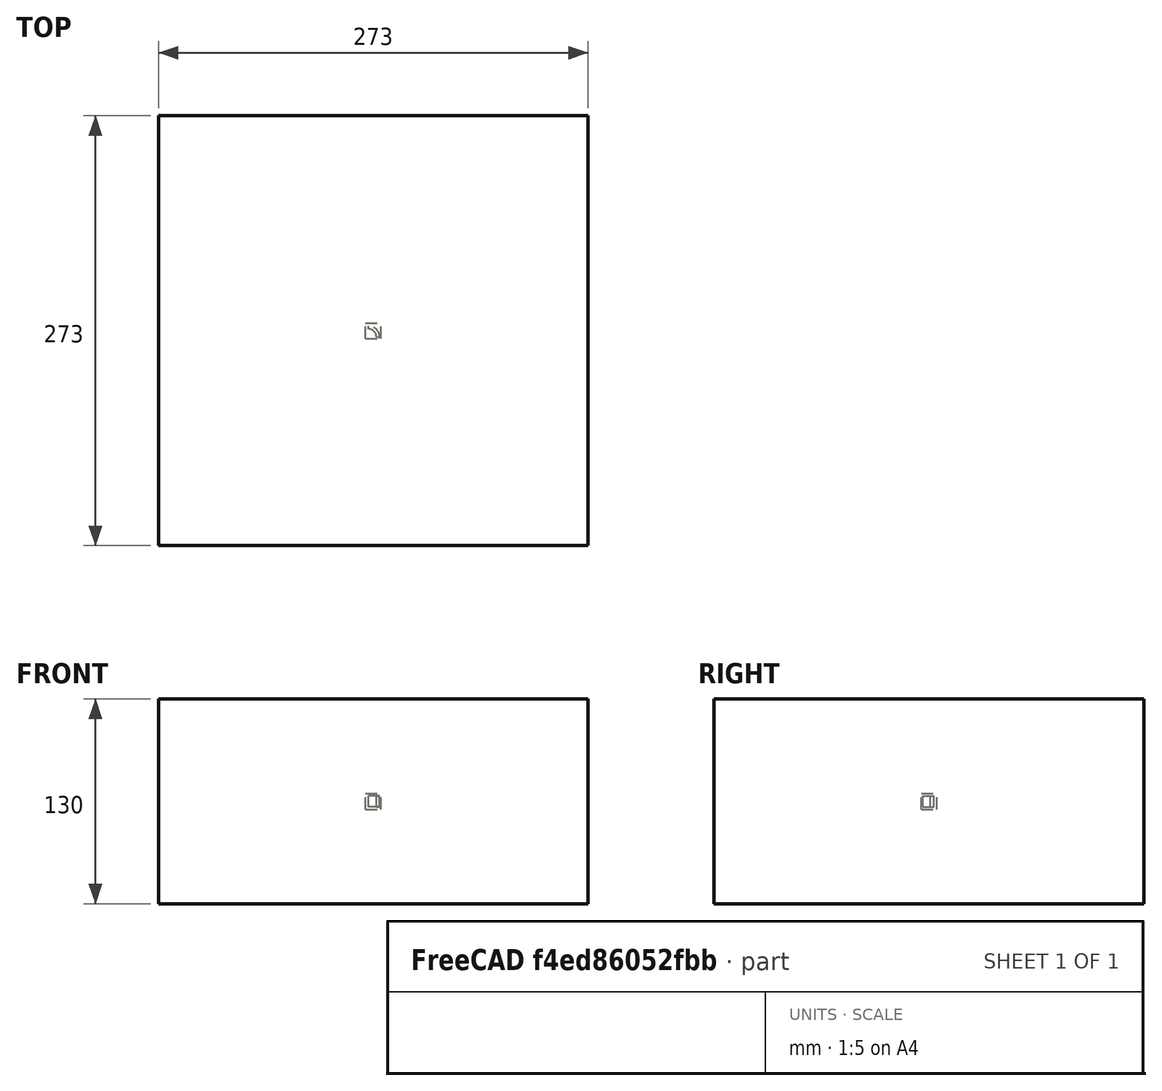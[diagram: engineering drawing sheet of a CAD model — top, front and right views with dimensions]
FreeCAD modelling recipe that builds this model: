
FCSTD DOCUMENT  (FreeCAD 0.20RUnknown)
Label: polarArray-container-c
License: All rights reserved
LicenseURL: http://en.wikipedia.org/wiki/All_rights_reserved
objects: App::DocumentObjectGroupPython×1251, Part::FeaturePython×4, App::Part×4
note: 3 computed .brp shape members not serialized (recipe doc carries the construction recipe); baked Part::Feature solids carry a one-line shape summary decoded from their .brp

FEATURE [App::DocumentObjectGroupPython] HALFPI  # scripted group (container) (typed FeaturePython)
  name = HALFPI
  value = pi/2.
FEATURE [App::DocumentObjectGroupPython] PI  # scripted group (container) (typed FeaturePython)
  name = PI
  value = 1.*pi
FEATURE [App::DocumentObjectGroupPython] TWOPI  # scripted group (container) (typed FeaturePython)
  name = TWOPI
  value = 2.*pi
FEATURE [App::DocumentObjectGroupPython] Constants  # scripted group (container) (typed FeaturePython)
  Group = -> [HALFPI,PI,TWOPI]
FEATURE [App::DocumentObjectGroupPython] Variables  # scripted group (container) (typed FeaturePython)
FEATURE [App::DocumentObjectGroupPython] Quantities  # scripted group (container) (typed FeaturePython)
FEATURE [App::DocumentObjectGroupPython] Isotopes  # scripted group (container) (typed FeaturePython)
FEATURE [App::DocumentObjectGroupPython] Elements  # scripted group (container) (typed FeaturePython)
FEATURE [App::DocumentObjectGroupPython] Matrix  # scripted group (container) (typed FeaturePython)
FEATURE [App::DocumentObjectGroupPython] Surfaces  # scripted group (container) (typed FeaturePython)
FEATURE [App::DocumentObjectGroupPython] Opticals  # scripted group (container) (typed FeaturePython)
  Group = -> [Matrix,Surfaces]
FEATURE [App::DocumentObjectGroupPython] G4Isotopes  # scripted group (container) (typed FeaturePython)
FEATURE [App::DocumentObjectGroupPython] H_element  # scripted group (container) (typed FeaturePython)
  Z = 1
  atom_value = 1.008
  formula = H
  name = H_element
FEATURE [App::DocumentObjectGroupPython] He_element  # scripted group (container) (typed FeaturePython)
  Z = 2
  atom_value = 4.0026
  formula = He
  name = He_element
FEATURE [App::DocumentObjectGroupPython] Li_element  # scripted group (container) (typed FeaturePython)
  Z = 3
  atom_value = 6.94
  formula = Li
  name = Li_element
FEATURE [App::DocumentObjectGroupPython] Be_element  # scripted group (container) (typed FeaturePython)
  Z = 4
  atom_value = 9.01218
  formula = Be
  name = Be_element
FEATURE [App::DocumentObjectGroupPython] B_element  # scripted group (container) (typed FeaturePython)
  Z = 5
  atom_value = 10.81
  formula = B
  name = B_element
FEATURE [App::DocumentObjectGroupPython] C_element  # scripted group (container) (typed FeaturePython)
  Z = 6
  atom_value = 12.011
  formula = C
  name = C_element
FEATURE [App::DocumentObjectGroupPython] N_element  # scripted group (container) (typed FeaturePython)
  Z = 7
  atom_value = 14.007
  formula = N
  name = N_element
FEATURE [App::DocumentObjectGroupPython] O_element  # scripted group (container) (typed FeaturePython)
  Z = 8
  atom_value = 15.999
  formula = O
  name = O_element
FEATURE [App::DocumentObjectGroupPython] F_element  # scripted group (container) (typed FeaturePython)
  Z = 9
  atom_value = 18.9984
  formula = F
  name = F_element
FEATURE [App::DocumentObjectGroupPython] Ne_element  # scripted group (container) (typed FeaturePython)
  Z = 10
  atom_value = 20.1797
  formula = Ne
  name = Ne_element
FEATURE [App::DocumentObjectGroupPython] Na_element  # scripted group (container) (typed FeaturePython)
  Z = 11
  atom_value = 22.9898
  formula = Na
  name = Na_element
FEATURE [App::DocumentObjectGroupPython] Mg_element  # scripted group (container) (typed FeaturePython)
  Z = 12
  atom_value = 24.305
  formula = Mg
  name = Mg_element
FEATURE [App::DocumentObjectGroupPython] Al_element  # scripted group (container) (typed FeaturePython)
  Z = 13
  atom_value = 26.9815
  formula = Al
  name = Al_element
FEATURE [App::DocumentObjectGroupPython] Si_element  # scripted group (container) (typed FeaturePython)
  Z = 14
  atom_value = 28.085
  formula = Si
  name = Si_element
FEATURE [App::DocumentObjectGroupPython] P_element  # scripted group (container) (typed FeaturePython)
  Z = 15
  atom_value = 30.9738
  formula = P
  name = P_element
FEATURE [App::DocumentObjectGroupPython] S_element  # scripted group (container) (typed FeaturePython)
  Z = 16
  atom_value = 32.06
  formula = S
  name = S_element
FEATURE [App::DocumentObjectGroupPython] Cl_element  # scripted group (container) (typed FeaturePython)
  Z = 17
  atom_value = 35.45
  formula = Cl
  name = Cl_element
FEATURE [App::DocumentObjectGroupPython] Ar_element  # scripted group (container) (typed FeaturePython)
  Z = 18
  atom_value = 39.95
  formula = Ar
  name = Ar_element
FEATURE [App::DocumentObjectGroupPython] K_element  # scripted group (container) (typed FeaturePython)
  Z = 19
  atom_value = 39.0983
  formula = K
  name = K_element
FEATURE [App::DocumentObjectGroupPython] Ca_element  # scripted group (container) (typed FeaturePython)
  Z = 20
  atom_value = 40.078
  formula = Ca
  name = Ca_element
FEATURE [App::DocumentObjectGroupPython] Sc_element  # scripted group (container) (typed FeaturePython)
  Z = 21
  atom_value = 44.9559
  formula = Sc
  name = Sc_element
FEATURE [App::DocumentObjectGroupPython] Ti_element  # scripted group (container) (typed FeaturePython)
  Z = 22
  atom_value = 47.867
  formula = Ti
  name = Ti_element
FEATURE [App::DocumentObjectGroupPython] V_element  # scripted group (container) (typed FeaturePython)
  Z = 23
  atom_value = 50.9415
  formula = V
  name = V_element
FEATURE [App::DocumentObjectGroupPython] Cr_element  # scripted group (container) (typed FeaturePython)
  Z = 24
  atom_value = 51.9961
  formula = Cr
  name = Cr_element
FEATURE [App::DocumentObjectGroupPython] Mn_element  # scripted group (container) (typed FeaturePython)
  Z = 25
  atom_value = 54.938
  formula = Mn
  name = Mn_element
FEATURE [App::DocumentObjectGroupPython] Fe_element  # scripted group (container) (typed FeaturePython)
  Z = 26
  atom_value = 55.845
  formula = Fe
  name = Fe_element
FEATURE [App::DocumentObjectGroupPython] Co_element  # scripted group (container) (typed FeaturePython)
  Z = 27
  atom_value = 58.9332
  formula = Co
  name = Co_element
FEATURE [App::DocumentObjectGroupPython] Ni_element  # scripted group (container) (typed FeaturePython)
  Z = 28
  atom_value = 58.6934
  formula = Ni
  name = Ni_element
FEATURE [App::DocumentObjectGroupPython] Cu_element  # scripted group (container) (typed FeaturePython)
  Z = 29
  atom_value = 63.546
  formula = Cu
  name = Cu_element
FEATURE [App::DocumentObjectGroupPython] Zn_element  # scripted group (container) (typed FeaturePython)
  Z = 30
  atom_value = 65.38
  formula = Zn
  name = Zn_element
FEATURE [App::DocumentObjectGroupPython] Ga_element  # scripted group (container) (typed FeaturePython)
  Z = 31
  atom_value = 69.723
  formula = Ga
  name = Ga_element
FEATURE [App::DocumentObjectGroupPython] Ge_element  # scripted group (container) (typed FeaturePython)
  Z = 32
  atom_value = 72.63
  formula = Ge
  name = Ge_element
FEATURE [App::DocumentObjectGroupPython] As_element  # scripted group (container) (typed FeaturePython)
  Z = 33
  atom_value = 74.9216
  formula = As
  name = As_element
FEATURE [App::DocumentObjectGroupPython] Se_element  # scripted group (container) (typed FeaturePython)
  Z = 34
  atom_value = 78.971
  formula = Se
  name = Se_element
FEATURE [App::DocumentObjectGroupPython] Br_element  # scripted group (container) (typed FeaturePython)
  Z = 35
  atom_value = 79.904
  formula = Br
  name = Br_element
FEATURE [App::DocumentObjectGroupPython] Kr_element  # scripted group (container) (typed FeaturePython)
  Z = 36
  atom_value = 83.798
  formula = Kr
  name = Kr_element
FEATURE [App::DocumentObjectGroupPython] Rb_element  # scripted group (container) (typed FeaturePython)
  Z = 37
  atom_value = 85.4678
  formula = Rb
  name = Rb_element
FEATURE [App::DocumentObjectGroupPython] Sr_element  # scripted group (container) (typed FeaturePython)
  Z = 38
  atom_value = 87.62
  formula = Sr
  name = Sr_element
FEATURE [App::DocumentObjectGroupPython] Y_element  # scripted group (container) (typed FeaturePython)
  Z = 39
  atom_value = 88.9058
  formula = Y
  name = Y_element
FEATURE [App::DocumentObjectGroupPython] Zr_element  # scripted group (container) (typed FeaturePython)
  Z = 40
  atom_value = 91.224
  formula = Zr
  name = Zr_element
FEATURE [App::DocumentObjectGroupPython] Nb_element  # scripted group (container) (typed FeaturePython)
  Z = 41
  atom_value = 92.9064
  formula = Nb
  name = Nb_element
FEATURE [App::DocumentObjectGroupPython] Mo_element  # scripted group (container) (typed FeaturePython)
  Z = 42
  atom_value = 95.95
  formula = Mo
  name = Mo_element
FEATURE [App::DocumentObjectGroupPython] Tc_element  # scripted group (container) (typed FeaturePython)
  Z = 43
  atom_value = 97
  formula = Tc
  name = Tc_element
FEATURE [App::DocumentObjectGroupPython] Ru_element  # scripted group (container) (typed FeaturePython)
  Z = 44
  atom_value = 101.07
  formula = Ru
  name = Ru_element
FEATURE [App::DocumentObjectGroupPython] Rh_element  # scripted group (container) (typed FeaturePython)
  Z = 45
  atom_value = 102.905
  formula = Rh
  name = Rh_element
FEATURE [App::DocumentObjectGroupPython] Pd_element  # scripted group (container) (typed FeaturePython)
  Z = 46
  atom_value = 106.42
  formula = Pd
  name = Pd_element
FEATURE [App::DocumentObjectGroupPython] Ag_element  # scripted group (container) (typed FeaturePython)
  Z = 47
  atom_value = 107.868
  formula = Ag
  name = Ag_element
FEATURE [App::DocumentObjectGroupPython] Cd_element  # scripted group (container) (typed FeaturePython)
  Z = 48
  atom_value = 112.414
  formula = Cd
  name = Cd_element
FEATURE [App::DocumentObjectGroupPython] In_element  # scripted group (container) (typed FeaturePython)
  Z = 49
  atom_value = 114.818
  formula = In
  name = In_element
FEATURE [App::DocumentObjectGroupPython] Sn_element  # scripted group (container) (typed FeaturePython)
  Z = 50
  atom_value = 118.71
  formula = Sn
  name = Sn_element
FEATURE [App::DocumentObjectGroupPython] Sb_element  # scripted group (container) (typed FeaturePython)
  Z = 51
  atom_value = 121.76
  formula = Sb
  name = Sb_element
FEATURE [App::DocumentObjectGroupPython] Te_element  # scripted group (container) (typed FeaturePython)
  Z = 52
  atom_value = 127.6
  formula = Te
  name = Te_element
FEATURE [App::DocumentObjectGroupPython] I_element  # scripted group (container) (typed FeaturePython)
  Z = 53
  atom_value = 126.904
  formula = I
  name = I_element
FEATURE [App::DocumentObjectGroupPython] Xe_element  # scripted group (container) (typed FeaturePython)
  Z = 54
  atom_value = 131.293
  formula = Xe
  name = Xe_element
FEATURE [App::DocumentObjectGroupPython] Cs_element  # scripted group (container) (typed FeaturePython)
  Z = 55
  atom_value = 132.905
  formula = Cs
  name = Cs_element
FEATURE [App::DocumentObjectGroupPython] Ba_element  # scripted group (container) (typed FeaturePython)
  Z = 56
  atom_value = 137.327
  formula = Ba
  name = Ba_element
FEATURE [App::DocumentObjectGroupPython] La_element  # scripted group (container) (typed FeaturePython)
  Z = 57
  atom_value = 138.905
  formula = La
  name = La_element
FEATURE [App::DocumentObjectGroupPython] Ce_element  # scripted group (container) (typed FeaturePython)
  Z = 58
  atom_value = 140.116
  formula = Ce
  name = Ce_element
FEATURE [App::DocumentObjectGroupPython] Pr_element  # scripted group (container) (typed FeaturePython)
  Z = 59
  atom_value = 140.908
  formula = Pr
  name = Pr_element
FEATURE [App::DocumentObjectGroupPython] Nd_element  # scripted group (container) (typed FeaturePython)
  Z = 60
  atom_value = 144.242
  formula = Nd
  name = Nd_element
FEATURE [App::DocumentObjectGroupPython] Pm_element  # scripted group (container) (typed FeaturePython)
  Z = 61
  atom_value = 145
  formula = Pm
  name = Pm_element
FEATURE [App::DocumentObjectGroupPython] Sm_element  # scripted group (container) (typed FeaturePython)
  Z = 62
  atom_value = 150.36
  formula = Sm
  name = Sm_element
FEATURE [App::DocumentObjectGroupPython] Eu_element  # scripted group (container) (typed FeaturePython)
  Z = 63
  atom_value = 151.964
  formula = Eu
  name = Eu_element
FEATURE [App::DocumentObjectGroupPython] Gd_element  # scripted group (container) (typed FeaturePython)
  Z = 64
  atom_value = 157.25
  formula = Gd
  name = Gd_element
FEATURE [App::DocumentObjectGroupPython] Tb_element  # scripted group (container) (typed FeaturePython)
  Z = 65
  atom_value = 158.925
  formula = Tb
  name = Tb_element
FEATURE [App::DocumentObjectGroupPython] Dy_element  # scripted group (container) (typed FeaturePython)
  Z = 66
  atom_value = 162.5
  formula = Dy
  name = Dy_element
FEATURE [App::DocumentObjectGroupPython] Ho_element  # scripted group (container) (typed FeaturePython)
  Z = 67
  atom_value = 164.93
  formula = Ho
  name = Ho_element
FEATURE [App::DocumentObjectGroupPython] Er_element  # scripted group (container) (typed FeaturePython)
  Z = 68
  atom_value = 167.259
  formula = Er
  name = Er_element
FEATURE [App::DocumentObjectGroupPython] Tm_element  # scripted group (container) (typed FeaturePython)
  Z = 69
  atom_value = 168.934
  formula = Tm
  name = Tm_element
FEATURE [App::DocumentObjectGroupPython] Yb_element  # scripted group (container) (typed FeaturePython)
  Z = 70
  atom_value = 173.045
  formula = Yb
  name = Yb_element
FEATURE [App::DocumentObjectGroupPython] Lu_element  # scripted group (container) (typed FeaturePython)
  Z = 71
  atom_value = 174.967
  formula = Lu
  name = Lu_element
FEATURE [App::DocumentObjectGroupPython] Hf_element  # scripted group (container) (typed FeaturePython)
  Z = 72
  atom_value = 178.49
  formula = Hf
  name = Hf_element
FEATURE [App::DocumentObjectGroupPython] Ta_element  # scripted group (container) (typed FeaturePython)
  Z = 73
  atom_value = 180.948
  formula = Ta
  name = Ta_element
FEATURE [App::DocumentObjectGroupPython] W_element  # scripted group (container) (typed FeaturePython)
  Z = 74
  atom_value = 183.84
  formula = W
  name = W_element
FEATURE [App::DocumentObjectGroupPython] Re_element  # scripted group (container) (typed FeaturePython)
  Z = 75
  atom_value = 186.207
  formula = Re
  name = Re_element
FEATURE [App::DocumentObjectGroupPython] Os_element  # scripted group (container) (typed FeaturePython)
  Z = 76
  atom_value = 190.23
  formula = Os
  name = Os_element
FEATURE [App::DocumentObjectGroupPython] Ir_element  # scripted group (container) (typed FeaturePython)
  Z = 77
  atom_value = 192.217
  formula = Ir
  name = Ir_element
FEATURE [App::DocumentObjectGroupPython] Pt_element  # scripted group (container) (typed FeaturePython)
  Z = 78
  atom_value = 195.084
  formula = Pt
  name = Pt_element
FEATURE [App::DocumentObjectGroupPython] Au_element  # scripted group (container) (typed FeaturePython)
  Z = 79
  atom_value = 196.967
  formula = Au
  name = Au_element
FEATURE [App::DocumentObjectGroupPython] Hg_element  # scripted group (container) (typed FeaturePython)
  Z = 80
  atom_value = 200.592
  formula = Hg
  name = Hg_element
FEATURE [App::DocumentObjectGroupPython] Tl_element  # scripted group (container) (typed FeaturePython)
  Z = 81
  atom_value = 204.38
  formula = Tl
  name = Tl_element
FEATURE [App::DocumentObjectGroupPython] Pb_element  # scripted group (container) (typed FeaturePython)
  Z = 82
  atom_value = 207.2
  formula = Pb
  name = Pb_element
FEATURE [App::DocumentObjectGroupPython] Bi_element  # scripted group (container) (typed FeaturePython)
  Z = 83
  atom_value = 208.98
  formula = Bi
  name = Bi_element
FEATURE [App::DocumentObjectGroupPython] Po_element  # scripted group (container) (typed FeaturePython)
  Z = 84
  atom_value = 209
  formula = Po
  name = Po_element
FEATURE [App::DocumentObjectGroupPython] At_element  # scripted group (container) (typed FeaturePython)
  Z = 85
  atom_value = 210
  formula = At
  name = At_element
FEATURE [App::DocumentObjectGroupPython] Rn_element  # scripted group (container) (typed FeaturePython)
  Z = 86
  atom_value = 222
  formula = Rn
  name = Rn_element
FEATURE [App::DocumentObjectGroupPython] Fr_element  # scripted group (container) (typed FeaturePython)
  Z = 87
  atom_value = 223
  formula = Fr
  name = Fr_element
FEATURE [App::DocumentObjectGroupPython] Ra_element  # scripted group (container) (typed FeaturePython)
  Z = 88
  atom_value = 226
  formula = Ra
  name = Ra_element
FEATURE [App::DocumentObjectGroupPython] Ac_element  # scripted group (container) (typed FeaturePython)
  Z = 89
  atom_value = 227
  formula = Ac
  name = Ac_element
FEATURE [App::DocumentObjectGroupPython] Th_element  # scripted group (container) (typed FeaturePython)
  Z = 90
  atom_value = 232.038
  formula = Th
  name = Th_element
FEATURE [App::DocumentObjectGroupPython] Pa_element  # scripted group (container) (typed FeaturePython)
  Z = 91
  atom_value = 231.036
  formula = Pa
  name = Pa_element
FEATURE [App::DocumentObjectGroupPython] U_element  # scripted group (container) (typed FeaturePython)
  Z = 92
  atom_value = 238.029
  formula = U
  name = U_element
FEATURE [App::DocumentObjectGroupPython] Np_element  # scripted group (container) (typed FeaturePython)
  Z = 93
  atom_value = 237
  formula = Np
  name = Np_element
FEATURE [App::DocumentObjectGroupPython] Pu_element  # scripted group (container) (typed FeaturePython)
  Z = 94
  atom_value = 244
  formula = Pu
  name = Pu_element
FEATURE [App::DocumentObjectGroupPython] Am_element  # scripted group (container) (typed FeaturePython)
  Z = 95
  atom_value = 243
  formula = Am
  name = Am_element
FEATURE [App::DocumentObjectGroupPython] Cm_element  # scripted group (container) (typed FeaturePython)
  Z = 96
  atom_value = 247
  formula = Cm
  name = Cm_element
FEATURE [App::DocumentObjectGroupPython] Bk_element  # scripted group (container) (typed FeaturePython)
  Z = 97
  atom_value = 247
  formula = Bk
  name = Bk_element
FEATURE [App::DocumentObjectGroupPython] Cf_element  # scripted group (container) (typed FeaturePython)
  Z = 98
  atom_value = 251
  formula = Cf
  name = Cf_element
FEATURE [App::DocumentObjectGroupPython] G4Elements  # scripted group (container) (typed FeaturePython)
  Group = -> [H_element,He_element,Li_element,Be_element,B_element,C_element,N_element,O_element,F_element,Ne_element,Na_element,Mg_element,Al_element,Si_element,P_element,S_element,Cl_element,Ar_element,K_element,Ca_element,Sc_element,Ti_element,V_element,Cr_element,Mn_element,Fe_element,Co_element,Ni_element,Cu_element,Zn_element,Ga_element,Ge_element,As_element,Se_element,Br_element,Kr_element,Rb_element,+61 more]
FEATURE [App::DocumentObjectGroupPython] H_element001  label="H_element : 0.101"  # scripted group (container) (typed FeaturePython)
  n = 0.101327
FEATURE [App::DocumentObjectGroupPython] C_element001  label="C_element : 0.775"  # scripted group (container) (typed FeaturePython)
  n = 0.7755
FEATURE [App::DocumentObjectGroupPython] N_element001  label="N_element : 0.035"  # scripted group (container) (typed FeaturePython)
  n = 0.035057
FEATURE [App::DocumentObjectGroupPython] O_element001  label="O_element : 0.052"  # scripted group (container) (typed FeaturePython)
  n = 0.0523159
FEATURE [App::DocumentObjectGroupPython] F_element001  label="F_element : 0.017"  # scripted group (container) (typed FeaturePython)
  n = 0.017422
FEATURE [App::DocumentObjectGroupPython] Ca_element001  label="Ca_element : 0.018"  # scripted group (container) (typed FeaturePython)
  n = 0.018378
FEATURE [App::DocumentObjectGroupPython] G4_A_150_TISSUE  label="G4_A-150_TISSUE"  # scripted group (container) (typed FeaturePython)
  Dunit = g/cm3
  Dvalue = 1.127
  Group = -> [H_element001,C_element001,N_element001,O_element001,F_element001,Ca_element001]
  conduct = 2
  density = 1
  expand = 3
  formula = G4_A-150_TISSUE
  name = G4_A-150_TISSUE
  specific = 4
FEATURE [App::DocumentObjectGroupPython] C_element002  label="C_element : 3"  # scripted group (container) (typed FeaturePython)
  n = 3
  ref = C_element
FEATURE [App::DocumentObjectGroupPython] H_element002  label="H_element : 6"  # scripted group (container) (typed FeaturePython)
  n = 6
  ref = H_element
FEATURE [App::DocumentObjectGroupPython] O_element002  label="O_element : 1"  # scripted group (container) (typed FeaturePython)
  n = 1
  ref = O_element
FEATURE [App::DocumentObjectGroupPython] G4_ACETONE  # scripted group (container) (typed FeaturePython)
  Dunit = g/cm3
  Dvalue = 0.7899
  Group = -> [C_element002,H_element002,O_element002]
  conduct = 2
  density = 1
  expand = 3
  formula = G4_ACETONE
  name = G4_ACETONE
  specific = 4
FEATURE [App::DocumentObjectGroupPython] C_element003  label="C_element : 2"  # scripted group (container) (typed FeaturePython)
  n = 2
  ref = C_element
FEATURE [App::DocumentObjectGroupPython] H_element003  label="H_element : 2"  # scripted group (container) (typed FeaturePython)
  n = 2
  ref = H_element
FEATURE [App::DocumentObjectGroupPython] G4_ACETYLENE  # scripted group (container) (typed FeaturePython)
  Dunit = g/cm3
  Dvalue = 0.0010967
  Group = -> [C_element003,H_element003]
  conduct = 2
  density = 1
  expand = 3
  formula = G4_ACETYLENE
  name = G4_ACETYLENE
  specific = 4
FEATURE [App::DocumentObjectGroupPython] C_element004  label="C_element : 5"  # scripted group (container) (typed FeaturePython)
  n = 5
  ref = C_element
FEATURE [App::DocumentObjectGroupPython] H_element004  label="H_element : 5"  # scripted group (container) (typed FeaturePython)
  n = 5
  ref = H_element
FEATURE [App::DocumentObjectGroupPython] N_element002  label="N_element : 5"  # scripted group (container) (typed FeaturePython)
  n = 5
  ref = N_element
FEATURE [App::DocumentObjectGroupPython] G4_ADENINE  # scripted group (container) (typed FeaturePython)
  Dunit = g/cm3
  Dvalue = 1.6
  Group = -> [C_element004,H_element004,N_element002]
  conduct = 2
  density = 1
  expand = 3
  formula = G4_ADENINE
  name = G4_ADENINE
  specific = 4
FEATURE [App::DocumentObjectGroupPython] H_element005  label="H_element : 0.114"  # scripted group (container) (typed FeaturePython)
  n = 0.114
FEATURE [App::DocumentObjectGroupPython] C_element005  label="C_element : 0.598"  # scripted group (container) (typed FeaturePython)
  n = 0.598
FEATURE [App::DocumentObjectGroupPython] N_element003  label="N_element : 0.007"  # scripted group (container) (typed FeaturePython)
  n = 0.007
FEATURE [App::DocumentObjectGroupPython] O_element003  label="O_element : 0.278"  # scripted group (container) (typed FeaturePython)
  n = 0.278
FEATURE [App::DocumentObjectGroupPython] Na_element001  label="Na_element : 0.001"  # scripted group (container) (typed FeaturePython)
  n = 0.001
FEATURE [App::DocumentObjectGroupPython] S_element001  label="S_element : 0.001"  # scripted group (container) (typed FeaturePython)
  n = 0.001
FEATURE [App::DocumentObjectGroupPython] Cl_element001  label="Cl_element : 0.001"  # scripted group (container) (typed FeaturePython)
  n = 0.001
FEATURE [App::DocumentObjectGroupPython] G4_ADIPOSE_TISSUE_ICRP  # scripted group (container) (typed FeaturePython)
  Dunit = g/cm3
  Dvalue = 0.95
  Group = -> [H_element005,C_element005,N_element003,O_element003,Na_element001,S_element001,Cl_element001]
  conduct = 2
  density = 1
  expand = 3
  formula = G4_ADIPOSE_TISSUE_ICRP
  name = G4_ADIPOSE_TISSUE_ICRP
  specific = 4
FEATURE [App::DocumentObjectGroupPython] C_element006  label="C_element : 0.000"  # scripted group (container) (typed FeaturePython)
  n = 0.000124
FEATURE [App::DocumentObjectGroupPython] N_element004  label="N_element : 0.755"  # scripted group (container) (typed FeaturePython)
  n = 0.755268
FEATURE [App::DocumentObjectGroupPython] O_element004  label="O_element : 0.232"  # scripted group (container) (typed FeaturePython)
  n = 0.231781
FEATURE [App::DocumentObjectGroupPython] Ar_element001  label="Ar_element : 0.013"  # scripted group (container) (typed FeaturePython)
  n = 0.012827
FEATURE [App::DocumentObjectGroupPython] G4_AIR  # scripted group (container) (typed FeaturePython)
  Dunit = g/cm3
  Dvalue = 0.00120479
  Group = -> [C_element006,N_element004,O_element004,Ar_element001]
  conduct = 2
  density = 1
  expand = 3
  formula = G4_AIR
  name = G4_AIR
  specific = 4
FEATURE [App::DocumentObjectGroupPython] C_element007  label="C_element : 006"  # scripted group (container) (typed FeaturePython)
  n = 3
  ref = C_element
FEATURE [App::DocumentObjectGroupPython] H_element006  label="H_element : 7"  # scripted group (container) (typed FeaturePython)
  n = 7
  ref = H_element
FEATURE [App::DocumentObjectGroupPython] N_element005  label="N_element : 1"  # scripted group (container) (typed FeaturePython)
  n = 1
  ref = N_element
FEATURE [App::DocumentObjectGroupPython] O_element005  label="O_element : 2"  # scripted group (container) (typed FeaturePython)
  n = 2
  ref = O_element
FEATURE [App::DocumentObjectGroupPython] G4_ALANINE  # scripted group (container) (typed FeaturePython)
  Dunit = g/cm3
  Dvalue = 1.42
  Group = -> [C_element007,H_element006,N_element005,O_element005]
  conduct = 2
  density = 1
  expand = 3
  formula = G4_ALANINE
  name = G4_ALANINE
  specific = 4
FEATURE [App::DocumentObjectGroupPython] Al_element001  label="Al_element : 2"  # scripted group (container) (typed FeaturePython)
  n = 2
  ref = Al_element
FEATURE [App::DocumentObjectGroupPython] O_element006  label="O_element : 3"  # scripted group (container) (typed FeaturePython)
  n = 3
  ref = O_element
FEATURE [App::DocumentObjectGroupPython] G4_ALUMINUM_OXIDE  # scripted group (container) (typed FeaturePython)
  Dunit = g/cm3
  Dvalue = 3.97
  Group = -> [Al_element001,O_element006]
  conduct = 2
  density = 1
  expand = 3
  formula = G4_ALUMINUM_OXIDE
  name = G4_ALUMINUM_OXIDE
  specific = 4
FEATURE [App::DocumentObjectGroupPython] H_element007  label="H_element : 0.106"  # scripted group (container) (typed FeaturePython)
  n = 0.10593
FEATURE [App::DocumentObjectGroupPython] C_element008  label="C_element : 0.789"  # scripted group (container) (typed FeaturePython)
  n = 0.788974
FEATURE [App::DocumentObjectGroupPython] O_element007  label="O_element : 0.105"  # scripted group (container) (typed FeaturePython)
  n = 0.105096
FEATURE [App::DocumentObjectGroupPython] G4_AMBER  # scripted group (container) (typed FeaturePython)
  Dunit = g/cm3
  Dvalue = 1.1
  Group = -> [H_element007,C_element008,O_element007]
  conduct = 2
  density = 1
  expand = 3
  formula = G4_AMBER
  name = G4_AMBER
  specific = 4
FEATURE [App::DocumentObjectGroupPython] N_element006  label="N_element : 006"  # scripted group (container) (typed FeaturePython)
  n = 1
  ref = N_element
FEATURE [App::DocumentObjectGroupPython] H_element008  label="H_element : 3"  # scripted group (container) (typed FeaturePython)
  n = 3
  ref = H_element
FEATURE [App::DocumentObjectGroupPython] G4_AMMONIA  # scripted group (container) (typed FeaturePython)
  Dunit = g/cm3
  Dvalue = 0.000826019
  Group = -> [N_element006,H_element008]
  conduct = 2
  density = 1
  expand = 3
  formula = G4_AMMONIA
  name = G4_AMMONIA
  specific = 4
FEATURE [App::DocumentObjectGroupPython] C_element009  label="C_element : 6"  # scripted group (container) (typed FeaturePython)
  n = 6
  ref = C_element
FEATURE [App::DocumentObjectGroupPython] H_element009  label="H_element : 008"  # scripted group (container) (typed FeaturePython)
  n = 7
  ref = H_element
FEATURE [App::DocumentObjectGroupPython] N_element007  label="N_element : 007"  # scripted group (container) (typed FeaturePython)
  n = 1
  ref = N_element
FEATURE [App::DocumentObjectGroupPython] G4_ANILINE  # scripted group (container) (typed FeaturePython)
  Dunit = g/cm3
  Dvalue = 1.0235
  Group = -> [C_element009,H_element009,N_element007]
  conduct = 2
  density = 1
  expand = 3
  formula = G4_ANILINE
  name = G4_ANILINE
  specific = 4
FEATURE [App::DocumentObjectGroupPython] C_element010  label="C_element : 14"  # scripted group (container) (typed FeaturePython)
  n = 14
  ref = C_element
FEATURE [App::DocumentObjectGroupPython] H_element010  label="H_element : 10"  # scripted group (container) (typed FeaturePython)
  n = 10
  ref = H_element
FEATURE [App::DocumentObjectGroupPython] G4_ANTHRACENE  # scripted group (container) (typed FeaturePython)
  Dunit = g/cm3
  Dvalue = 1.283
  Group = -> [C_element010,H_element010]
  conduct = 2
  density = 1
  expand = 3
  formula = G4_ANTHRACENE
  name = G4_ANTHRACENE
  specific = 4
FEATURE [App::DocumentObjectGroupPython] H_element011  label="H_element : 0.065"  # scripted group (container) (typed FeaturePython)
  n = 0.0654709
FEATURE [App::DocumentObjectGroupPython] C_element011  label="C_element : 0.537"  # scripted group (container) (typed FeaturePython)
  n = 0.536944
FEATURE [App::DocumentObjectGroupPython] N_element008  label="N_element : 0.021"  # scripted group (container) (typed FeaturePython)
  n = 0.0215
FEATURE [App::DocumentObjectGroupPython] O_element008  label="O_element : 0.032"  # scripted group (container) (typed FeaturePython)
  n = 0.032085
FEATURE [App::DocumentObjectGroupPython] F_element002  label="F_element : 0.167"  # scripted group (container) (typed FeaturePython)
  n = 0.167411
FEATURE [App::DocumentObjectGroupPython] Ca_element002  label="Ca_element : 0.177"  # scripted group (container) (typed FeaturePython)
  n = 0.176589
FEATURE [App::DocumentObjectGroupPython] G4_B_100_BONE  label="G4_B-100_BONE"  # scripted group (container) (typed FeaturePython)
  Dunit = g/cm3
  Dvalue = 1.45
  Group = -> [H_element011,C_element011,N_element008,O_element008,F_element002,Ca_element002]
  conduct = 2
  density = 1
  expand = 3
  formula = G4_B-100_BONE
  name = G4_B-100_BONE
  specific = 4
FEATURE [App::DocumentObjectGroupPython] H_element012  label="H_element : 0.057"  # scripted group (container) (typed FeaturePython)
  n = 0.057441
FEATURE [App::DocumentObjectGroupPython] C_element012  label="C_element : 0.790"  # scripted group (container) (typed FeaturePython)
  n = 0.774591
FEATURE [App::DocumentObjectGroupPython] O_element009  label="O_element : 0.168"  # scripted group (container) (typed FeaturePython)
  n = 0.167968
FEATURE [App::DocumentObjectGroupPython] G4_BAKELITE  # scripted group (container) (typed FeaturePython)
  Dunit = g/cm3
  Dvalue = 1.25
  Group = -> [H_element012,C_element012,O_element009]
  conduct = 2
  density = 1
  expand = 3
  formula = G4_BAKELITE
  name = G4_BAKELITE
  specific = 4
FEATURE [App::DocumentObjectGroupPython] Ba_element001  label="Ba_element : 1"  # scripted group (container) (typed FeaturePython)
  n = 1
  ref = Ba_element
FEATURE [App::DocumentObjectGroupPython] F_element003  label="F_element : 2"  # scripted group (container) (typed FeaturePython)
  n = 2
  ref = F_element
FEATURE [App::DocumentObjectGroupPython] G4_BARIUM_FLUORIDE  # scripted group (container) (typed FeaturePython)
  Dunit = g/cm3
  Dvalue = 4.89
  Group = -> [Ba_element001,F_element003]
  conduct = 2
  density = 1
  expand = 3
  formula = G4_BARIUM_FLUORIDE
  name = G4_BARIUM_FLUORIDE
  specific = 4
FEATURE [App::DocumentObjectGroupPython] Ba_element002  label="Ba_element : 002"  # scripted group (container) (typed FeaturePython)
  n = 1
  ref = Ba_element
FEATURE [App::DocumentObjectGroupPython] S_element002  label="S_element : 1"  # scripted group (container) (typed FeaturePython)
  n = 1
  ref = S_element
FEATURE [App::DocumentObjectGroupPython] O_element010  label="O_element : 4"  # scripted group (container) (typed FeaturePython)
  n = 4
  ref = O_element
FEATURE [App::DocumentObjectGroupPython] G4_BARIUM_SULFATE  # scripted group (container) (typed FeaturePython)
  Dunit = g/cm3
  Dvalue = 4.5
  Group = -> [Ba_element002,S_element002,O_element010]
  conduct = 2
  density = 1
  expand = 3
  formula = G4_BARIUM_SULFATE
  name = G4_BARIUM_SULFATE
  specific = 4
FEATURE [App::DocumentObjectGroupPython] C_element013  label="C_element : 007"  # scripted group (container) (typed FeaturePython)
  n = 6
  ref = C_element
FEATURE [App::DocumentObjectGroupPython] H_element013  label="H_element : 009"  # scripted group (container) (typed FeaturePython)
  n = 6
  ref = H_element
FEATURE [App::DocumentObjectGroupPython] G4_BENZENE  # scripted group (container) (typed FeaturePython)
  Dunit = g/cm3
  Dvalue = 0.87865
  Group = -> [C_element013,H_element013]
  conduct = 2
  density = 1
  expand = 3
  formula = G4_BENZENE
  name = G4_BENZENE
  specific = 4
FEATURE [App::DocumentObjectGroupPython] Be_element001  label="Be_element : 1"  # scripted group (container) (typed FeaturePython)
  n = 1
  ref = Be_element
FEATURE [App::DocumentObjectGroupPython] O_element011  label="O_element : 005"  # scripted group (container) (typed FeaturePython)
  n = 1
  ref = O_element
FEATURE [App::DocumentObjectGroupPython] G4_BERYLLIUM_OXIDE  # scripted group (container) (typed FeaturePython)
  Dunit = g/cm3
  Dvalue = 3.01
  Group = -> [Be_element001,O_element011]
  conduct = 2
  density = 1
  expand = 3
  formula = G4_BERYLLIUM_OXIDE
  name = G4_BERYLLIUM_OXIDE
  specific = 4
FEATURE [App::DocumentObjectGroupPython] Bi_element001  label="Bi_element : 4"  # scripted group (container) (typed FeaturePython)
  n = 4
  ref = Bi_element
FEATURE [App::DocumentObjectGroupPython] Ge_element001  label="Ge_element : 3"  # scripted group (container) (typed FeaturePython)
  n = 3
  ref = Ge_element
FEATURE [App::DocumentObjectGroupPython] O_element012  label="O_element : 12"  # scripted group (container) (typed FeaturePython)
  n = 12
  ref = O_element
FEATURE [App::DocumentObjectGroupPython] G4_BGO  # scripted group (container) (typed FeaturePython)
  Dunit = g/cm3
  Dvalue = 7.13
  Group = -> [Bi_element001,Ge_element001,O_element012]
  conduct = 2
  density = 1
  expand = 3
  formula = G4_BGO
  name = G4_BGO
  specific = 4
FEATURE [App::DocumentObjectGroupPython] H_element014  label="H_element : 0.102"  # scripted group (container) (typed FeaturePython)
  n = 0.102
FEATURE [App::DocumentObjectGroupPython] C_element014  label="C_element : 0.110"  # scripted group (container) (typed FeaturePython)
  n = 0.11
FEATURE [App::DocumentObjectGroupPython] N_element009  label="N_element : 0.033"  # scripted group (container) (typed FeaturePython)
  n = 0.033
FEATURE [App::DocumentObjectGroupPython] O_element013  label="O_element : 0.745"  # scripted group (container) (typed FeaturePython)
  n = 0.745
FEATURE [App::DocumentObjectGroupPython] Na_element002  label="Na_element : 0.002"  # scripted group (container) (typed FeaturePython)
  n = 0.001
FEATURE [App::DocumentObjectGroupPython] P_element001  label="P_element : 0.001"  # scripted group (container) (typed FeaturePython)
  n = 0.001
FEATURE [App::DocumentObjectGroupPython] S_element003  label="S_element : 0.002"  # scripted group (container) (typed FeaturePython)
  n = 0.002
FEATURE [App::DocumentObjectGroupPython] Cl_element002  label="Cl_element : 0.003"  # scripted group (container) (typed FeaturePython)
  n = 0.003
FEATURE [App::DocumentObjectGroupPython] K_element001  label="K_element : 0.002"  # scripted group (container) (typed FeaturePython)
  n = 0.002
FEATURE [App::DocumentObjectGroupPython] Fe_element001  label="Fe_element : 0.001"  # scripted group (container) (typed FeaturePython)
  n = 0.001
FEATURE [App::DocumentObjectGroupPython] G4_BLOOD_ICRP  # scripted group (container) (typed FeaturePython)
  Dunit = g/cm3
  Dvalue = 1.06
  Group = -> [H_element014,C_element014,N_element009,O_element013,Na_element002,P_element001,S_element003,Cl_element002,K_element001,Fe_element001]
  conduct = 2
  density = 1
  expand = 3
  formula = G4_BLOOD_ICRP
  name = G4_BLOOD_ICRP
  specific = 4
FEATURE [App::DocumentObjectGroupPython] H_element015  label="H_element : 0.064"  # scripted group (container) (typed FeaturePython)
  n = 0.064
FEATURE [App::DocumentObjectGroupPython] C_element015  label="C_element : 0.278"  # scripted group (container) (typed FeaturePython)
  n = 0.278
FEATURE [App::DocumentObjectGroupPython] N_element010  label="N_element : 0.027"  # scripted group (container) (typed FeaturePython)
  n = 0.027
FEATURE [App::DocumentObjectGroupPython] O_element014  label="O_element : 0.410"  # scripted group (container) (typed FeaturePython)
  n = 0.41
FEATURE [App::DocumentObjectGroupPython] Mg_element001  label="Mg_element : 0.002"  # scripted group (container) (typed FeaturePython)
  n = 0.002
FEATURE [App::DocumentObjectGroupPython] P_element002  label="P_element : 0.070"  # scripted group (container) (typed FeaturePython)
  n = 0.07
FEATURE [App::DocumentObjectGroupPython] S_element004  label="S_element : 0.003"  # scripted group (container) (typed FeaturePython)
  n = 0.002
FEATURE [App::DocumentObjectGroupPython] Ca_element003  label="Ca_element : 0.147"  # scripted group (container) (typed FeaturePython)
  n = 0.147
FEATURE [App::DocumentObjectGroupPython] G4_BONE_COMPACT_ICRU  # scripted group (container) (typed FeaturePython)
  Dunit = g/cm3
  Dvalue = 1.85
  Group = -> [H_element015,C_element015,N_element010,O_element014,Mg_element001,P_element002,S_element004,Ca_element003]
  conduct = 2
  density = 1
  expand = 3
  formula = G4_BONE_COMPACT_ICRU
  name = G4_BONE_COMPACT_ICRU
  specific = 4
FEATURE [App::DocumentObjectGroupPython] H_element016  label="H_element : 0.034"  # scripted group (container) (typed FeaturePython)
  n = 0.034
FEATURE [App::DocumentObjectGroupPython] C_element016  label="C_element : 0.155"  # scripted group (container) (typed FeaturePython)
  n = 0.155
FEATURE [App::DocumentObjectGroupPython] N_element011  label="N_element : 0.042"  # scripted group (container) (typed FeaturePython)
  n = 0.042
FEATURE [App::DocumentObjectGroupPython] O_element015  label="O_element : 0.435"  # scripted group (container) (typed FeaturePython)
  n = 0.435
FEATURE [App::DocumentObjectGroupPython] Na_element003  label="Na_element : 0.003"  # scripted group (container) (typed FeaturePython)
  n = 0.001
FEATURE [App::DocumentObjectGroupPython] Mg_element002  label="Mg_element : 0.003"  # scripted group (container) (typed FeaturePython)
  n = 0.002
FEATURE [App::DocumentObjectGroupPython] P_element003  label="P_element : 0.103"  # scripted group (container) (typed FeaturePython)
  n = 0.103
FEATURE [App::DocumentObjectGroupPython] S_element005  label="S_element : 0.004"  # scripted group (container) (typed FeaturePython)
  n = 0.003
FEATURE [App::DocumentObjectGroupPython] Ca_element004  label="Ca_element : 0.225"  # scripted group (container) (typed FeaturePython)
  n = 0.225
FEATURE [App::DocumentObjectGroupPython] G4_BONE_CORTICAL_ICRP  # scripted group (container) (typed FeaturePython)
  Dunit = g/cm3
  Dvalue = 1.92
  Group = -> [H_element016,C_element016,N_element011,O_element015,Na_element003,Mg_element002,P_element003,S_element005,Ca_element004]
  conduct = 2
  density = 1
  expand = 3
  formula = G4_BONE_CORTICAL_ICRP
  name = G4_BONE_CORTICAL_ICRP
  specific = 4
FEATURE [App::DocumentObjectGroupPython] B_element001  label="B_element : 4"  # scripted group (container) (typed FeaturePython)
  n = 4
  ref = B_element
FEATURE [App::DocumentObjectGroupPython] C_element017  label="C_element : 1"  # scripted group (container) (typed FeaturePython)
  n = 1
  ref = C_element
FEATURE [App::DocumentObjectGroupPython] G4_BORON_CARBIDE  # scripted group (container) (typed FeaturePython)
  Dunit = g/cm3
  Dvalue = 2.52
  Group = -> [B_element001,C_element017]
  conduct = 2
  density = 1
  expand = 3
  formula = G4_BORON_CARBIDE
  name = G4_BORON_CARBIDE
  specific = 4
FEATURE [App::DocumentObjectGroupPython] B_element002  label="B_element : 2"  # scripted group (container) (typed FeaturePython)
  n = 2
  ref = B_element
FEATURE [App::DocumentObjectGroupPython] O_element016  label="O_element : 006"  # scripted group (container) (typed FeaturePython)
  n = 3
  ref = O_element
FEATURE [App::DocumentObjectGroupPython] G4_BORON_OXIDE  # scripted group (container) (typed FeaturePython)
  Dunit = g/cm3
  Dvalue = 1.812
  Group = -> [B_element002,O_element016]
  conduct = 2
  density = 1
  expand = 3
  formula = G4_BORON_OXIDE
  name = G4_BORON_OXIDE
  specific = 4
FEATURE [App::DocumentObjectGroupPython] H_element017  label="H_element : 0.107"  # scripted group (container) (typed FeaturePython)
  n = 0.107
FEATURE [App::DocumentObjectGroupPython] C_element018  label="C_element : 0.145"  # scripted group (container) (typed FeaturePython)
  n = 0.145
FEATURE [App::DocumentObjectGroupPython] N_element012  label="N_element : 0.022"  # scripted group (container) (typed FeaturePython)
  n = 0.022
FEATURE [App::DocumentObjectGroupPython] O_element017  label="O_element : 0.712"  # scripted group (container) (typed FeaturePython)
  n = 0.712
FEATURE [App::DocumentObjectGroupPython] Na_element004  label="Na_element : 0.004"  # scripted group (container) (typed FeaturePython)
  n = 0.002
FEATURE [App::DocumentObjectGroupPython] P_element004  label="P_element : 0.004"  # scripted group (container) (typed FeaturePython)
  n = 0.004
FEATURE [App::DocumentObjectGroupPython] S_element006  label="S_element : 0.005"  # scripted group (container) (typed FeaturePython)
  n = 0.002
FEATURE [App::DocumentObjectGroupPython] Cl_element003  label="Cl_element : 0.004"  # scripted group (container) (typed FeaturePython)
  n = 0.003
FEATURE [App::DocumentObjectGroupPython] K_element002  label="K_element : 0.003"  # scripted group (container) (typed FeaturePython)
  n = 0.003
FEATURE [App::DocumentObjectGroupPython] G4_BRAIN_ICRP  # scripted group (container) (typed FeaturePython)
  Dunit = g/cm3
  Dvalue = 1.04
  Group = -> [H_element017,C_element018,N_element012,O_element017,Na_element004,P_element004,S_element006,Cl_element003,K_element002]
  conduct = 2
  density = 1
  expand = 3
  formula = G4_BRAIN_ICRP
  name = G4_BRAIN_ICRP
  specific = 4
FEATURE [App::DocumentObjectGroupPython] C_element019  label="C_element : 4"  # scripted group (container) (typed FeaturePython)
  n = 4
  ref = C_element
FEATURE [App::DocumentObjectGroupPython] H_element018  label="H_element : 010"  # scripted group (container) (typed FeaturePython)
  n = 10
  ref = H_element
FEATURE [App::DocumentObjectGroupPython] G4_BUTANE  # scripted group (container) (typed FeaturePython)
  Dunit = g/cm3
  Dvalue = 0.00249343
  Group = -> [C_element019,H_element018]
  conduct = 2
  density = 1
  expand = 3
  formula = G4_BUTANE
  name = G4_BUTANE
  specific = 4
FEATURE [App::DocumentObjectGroupPython] C_element020  label="C_element : 008"  # scripted group (container) (typed FeaturePython)
  n = 4
  ref = C_element
FEATURE [App::DocumentObjectGroupPython] H_element019  label="H_element : 011"  # scripted group (container) (typed FeaturePython)
  n = 10
  ref = H_element
FEATURE [App::DocumentObjectGroupPython] O_element018  label="O_element : 007"  # scripted group (container) (typed FeaturePython)
  n = 1
  ref = O_element
FEATURE [App::DocumentObjectGroupPython] G4_N_BUTYL_ALCOHOL  label="G4_N-BUTYL_ALCOHOL"  # scripted group (container) (typed FeaturePython)
  Dunit = g/cm3
  Dvalue = 0.8098
  Group = -> [C_element020,H_element019,O_element018]
  conduct = 2
  density = 1
  expand = 3
  formula = G4_N-BUTYL_ALCOHOL
  name = G4_N-BUTYL_ALCOHOL
  specific = 4
FEATURE [App::DocumentObjectGroupPython] H_element020  label="H_element : 0.025"  # scripted group (container) (typed FeaturePython)
  n = 0.02468
FEATURE [App::DocumentObjectGroupPython] C_element021  label="C_element : 0.502"  # scripted group (container) (typed FeaturePython)
  n = 0.501611
FEATURE [App::DocumentObjectGroupPython] O_element019  label="O_element : 0.005"  # scripted group (container) (typed FeaturePython)
  n = 0.004527
FEATURE [App::DocumentObjectGroupPython] F_element004  label="F_element : 0.465"  # scripted group (container) (typed FeaturePython)
  n = 0.465209
FEATURE [App::DocumentObjectGroupPython] Si_element001  label="Si_element : 0.004"  # scripted group (container) (typed FeaturePython)
  n = 0.003973
FEATURE [App::DocumentObjectGroupPython] G4_C_552  label="G4_C-552"  # scripted group (container) (typed FeaturePython)
  Dunit = g/cm3
  Dvalue = 1.76
  Group = -> [H_element020,C_element021,O_element019,F_element004,Si_element001]
  conduct = 2
  density = 1
  expand = 3
  formula = G4_C-552
  name = G4_C-552
  specific = 4
FEATURE [App::DocumentObjectGroupPython] Cd_element001  label="Cd_element : 1"  # scripted group (container) (typed FeaturePython)
  n = 1
  ref = Cd_element
FEATURE [App::DocumentObjectGroupPython] Te_element001  label="Te_element : 1"  # scripted group (container) (typed FeaturePython)
  n = 1
  ref = Te_element
FEATURE [App::DocumentObjectGroupPython] G4_CADMIUM_TELLURIDE  # scripted group (container) (typed FeaturePython)
  Dunit = g/cm3
  Dvalue = 6.2
  Group = -> [Cd_element001,Te_element001]
  conduct = 2
  density = 1
  expand = 3
  formula = G4_CADMIUM_TELLURIDE
  name = G4_CADMIUM_TELLURIDE
  specific = 4
FEATURE [App::DocumentObjectGroupPython] Cd_element002  label="Cd_element : 002"  # scripted group (container) (typed FeaturePython)
  n = 1
  ref = Cd_element
FEATURE [App::DocumentObjectGroupPython] W_element001  label="W_element : 1"  # scripted group (container) (typed FeaturePython)
  n = 1
  ref = W_element
FEATURE [App::DocumentObjectGroupPython] O_element020  label="O_element : 008"  # scripted group (container) (typed FeaturePython)
  n = 4
  ref = O_element
FEATURE [App::DocumentObjectGroupPython] G4_CADMIUM_TUNGSTATE  # scripted group (container) (typed FeaturePython)
  Dunit = g/cm3
  Dvalue = 7.9
  Group = -> [Cd_element002,W_element001,O_element020]
  conduct = 2
  density = 1
  expand = 3
  formula = G4_CADMIUM_TUNGSTATE
  name = G4_CADMIUM_TUNGSTATE
  specific = 4
FEATURE [App::DocumentObjectGroupPython] Ca_element005  label="Ca_element : 1"  # scripted group (container) (typed FeaturePython)
  n = 1
  ref = Ca_element
FEATURE [App::DocumentObjectGroupPython] C_element022  label="C_element : 009"  # scripted group (container) (typed FeaturePython)
  n = 1
  ref = C_element
FEATURE [App::DocumentObjectGroupPython] O_element021  label="O_element : 009"  # scripted group (container) (typed FeaturePython)
  n = 3
  ref = O_element
FEATURE [App::DocumentObjectGroupPython] G4_CALCIUM_CARBONATE  # scripted group (container) (typed FeaturePython)
  Dunit = g/cm3
  Dvalue = 2.8
  Group = -> [Ca_element005,C_element022,O_element021]
  conduct = 2
  density = 1
  expand = 3
  formula = G4_CALCIUM_CARBONATE
  name = G4_CALCIUM_CARBONATE
  specific = 4
FEATURE [App::DocumentObjectGroupPython] Ca_element006  label="Ca_element : 002"  # scripted group (container) (typed FeaturePython)
  n = 1
  ref = Ca_element
FEATURE [App::DocumentObjectGroupPython] F_element005  label="F_element : 003"  # scripted group (container) (typed FeaturePython)
  n = 2
  ref = F_element
FEATURE [App::DocumentObjectGroupPython] G4_CALCIUM_FLUORIDE  # scripted group (container) (typed FeaturePython)
  Dunit = g/cm3
  Dvalue = 3.18
  Group = -> [Ca_element006,F_element005]
  conduct = 2
  density = 1
  expand = 3
  formula = G4_CALCIUM_FLUORIDE
  name = G4_CALCIUM_FLUORIDE
  specific = 4
FEATURE [App::DocumentObjectGroupPython] Ca_element007  label="Ca_element : 003"  # scripted group (container) (typed FeaturePython)
  n = 1
  ref = Ca_element
FEATURE [App::DocumentObjectGroupPython] O_element022  label="O_element : 010"  # scripted group (container) (typed FeaturePython)
  n = 1
  ref = O_element
FEATURE [App::DocumentObjectGroupPython] G4_CALCIUM_OXIDE  # scripted group (container) (typed FeaturePython)
  Dunit = g/cm3
  Dvalue = 3.3
  Group = -> [Ca_element007,O_element022]
  conduct = 2
  density = 1
  expand = 3
  formula = G4_CALCIUM_OXIDE
  name = G4_CALCIUM_OXIDE
  specific = 4
FEATURE [App::DocumentObjectGroupPython] Ca_element008  label="Ca_element : 004"  # scripted group (container) (typed FeaturePython)
  n = 1
  ref = Ca_element
FEATURE [App::DocumentObjectGroupPython] S_element007  label="S_element : 002"  # scripted group (container) (typed FeaturePython)
  n = 1
  ref = S_element
FEATURE [App::DocumentObjectGroupPython] O_element023  label="O_element : 011"  # scripted group (container) (typed FeaturePython)
  n = 4
  ref = O_element
FEATURE [App::DocumentObjectGroupPython] G4_CALCIUM_SULFATE  # scripted group (container) (typed FeaturePython)
  Dunit = g/cm3
  Dvalue = 2.96
  Group = -> [Ca_element008,S_element007,O_element023]
  conduct = 2
  density = 1
  expand = 3
  formula = G4_CALCIUM_SULFATE
  name = G4_CALCIUM_SULFATE
  specific = 4
FEATURE [App::DocumentObjectGroupPython] Ca_element009  label="Ca_element : 005"  # scripted group (container) (typed FeaturePython)
  n = 1
  ref = Ca_element
FEATURE [App::DocumentObjectGroupPython] W_element002  label="W_element : 002"  # scripted group (container) (typed FeaturePython)
  n = 1
  ref = W_element
FEATURE [App::DocumentObjectGroupPython] O_element024  label="O_element : 012"  # scripted group (container) (typed FeaturePython)
  n = 4
  ref = O_element
FEATURE [App::DocumentObjectGroupPython] G4_CALCIUM_TUNGSTATE  # scripted group (container) (typed FeaturePython)
  Dunit = g/cm3
  Dvalue = 6.062
  Group = -> [Ca_element009,W_element002,O_element024]
  conduct = 2
  density = 1
  expand = 3
  formula = G4_CALCIUM_TUNGSTATE
  name = G4_CALCIUM_TUNGSTATE
  specific = 4
FEATURE [App::DocumentObjectGroupPython] C_element023  label="C_element : 010"  # scripted group (container) (typed FeaturePython)
  n = 1
  ref = C_element
FEATURE [App::DocumentObjectGroupPython] O_element025  label="O_element : 013"  # scripted group (container) (typed FeaturePython)
  n = 2
  ref = O_element
FEATURE [App::DocumentObjectGroupPython] G4_CARBON_DIOXIDE  # scripted group (container) (typed FeaturePython)
  Dunit = g/cm3
  Dvalue = 0.00184212
  Group = -> [C_element023,O_element025]
  conduct = 2
  density = 1
  expand = 3
  formula = G4_CARBON_DIOXIDE
  name = G4_CARBON_DIOXIDE
  specific = 4
FEATURE [App::DocumentObjectGroupPython] C_element024  label="C_element : 011"  # scripted group (container) (typed FeaturePython)
  n = 1
  ref = C_element
FEATURE [App::DocumentObjectGroupPython] Cl_element004  label="Cl_element : 4"  # scripted group (container) (typed FeaturePython)
  n = 4
  ref = Cl_element
FEATURE [App::DocumentObjectGroupPython] G4_CARBON_TETRACHLORIDE  # scripted group (container) (typed FeaturePython)
  Dunit = g/cm3
  Dvalue = 1.594
  Group = -> [C_element024,Cl_element004]
  conduct = 2
  density = 1
  expand = 3
  formula = G4_CARBON_TETRACHLORIDE
  name = G4_CARBON_TETRACHLORIDE
  specific = 4
FEATURE [App::DocumentObjectGroupPython] C_element025  label="C_element : 012"  # scripted group (container) (typed FeaturePython)
  n = 6
  ref = C_element
FEATURE [App::DocumentObjectGroupPython] H_element021  label="H_element : 012"  # scripted group (container) (typed FeaturePython)
  n = 10
  ref = H_element
FEATURE [App::DocumentObjectGroupPython] O_element026  label="O_element : 5"  # scripted group (container) (typed FeaturePython)
  n = 5
  ref = O_element
FEATURE [App::DocumentObjectGroupPython] G4_CELLULOSE_CELLOPHANE  # scripted group (container) (typed FeaturePython)
  Dunit = g/cm3
  Dvalue = 1.42
  Group = -> [C_element025,H_element021,O_element026]
  conduct = 2
  density = 1
  expand = 3
  formula = G4_CELLULOSE_CELLOPHANE
  name = G4_CELLULOSE_CELLOPHANE
  specific = 4
FEATURE [App::DocumentObjectGroupPython] H_element022  label="H_element : 0.067"  # scripted group (container) (typed FeaturePython)
  n = 0.067125
FEATURE [App::DocumentObjectGroupPython] C_element026  label="C_element : 0.545"  # scripted group (container) (typed FeaturePython)
  n = 0.545403
FEATURE [App::DocumentObjectGroupPython] O_element027  label="O_element : 0.387"  # scripted group (container) (typed FeaturePython)
  n = 0.387472
FEATURE [App::DocumentObjectGroupPython] G4_CELLULOSE_BUTYRATE  # scripted group (container) (typed FeaturePython)
  Dunit = g/cm3
  Dvalue = 1.2
  Group = -> [H_element022,C_element026,O_element027]
  conduct = 2
  density = 1
  expand = 3
  formula = G4_CELLULOSE_BUTYRATE
  name = G4_CELLULOSE_BUTYRATE
  specific = 4
FEATURE [App::DocumentObjectGroupPython] H_element023  label="H_element : 0.029"  # scripted group (container) (typed FeaturePython)
  n = 0.029216
FEATURE [App::DocumentObjectGroupPython] C_element027  label="C_element : 0.271"  # scripted group (container) (typed FeaturePython)
  n = 0.271296
FEATURE [App::DocumentObjectGroupPython] N_element013  label="N_element : 0.121"  # scripted group (container) (typed FeaturePython)
  n = 0.121276
FEATURE [App::DocumentObjectGroupPython] O_element028  label="O_element : 0.578"  # scripted group (container) (typed FeaturePython)
  n = 0.578212
FEATURE [App::DocumentObjectGroupPython] G4_CELLULOSE_NITRATE  # scripted group (container) (typed FeaturePython)
  Dunit = g/cm3
  Dvalue = 1.49
  Group = -> [H_element023,C_element027,N_element013,O_element028]
  conduct = 2
  density = 1
  expand = 3
  formula = G4_CELLULOSE_NITRATE
  name = G4_CELLULOSE_NITRATE
  specific = 4
FEATURE [App::DocumentObjectGroupPython] H_element024  label="H_element : 0.108"  # scripted group (container) (typed FeaturePython)
  n = 0.107596
FEATURE [App::DocumentObjectGroupPython] N_element014  label="N_element : 0.001"  # scripted group (container) (typed FeaturePython)
  n = 0.0008
FEATURE [App::DocumentObjectGroupPython] O_element029  label="O_element : 0.875"  # scripted group (container) (typed FeaturePython)
  n = 0.874976
FEATURE [App::DocumentObjectGroupPython] S_element008  label="S_element : 0.015"  # scripted group (container) (typed FeaturePython)
  n = 0.014627
FEATURE [App::DocumentObjectGroupPython] Ce_element001  label="Ce_element : 0.002"  # scripted group (container) (typed FeaturePython)
  n = 0.002001
FEATURE [App::DocumentObjectGroupPython] G4_CERIC_SULFATE  # scripted group (container) (typed FeaturePython)
  Dunit = g/cm3
  Dvalue = 1.03
  Group = -> [H_element024,N_element014,O_element029,S_element008,Ce_element001]
  conduct = 2
  density = 1
  expand = 3
  formula = G4_CERIC_SULFATE
  name = G4_CERIC_SULFATE
  specific = 4
FEATURE [App::DocumentObjectGroupPython] Cs_element001  label="Cs_element : 1"  # scripted group (container) (typed FeaturePython)
  n = 1
  ref = Cs_element
FEATURE [App::DocumentObjectGroupPython] F_element006  label="F_element : 1"  # scripted group (container) (typed FeaturePython)
  n = 1
  ref = F_element
FEATURE [App::DocumentObjectGroupPython] G4_CESIUM_FLUORIDE  # scripted group (container) (typed FeaturePython)
  Dunit = g/cm3
  Dvalue = 4.115
  Group = -> [Cs_element001,F_element006]
  conduct = 2
  density = 1
  expand = 3
  formula = G4_CESIUM_FLUORIDE
  name = G4_CESIUM_FLUORIDE
  specific = 4
FEATURE [App::DocumentObjectGroupPython] Cs_element002  label="Cs_element : 002"  # scripted group (container) (typed FeaturePython)
  n = 1
  ref = Cs_element
FEATURE [App::DocumentObjectGroupPython] I_element001  label="I_element : 1"  # scripted group (container) (typed FeaturePython)
  n = 1
  ref = I_element
FEATURE [App::DocumentObjectGroupPython] G4_CESIUM_IODIDE  # scripted group (container) (typed FeaturePython)
  Dunit = g/cm3
  Dvalue = 4.51
  Group = -> [Cs_element002,I_element001]
  conduct = 2
  density = 1
  expand = 3
  formula = G4_CESIUM_IODIDE
  name = G4_CESIUM_IODIDE
  specific = 4
FEATURE [App::DocumentObjectGroupPython] C_element028  label="C_element : 013"  # scripted group (container) (typed FeaturePython)
  n = 6
  ref = C_element
FEATURE [App::DocumentObjectGroupPython] H_element025  label="H_element : 013"  # scripted group (container) (typed FeaturePython)
  n = 5
  ref = H_element
FEATURE [App::DocumentObjectGroupPython] Cl_element005  label="Cl_element : 1"  # scripted group (container) (typed FeaturePython)
  n = 1
  ref = Cl_element
FEATURE [App::DocumentObjectGroupPython] G4_CHLOROBENZENE  # scripted group (container) (typed FeaturePython)
  Dunit = g/cm3
  Dvalue = 1.1058
  Group = -> [C_element028,H_element025,Cl_element005]
  conduct = 2
  density = 1
  expand = 3
  formula = G4_CHLOROBENZENE
  name = G4_CHLOROBENZENE
  specific = 4
FEATURE [App::DocumentObjectGroupPython] C_element029  label="C_element : 014"  # scripted group (container) (typed FeaturePython)
  n = 1
  ref = C_element
FEATURE [App::DocumentObjectGroupPython] H_element026  label="H_element : 1"  # scripted group (container) (typed FeaturePython)
  n = 1
  ref = H_element
FEATURE [App::DocumentObjectGroupPython] Cl_element006  label="Cl_element : 3"  # scripted group (container) (typed FeaturePython)
  n = 3
  ref = Cl_element
FEATURE [App::DocumentObjectGroupPython] G4_CHLOROFORM  # scripted group (container) (typed FeaturePython)
  Dunit = g/cm3
  Dvalue = 1.4832
  Group = -> [C_element029,H_element026,Cl_element006]
  conduct = 2
  density = 1
  expand = 3
  formula = G4_CHLOROFORM
  name = G4_CHLOROFORM
  specific = 4
FEATURE [App::DocumentObjectGroupPython] H_element027  label="H_element : 0.010"  # scripted group (container) (typed FeaturePython)
  n = 0.01
FEATURE [App::DocumentObjectGroupPython] C_element030  label="C_element : 0.001"  # scripted group (container) (typed FeaturePython)
  n = 0.001
FEATURE [App::DocumentObjectGroupPython] O_element030  label="O_element : 0.529"  # scripted group (container) (typed FeaturePython)
  n = 0.529107
FEATURE [App::DocumentObjectGroupPython] Na_element005  label="Na_element : 0.016"  # scripted group (container) (typed FeaturePython)
  n = 0.016
FEATURE [App::DocumentObjectGroupPython] Mg_element003  label="Mg_element : 0.004"  # scripted group (container) (typed FeaturePython)
  n = 0.002
FEATURE [App::DocumentObjectGroupPython] Al_element002  label="Al_element : 0.034"  # scripted group (container) (typed FeaturePython)
  n = 0.033872
FEATURE [App::DocumentObjectGroupPython] Si_element002  label="Si_element : 0.337"  # scripted group (container) (typed FeaturePython)
  n = 0.337021
FEATURE [App::DocumentObjectGroupPython] K_element003  label="K_element : 0.013"  # scripted group (container) (typed FeaturePython)
  n = 0.013
FEATURE [App::DocumentObjectGroupPython] Ca_element010  label="Ca_element : 0.044"  # scripted group (container) (typed FeaturePython)
  n = 0.044
FEATURE [App::DocumentObjectGroupPython] Fe_element002  label="Fe_element : 0.014"  # scripted group (container) (typed FeaturePython)
  n = 0.014
FEATURE [App::DocumentObjectGroupPython] G4_CONCRETE  # scripted group (container) (typed FeaturePython)
  Dunit = g/cm3
  Dvalue = 2.3
  Group = -> [H_element027,C_element030,O_element030,Na_element005,Mg_element003,Al_element002,Si_element002,K_element003,Ca_element010,Fe_element002]
  conduct = 2
  density = 1
  expand = 3
  formula = G4_CONCRETE
  name = G4_CONCRETE
  specific = 4
FEATURE [App::DocumentObjectGroupPython] C_element031  label="C_element : 015"  # scripted group (container) (typed FeaturePython)
  n = 6
  ref = C_element
FEATURE [App::DocumentObjectGroupPython] H_element028  label="H_element : 12"  # scripted group (container) (typed FeaturePython)
  n = 12
  ref = H_element
FEATURE [App::DocumentObjectGroupPython] G4_CYCLOHEXANE  # scripted group (container) (typed FeaturePython)
  Dunit = g/cm3
  Dvalue = 0.779
  Group = -> [C_element031,H_element028]
  conduct = 2
  density = 1
  expand = 3
  formula = G4_CYCLOHEXANE
  name = G4_CYCLOHEXANE
  specific = 4
FEATURE [App::DocumentObjectGroupPython] C_element032  label="C_element : 016"  # scripted group (container) (typed FeaturePython)
  n = 6
  ref = C_element
FEATURE [App::DocumentObjectGroupPython] H_element029  label="H_element : 4"  # scripted group (container) (typed FeaturePython)
  n = 4
  ref = H_element
FEATURE [App::DocumentObjectGroupPython] Cl_element007  label="Cl_element : 2"  # scripted group (container) (typed FeaturePython)
  n = 2
  ref = Cl_element
FEATURE [App::DocumentObjectGroupPython] G4_1_2_DICHLOROBENZENE  label="G4_1.2-DICHLOROBENZENE"  # scripted group (container) (typed FeaturePython)
  Dunit = g/cm3
  Dvalue = 1.3048
  Group = -> [C_element032,H_element029,Cl_element007]
  conduct = 2
  density = 1
  expand = 3
  formula = G4_1.2-DICHLOROBENZENE
  name = G4_1.2-DICHLOROBENZENE
  specific = 4
FEATURE [App::DocumentObjectGroupPython] C_element033  label="C_element : 017"  # scripted group (container) (typed FeaturePython)
  n = 4
  ref = C_element
FEATURE [App::DocumentObjectGroupPython] H_element030  label="H_element : 8"  # scripted group (container) (typed FeaturePython)
  n = 8
  ref = H_element
FEATURE [App::DocumentObjectGroupPython] O_element031  label="O_element : 014"  # scripted group (container) (typed FeaturePython)
  n = 1
  ref = O_element
FEATURE [App::DocumentObjectGroupPython] Cl_element008  label="Cl_element : 005"  # scripted group (container) (typed FeaturePython)
  n = 2
  ref = Cl_element
FEATURE [App::DocumentObjectGroupPython] G4_DICHLORODIETHYL_ETHER  # scripted group (container) (typed FeaturePython)
  Dunit = g/cm3
  Dvalue = 1.2199
  Group = -> [C_element033,H_element030,O_element031,Cl_element008]
  conduct = 2
  density = 1
  expand = 3
  formula = G4_DICHLORODIETHYL_ETHER
  name = G4_DICHLORODIETHYL_ETHER
  specific = 4
FEATURE [App::DocumentObjectGroupPython] C_element034  label="C_element : 018"  # scripted group (container) (typed FeaturePython)
  n = 2
  ref = C_element
FEATURE [App::DocumentObjectGroupPython] H_element031  label="H_element : 014"  # scripted group (container) (typed FeaturePython)
  n = 4
  ref = H_element
FEATURE [App::DocumentObjectGroupPython] Cl_element009  label="Cl_element : 006"  # scripted group (container) (typed FeaturePython)
  n = 2
  ref = Cl_element
FEATURE [App::DocumentObjectGroupPython] G4_1_2_DICHLOROETHANE  label="G4_1.2-DICHLOROETHANE"  # scripted group (container) (typed FeaturePython)
  Dunit = g/cm3
  Dvalue = 1.2351
  Group = -> [C_element034,H_element031,Cl_element009]
  conduct = 2
  density = 1
  expand = 3
  formula = G4_1.2-DICHLOROETHANE
  name = G4_1.2-DICHLOROETHANE
  specific = 4
FEATURE [App::DocumentObjectGroupPython] C_element035  label="C_element : 019"  # scripted group (container) (typed FeaturePython)
  n = 4
  ref = C_element
FEATURE [App::DocumentObjectGroupPython] H_element032  label="H_element : 015"  # scripted group (container) (typed FeaturePython)
  n = 10
  ref = H_element
FEATURE [App::DocumentObjectGroupPython] O_element032  label="O_element : 015"  # scripted group (container) (typed FeaturePython)
  n = 1
  ref = O_element
FEATURE [App::DocumentObjectGroupPython] G4_DIETHYL_ETHER  # scripted group (container) (typed FeaturePython)
  Dunit = g/cm3
  Dvalue = 0.71378
  Group = -> [C_element035,H_element032,O_element032]
  conduct = 2
  density = 1
  expand = 3
  formula = G4_DIETHYL_ETHER
  name = G4_DIETHYL_ETHER
  specific = 4
FEATURE [App::DocumentObjectGroupPython] C_element036  label="C_element : 020"  # scripted group (container) (typed FeaturePython)
  n = 3
  ref = C_element
FEATURE [App::DocumentObjectGroupPython] H_element033  label="H_element : 016"  # scripted group (container) (typed FeaturePython)
  n = 7
  ref = H_element
FEATURE [App::DocumentObjectGroupPython] N_element015  label="N_element : 008"  # scripted group (container) (typed FeaturePython)
  n = 1
  ref = N_element
FEATURE [App::DocumentObjectGroupPython] O_element033  label="O_element : 016"  # scripted group (container) (typed FeaturePython)
  n = 1
  ref = O_element
FEATURE [App::DocumentObjectGroupPython] G4_N_N_DIMETHYL_FORMAMIDE  label="G4_N.N-DIMETHYL_FORMAMIDE"  # scripted group (container) (typed FeaturePython)
  Dunit = g/cm3
  Dvalue = 0.9487
  Group = -> [C_element036,H_element033,N_element015,O_element033]
  conduct = 2
  density = 1
  expand = 3
  formula = G4_N.N-DIMETHYL_FORMAMIDE
  name = G4_N.N-DIMETHYL_FORMAMIDE
  specific = 4
FEATURE [App::DocumentObjectGroupPython] C_element037  label="C_element : 021"  # scripted group (container) (typed FeaturePython)
  n = 2
  ref = C_element
FEATURE [App::DocumentObjectGroupPython] H_element034  label="H_element : 017"  # scripted group (container) (typed FeaturePython)
  n = 6
  ref = H_element
FEATURE [App::DocumentObjectGroupPython] O_element034  label="O_element : 017"  # scripted group (container) (typed FeaturePython)
  n = 1
  ref = O_element
FEATURE [App::DocumentObjectGroupPython] S_element009  label="S_element : 003"  # scripted group (container) (typed FeaturePython)
  n = 1
  ref = S_element
FEATURE [App::DocumentObjectGroupPython] G4_DIMETHYL_SULFOXIDE  # scripted group (container) (typed FeaturePython)
  Dunit = g/cm3
  Dvalue = 1.1014
  Group = -> [C_element037,H_element034,O_element034,S_element009]
  conduct = 2
  density = 1
  expand = 3
  formula = G4_DIMETHYL_SULFOXIDE
  name = G4_DIMETHYL_SULFOXIDE
  specific = 4
FEATURE [App::DocumentObjectGroupPython] C_element038  label="C_element : 022"  # scripted group (container) (typed FeaturePython)
  n = 2
  ref = C_element
FEATURE [App::DocumentObjectGroupPython] H_element035  label="H_element : 018"  # scripted group (container) (typed FeaturePython)
  n = 6
  ref = H_element
FEATURE [App::DocumentObjectGroupPython] G4_ETHANE  # scripted group (container) (typed FeaturePython)
  Dunit = g/cm3
  Dvalue = 0.00125324
  Group = -> [C_element038,H_element035]
  conduct = 2
  density = 1
  expand = 3
  formula = G4_ETHANE
  name = G4_ETHANE
  specific = 4
FEATURE [App::DocumentObjectGroupPython] C_element039  label="C_element : 023"  # scripted group (container) (typed FeaturePython)
  n = 2
  ref = C_element
FEATURE [App::DocumentObjectGroupPython] H_element036  label="H_element : 019"  # scripted group (container) (typed FeaturePython)
  n = 6
  ref = H_element
FEATURE [App::DocumentObjectGroupPython] O_element035  label="O_element : 018"  # scripted group (container) (typed FeaturePython)
  n = 1
  ref = O_element
FEATURE [App::DocumentObjectGroupPython] G4_ETHYL_ALCOHOL  # scripted group (container) (typed FeaturePython)
  Dunit = g/cm3
  Dvalue = 0.7893
  Group = -> [C_element039,H_element036,O_element035]
  conduct = 2
  density = 1
  expand = 3
  formula = G4_ETHYL_ALCOHOL
  name = G4_ETHYL_ALCOHOL
  specific = 4
FEATURE [App::DocumentObjectGroupPython] H_element037  label="H_element : 0.090"  # scripted group (container) (typed FeaturePython)
  n = 0.090027
FEATURE [App::DocumentObjectGroupPython] C_element040  label="C_element : 0.585"  # scripted group (container) (typed FeaturePython)
  n = 0.585182
FEATURE [App::DocumentObjectGroupPython] O_element036  label="O_element : 0.325"  # scripted group (container) (typed FeaturePython)
  n = 0.324791
FEATURE [App::DocumentObjectGroupPython] G4_ETHYL_CELLULOSE  # scripted group (container) (typed FeaturePython)
  Dunit = g/cm3
  Dvalue = 1.13
  Group = -> [H_element037,C_element040,O_element036]
  conduct = 2
  density = 1
  expand = 3
  formula = G4_ETHYL_CELLULOSE
  name = G4_ETHYL_CELLULOSE
  specific = 4
FEATURE [App::DocumentObjectGroupPython] C_element041  label="C_element : 024"  # scripted group (container) (typed FeaturePython)
  n = 2
  ref = C_element
FEATURE [App::DocumentObjectGroupPython] H_element038  label="H_element : 020"  # scripted group (container) (typed FeaturePython)
  n = 4
  ref = H_element
FEATURE [App::DocumentObjectGroupPython] G4_ETHYLENE  # scripted group (container) (typed FeaturePython)
  Dunit = g/cm3
  Dvalue = 0.00117497
  Group = -> [C_element041,H_element038]
  conduct = 2
  density = 1
  expand = 3
  formula = G4_ETHYLENE
  name = G4_ETHYLENE
  specific = 4
FEATURE [App::DocumentObjectGroupPython] H_element039  label="H_element : 0.096"  # scripted group (container) (typed FeaturePython)
  n = 0.096
FEATURE [App::DocumentObjectGroupPython] C_element042  label="C_element : 0.195"  # scripted group (container) (typed FeaturePython)
  n = 0.195
FEATURE [App::DocumentObjectGroupPython] N_element016  label="N_element : 0.057"  # scripted group (container) (typed FeaturePython)
  n = 0.057
FEATURE [App::DocumentObjectGroupPython] O_element037  label="O_element : 0.646"  # scripted group (container) (typed FeaturePython)
  n = 0.646
FEATURE [App::DocumentObjectGroupPython] Na_element006  label="Na_element : 0.017"  # scripted group (container) (typed FeaturePython)
  n = 0.001
FEATURE [App::DocumentObjectGroupPython] P_element005  label="P_element : 0.104"  # scripted group (container) (typed FeaturePython)
  n = 0.001
FEATURE [App::DocumentObjectGroupPython] S_element010  label="S_element : 0.016"  # scripted group (container) (typed FeaturePython)
  n = 0.003
FEATURE [App::DocumentObjectGroupPython] Cl_element010  label="Cl_element : 0.005"  # scripted group (container) (typed FeaturePython)
  n = 0.001
FEATURE [App::DocumentObjectGroupPython] G4_EYE_LENS_ICRP  # scripted group (container) (typed FeaturePython)
  Dunit = g/cm3
  Dvalue = 1.07
  Group = -> [H_element039,C_element042,N_element016,O_element037,Na_element006,P_element005,S_element010,Cl_element010]
  conduct = 2
  density = 1
  expand = 3
  formula = G4_EYE_LENS_ICRP
  name = G4_EYE_LENS_ICRP
  specific = 4
FEATURE [App::DocumentObjectGroupPython] Fe_element003  label="Fe_element : 2"  # scripted group (container) (typed FeaturePython)
  n = 2
  ref = Fe_element
FEATURE [App::DocumentObjectGroupPython] O_element038  label="O_element : 019"  # scripted group (container) (typed FeaturePython)
  n = 3
  ref = O_element
FEATURE [App::DocumentObjectGroupPython] G4_FERRIC_OXIDE  # scripted group (container) (typed FeaturePython)
  Dunit = g/cm3
  Dvalue = 5.2
  Group = -> [Fe_element003,O_element038]
  conduct = 2
  density = 1
  expand = 3
  formula = G4_FERRIC_OXIDE
  name = G4_FERRIC_OXIDE
  specific = 4
FEATURE [App::DocumentObjectGroupPython] Fe_element004  label="Fe_element : 1"  # scripted group (container) (typed FeaturePython)
  n = 1
  ref = Fe_element
FEATURE [App::DocumentObjectGroupPython] B_element003  label="B_element : 1"  # scripted group (container) (typed FeaturePython)
  n = 1
  ref = B_element
FEATURE [App::DocumentObjectGroupPython] G4_FERROBORIDE  # scripted group (container) (typed FeaturePython)
  Dunit = g/cm3
  Dvalue = 7.15
  Group = -> [Fe_element004,B_element003]
  conduct = 2
  density = 1
  expand = 3
  formula = G4_FERROBORIDE
  name = G4_FERROBORIDE
  specific = 4
FEATURE [App::DocumentObjectGroupPython] Fe_element005  label="Fe_element : 003"  # scripted group (container) (typed FeaturePython)
  n = 1
  ref = Fe_element
FEATURE [App::DocumentObjectGroupPython] O_element039  label="O_element : 020"  # scripted group (container) (typed FeaturePython)
  n = 1
  ref = O_element
FEATURE [App::DocumentObjectGroupPython] G4_FERROUS_OXIDE  # scripted group (container) (typed FeaturePython)
  Dunit = g/cm3
  Dvalue = 5.7
  Group = -> [Fe_element005,O_element039]
  conduct = 2
  density = 1
  expand = 3
  formula = G4_FERROUS_OXIDE
  name = G4_FERROUS_OXIDE
  specific = 4
FEATURE [App::DocumentObjectGroupPython] H_element040  label="H_element : 0.115"  # scripted group (container) (typed FeaturePython)
  n = 0.108259
FEATURE [App::DocumentObjectGroupPython] N_element017  label="N_element : 0.000"  # scripted group (container) (typed FeaturePython)
  n = 2.7e-05
FEATURE [App::DocumentObjectGroupPython] O_element040  label="O_element : 0.879"  # scripted group (container) (typed FeaturePython)
  n = 0.878636
FEATURE [App::DocumentObjectGroupPython] Na_element007  label="Na_element : 0.000"  # scripted group (container) (typed FeaturePython)
  n = 2.2e-05
FEATURE [App::DocumentObjectGroupPython] S_element011  label="S_element : 0.013"  # scripted group (container) (typed FeaturePython)
  n = 0.012968
FEATURE [App::DocumentObjectGroupPython] Cl_element011  label="Cl_element : 0.000"  # scripted group (container) (typed FeaturePython)
  n = 3.4e-05
FEATURE [App::DocumentObjectGroupPython] Fe_element006  label="Fe_element : 0.000"  # scripted group (container) (typed FeaturePython)
  n = 5.4e-05
FEATURE [App::DocumentObjectGroupPython] G4_FERROUS_SULFATE  # scripted group (container) (typed FeaturePython)
  Dunit = g/cm3
  Dvalue = 1.024
  Group = -> [H_element040,N_element017,O_element040,Na_element007,S_element011,Cl_element011,Fe_element006]
  conduct = 2
  density = 1
  expand = 3
  formula = G4_FERROUS_SULFATE
  name = G4_FERROUS_SULFATE
  specific = 4
FEATURE [App::DocumentObjectGroupPython] C_element043  label="C_element : 0.099"  # scripted group (container) (typed FeaturePython)
  n = 0.099335
FEATURE [App::DocumentObjectGroupPython] F_element007  label="F_element : 0.314"  # scripted group (container) (typed FeaturePython)
  n = 0.314247
FEATURE [App::DocumentObjectGroupPython] Cl_element012  label="Cl_element : 0.586"  # scripted group (container) (typed FeaturePython)
  n = 0.586418
FEATURE [App::DocumentObjectGroupPython] G4_FREON_12  label="G4_FREON-12"  # scripted group (container) (typed FeaturePython)
  Dunit = g/cm3
  Dvalue = 1.12
  Group = -> [C_element043,F_element007,Cl_element012]
  conduct = 2
  density = 1
  expand = 3
  formula = G4_FREON-12
  name = G4_FREON-12
  specific = 4
FEATURE [App::DocumentObjectGroupPython] C_element044  label="C_element : 0.057"  # scripted group (container) (typed FeaturePython)
  n = 0.057245
FEATURE [App::DocumentObjectGroupPython] F_element008  label="F_element : 0.181"  # scripted group (container) (typed FeaturePython)
  n = 0.181096
FEATURE [App::DocumentObjectGroupPython] Br_element001  label="Br_element : 0.762"  # scripted group (container) (typed FeaturePython)
  n = 0.761659
FEATURE [App::DocumentObjectGroupPython] G4_FREON_12B2  label="G4_FREON-12B2"  # scripted group (container) (typed FeaturePython)
  Dunit = g/cm3
  Dvalue = 1.8
  Group = -> [C_element044,F_element008,Br_element001]
  conduct = 2
  density = 1
  expand = 3
  formula = G4_FREON-12B2
  name = G4_FREON-12B2
  specific = 4
FEATURE [App::DocumentObjectGroupPython] C_element045  label="C_element : 0.115"  # scripted group (container) (typed FeaturePython)
  n = 0.114983
FEATURE [App::DocumentObjectGroupPython] F_element009  label="F_element : 0.546"  # scripted group (container) (typed FeaturePython)
  n = 0.545621
FEATURE [App::DocumentObjectGroupPython] Cl_element013  label="Cl_element : 0.339"  # scripted group (container) (typed FeaturePython)
  n = 0.339396
FEATURE [App::DocumentObjectGroupPython] G4_FREON_13  label="G4_FREON-13"  # scripted group (container) (typed FeaturePython)
  Dunit = g/cm3
  Dvalue = 0.95
  Group = -> [C_element045,F_element009,Cl_element013]
  conduct = 2
  density = 1
  expand = 3
  formula = G4_FREON-13
  name = G4_FREON-13
  specific = 4
FEATURE [App::DocumentObjectGroupPython] C_element046  label="C_element : 025"  # scripted group (container) (typed FeaturePython)
  n = 1
  ref = C_element
FEATURE [App::DocumentObjectGroupPython] F_element010  label="F_element : 3"  # scripted group (container) (typed FeaturePython)
  n = 3
  ref = F_element
FEATURE [App::DocumentObjectGroupPython] Br_element002  label="Br_element : 1"  # scripted group (container) (typed FeaturePython)
  n = 1
  ref = Br_element
FEATURE [App::DocumentObjectGroupPython] G4_FREON_13B1  label="G4_FREON-13B1"  # scripted group (container) (typed FeaturePython)
  Dunit = g/cm3
  Dvalue = 1.5
  Group = -> [C_element046,F_element010,Br_element002]
  conduct = 2
  density = 1
  expand = 3
  formula = G4_FREON-13B1
  name = G4_FREON-13B1
  specific = 4
FEATURE [App::DocumentObjectGroupPython] C_element047  label="C_element : 0.061"  # scripted group (container) (typed FeaturePython)
  n = 0.061309
FEATURE [App::DocumentObjectGroupPython] F_element011  label="F_element : 0.291"  # scripted group (container) (typed FeaturePython)
  n = 0.290924
FEATURE [App::DocumentObjectGroupPython] I_element002  label="I_element : 0.648"  # scripted group (container) (typed FeaturePython)
  n = 0.647767
FEATURE [App::DocumentObjectGroupPython] G4_FREON_13I1  label="G4_FREON-13I1"  # scripted group (container) (typed FeaturePython)
  Dunit = g/cm3
  Dvalue = 1.8
  Group = -> [C_element047,F_element011,I_element002]
  conduct = 2
  density = 1
  expand = 3
  formula = G4_FREON-13I1
  name = G4_FREON-13I1
  specific = 4
FEATURE [App::DocumentObjectGroupPython] Gd_element001  label="Gd_element : 2"  # scripted group (container) (typed FeaturePython)
  n = 2
  ref = Gd_element
FEATURE [App::DocumentObjectGroupPython] O_element041  label="O_element : 021"  # scripted group (container) (typed FeaturePython)
  n = 2
  ref = O_element
FEATURE [App::DocumentObjectGroupPython] S_element012  label="S_element : 004"  # scripted group (container) (typed FeaturePython)
  n = 1
  ref = S_element
FEATURE [App::DocumentObjectGroupPython] G4_GADOLINIUM_OXYSULFIDE  # scripted group (container) (typed FeaturePython)
  Dunit = g/cm3
  Dvalue = 7.44
  Group = -> [Gd_element001,O_element041,S_element012]
  conduct = 2
  density = 1
  expand = 3
  formula = G4_GADOLINIUM_OXYSULFIDE
  name = G4_GADOLINIUM_OXYSULFIDE
  specific = 4
FEATURE [App::DocumentObjectGroupPython] Ga_element001  label="Ga_element : 1"  # scripted group (container) (typed FeaturePython)
  n = 1
  ref = Ga_element
FEATURE [App::DocumentObjectGroupPython] As_element001  label="As_element : 1"  # scripted group (container) (typed FeaturePython)
  n = 1
  ref = As_element
FEATURE [App::DocumentObjectGroupPython] G4_GALLIUM_ARSENIDE  # scripted group (container) (typed FeaturePython)
  Dunit = g/cm3
  Dvalue = 5.31
  Group = -> [Ga_element001,As_element001]
  conduct = 2
  density = 1
  expand = 3
  formula = G4_GALLIUM_ARSENIDE
  name = G4_GALLIUM_ARSENIDE
  specific = 4
FEATURE [App::DocumentObjectGroupPython] H_element041  label="H_element : 0.081"  # scripted group (container) (typed FeaturePython)
  n = 0.08118
FEATURE [App::DocumentObjectGroupPython] C_element048  label="C_element : 0.416"  # scripted group (container) (typed FeaturePython)
  n = 0.41606
FEATURE [App::DocumentObjectGroupPython] N_element018  label="N_element : 0.111"  # scripted group (container) (typed FeaturePython)
  n = 0.11124
FEATURE [App::DocumentObjectGroupPython] O_element042  label="O_element : 0.381"  # scripted group (container) (typed FeaturePython)
  n = 0.38064
FEATURE [App::DocumentObjectGroupPython] S_element013  label="S_element : 0.011"  # scripted group (container) (typed FeaturePython)
  n = 0.01088
FEATURE [App::DocumentObjectGroupPython] G4_GEL_PHOTO_EMULSION  # scripted group (container) (typed FeaturePython)
  Dunit = g/cm3
  Dvalue = 1.2914
  Group = -> [H_element041,C_element048,N_element018,O_element042,S_element013]
  conduct = 2
  density = 1
  expand = 3
  formula = G4_GEL_PHOTO_EMULSION
  name = G4_GEL_PHOTO_EMULSION
  specific = 4
FEATURE [App::DocumentObjectGroupPython] B_element004  label="B_element : 0.040"  # scripted group (container) (typed FeaturePython)
  n = 0.0400639
FEATURE [App::DocumentObjectGroupPython] O_element043  label="O_element : 0.540"  # scripted group (container) (typed FeaturePython)
  n = 0.539561
FEATURE [App::DocumentObjectGroupPython] Na_element008  label="Na_element : 0.028"  # scripted group (container) (typed FeaturePython)
  n = 0.0281909
FEATURE [App::DocumentObjectGroupPython] Al_element003  label="Al_element : 0.012"  # scripted group (container) (typed FeaturePython)
  n = 0.011644
FEATURE [App::DocumentObjectGroupPython] Si_element003  label="Si_element : 0.377"  # scripted group (container) (typed FeaturePython)
  n = 0.377219
FEATURE [App::DocumentObjectGroupPython] K_element004  label="K_element : 0.014"  # scripted group (container) (typed FeaturePython)
  n = 0.00332099
FEATURE [App::DocumentObjectGroupPython] G4_Pyrex_Glass  # scripted group (container) (typed FeaturePython)
  Dunit = g/cm3
  Dvalue = 2.23
  Group = -> [B_element004,O_element043,Na_element008,Al_element003,Si_element003,K_element004]
  conduct = 2
  density = 1
  expand = 3
  formula = G4_Pyrex_Glass
  name = G4_Pyrex_Glass
  specific = 4
FEATURE [App::DocumentObjectGroupPython] O_element044  label="O_element : 0.156"  # scripted group (container) (typed FeaturePython)
  n = 0.156453
FEATURE [App::DocumentObjectGroupPython] Si_element004  label="Si_element : 0.081"  # scripted group (container) (typed FeaturePython)
  n = 0.080866
FEATURE [App::DocumentObjectGroupPython] Ti_element001  label="Ti_element : 0.008"  # scripted group (container) (typed FeaturePython)
  n = 0.008092
FEATURE [App::DocumentObjectGroupPython] As_element002  label="As_element : 0.003"  # scripted group (container) (typed FeaturePython)
  n = 0.002651
FEATURE [App::DocumentObjectGroupPython] Pb_element001  label="Pb_element : 0.752"  # scripted group (container) (typed FeaturePython)
  n = 0.751938
FEATURE [App::DocumentObjectGroupPython] G4_GLASS_LEAD  # scripted group (container) (typed FeaturePython)
  Dunit = g/cm3
  Dvalue = 6.22
  Group = -> [O_element044,Si_element004,Ti_element001,As_element002,Pb_element001]
  conduct = 2
  density = 1
  expand = 3
  formula = G4_GLASS_LEAD
  name = G4_GLASS_LEAD
  specific = 4
FEATURE [App::DocumentObjectGroupPython] O_element045  label="O_element : 0.460"  # scripted group (container) (typed FeaturePython)
  n = 0.4598
FEATURE [App::DocumentObjectGroupPython] Na_element009  label="Na_element : 0.096"  # scripted group (container) (typed FeaturePython)
  n = 0.0964411
FEATURE [App::DocumentObjectGroupPython] Si_element005  label="Si_element : 0.378"  # scripted group (container) (typed FeaturePython)
  n = 0.336553
FEATURE [App::DocumentObjectGroupPython] Ca_element011  label="Ca_element : 0.107"  # scripted group (container) (typed FeaturePython)
  n = 0.107205
FEATURE [App::DocumentObjectGroupPython] G4_GLASS_PLATE  # scripted group (container) (typed FeaturePython)
  Dunit = g/cm3
  Dvalue = 2.4
  Group = -> [O_element045,Na_element009,Si_element005,Ca_element011]
  conduct = 2
  density = 1
  expand = 3
  formula = G4_GLASS_PLATE
  name = G4_GLASS_PLATE
  specific = 4
FEATURE [App::DocumentObjectGroupPython] C_element049  label="C_element : 026"  # scripted group (container) (typed FeaturePython)
  n = 5
  ref = C_element
FEATURE [App::DocumentObjectGroupPython] H_element042  label="H_element : 021"  # scripted group (container) (typed FeaturePython)
  n = 10
  ref = H_element
FEATURE [App::DocumentObjectGroupPython] N_element019  label="N_element : 2"  # scripted group (container) (typed FeaturePython)
  n = 2
  ref = N_element
FEATURE [App::DocumentObjectGroupPython] O_element046  label="O_element : 022"  # scripted group (container) (typed FeaturePython)
  n = 3
  ref = O_element
FEATURE [App::DocumentObjectGroupPython] G4_GLUTAMINE  # scripted group (container) (typed FeaturePython)
  Dunit = g/cm3
  Dvalue = 1.46
  Group = -> [C_element049,H_element042,N_element019,O_element046]
  conduct = 2
  density = 1
  expand = 3
  formula = G4_GLUTAMINE
  name = G4_GLUTAMINE
  specific = 4
FEATURE [App::DocumentObjectGroupPython] C_element050  label="C_element : 027"  # scripted group (container) (typed FeaturePython)
  n = 3
  ref = C_element
FEATURE [App::DocumentObjectGroupPython] H_element043  label="H_element : 022"  # scripted group (container) (typed FeaturePython)
  n = 8
  ref = H_element
FEATURE [App::DocumentObjectGroupPython] O_element047  label="O_element : 023"  # scripted group (container) (typed FeaturePython)
  n = 3
  ref = O_element
FEATURE [App::DocumentObjectGroupPython] G4_GLYCEROL  # scripted group (container) (typed FeaturePython)
  Dunit = g/cm3
  Dvalue = 1.2613
  Group = -> [C_element050,H_element043,O_element047]
  conduct = 2
  density = 1
  expand = 3
  formula = G4_GLYCEROL
  name = G4_GLYCEROL
  specific = 4
FEATURE [App::DocumentObjectGroupPython] C_element051  label="C_element : 028"  # scripted group (container) (typed FeaturePython)
  n = 5
  ref = C_element
FEATURE [App::DocumentObjectGroupPython] H_element044  label="H_element : 023"  # scripted group (container) (typed FeaturePython)
  n = 5
  ref = H_element
FEATURE [App::DocumentObjectGroupPython] N_element020  label="N_element : 009"  # scripted group (container) (typed FeaturePython)
  n = 5
  ref = N_element
FEATURE [App::DocumentObjectGroupPython] O_element048  label="O_element : 024"  # scripted group (container) (typed FeaturePython)
  n = 1
  ref = O_element
FEATURE [App::DocumentObjectGroupPython] G4_GUANINE  # scripted group (container) (typed FeaturePython)
  Dunit = g/cm3
  Dvalue = 2.2
  Group = -> [C_element051,H_element044,N_element020,O_element048]
  conduct = 2
  density = 1
  expand = 3
  formula = G4_GUANINE
  name = G4_GUANINE
  specific = 4
FEATURE [App::DocumentObjectGroupPython] Ca_element012  label="Ca_element : 006"  # scripted group (container) (typed FeaturePython)
  n = 1
  ref = Ca_element
FEATURE [App::DocumentObjectGroupPython] S_element014  label="S_element : 005"  # scripted group (container) (typed FeaturePython)
  n = 1
  ref = S_element
FEATURE [App::DocumentObjectGroupPython] O_element049  label="O_element : 6"  # scripted group (container) (typed FeaturePython)
  n = 6
  ref = O_element
FEATURE [App::DocumentObjectGroupPython] H_element045  label="H_element : 024"  # scripted group (container) (typed FeaturePython)
  n = 4
  ref = H_element
FEATURE [App::DocumentObjectGroupPython] G4_GYPSUM  # scripted group (container) (typed FeaturePython)
  Dunit = g/cm3
  Dvalue = 2.32
  Group = -> [Ca_element012,S_element014,O_element049,H_element045]
  conduct = 2
  density = 1
  expand = 3
  formula = G4_GYPSUM
  name = G4_GYPSUM
  specific = 4
FEATURE [App::DocumentObjectGroupPython] C_element052  label="C_element : 7"  # scripted group (container) (typed FeaturePython)
  n = 7
  ref = C_element
FEATURE [App::DocumentObjectGroupPython] H_element046  label="H_element : 16"  # scripted group (container) (typed FeaturePython)
  n = 16
  ref = H_element
FEATURE [App::DocumentObjectGroupPython] G4_N_HEPTANE  label="G4_N-HEPTANE"  # scripted group (container) (typed FeaturePython)
  Dunit = g/cm3
  Dvalue = 0.68376
  Group = -> [C_element052,H_element046]
  conduct = 2
  density = 1
  expand = 3
  formula = G4_N-HEPTANE
  name = G4_N-HEPTANE
  specific = 4
FEATURE [App::DocumentObjectGroupPython] C_element053  label="C_element : 029"  # scripted group (container) (typed FeaturePython)
  n = 6
  ref = C_element
FEATURE [App::DocumentObjectGroupPython] H_element047  label="H_element : 14"  # scripted group (container) (typed FeaturePython)
  n = 14
  ref = H_element
FEATURE [App::DocumentObjectGroupPython] G4_N_HEXANE  label="G4_N-HEXANE"  # scripted group (container) (typed FeaturePython)
  Dunit = g/cm3
  Dvalue = 0.6603
  Group = -> [C_element053,H_element047]
  conduct = 2
  density = 1
  expand = 3
  formula = G4_N-HEXANE
  name = G4_N-HEXANE
  specific = 4
FEATURE [App::DocumentObjectGroupPython] C_element054  label="C_element : 22"  # scripted group (container) (typed FeaturePython)
  n = 22
  ref = C_element
FEATURE [App::DocumentObjectGroupPython] H_element048  label="H_element : 025"  # scripted group (container) (typed FeaturePython)
  n = 10
  ref = H_element
FEATURE [App::DocumentObjectGroupPython] N_element021  label="N_element : 010"  # scripted group (container) (typed FeaturePython)
  n = 2
  ref = N_element
FEATURE [App::DocumentObjectGroupPython] O_element050  label="O_element : 025"  # scripted group (container) (typed FeaturePython)
  n = 5
  ref = O_element
FEATURE [App::DocumentObjectGroupPython] G4_KAPTON  # scripted group (container) (typed FeaturePython)
  Dunit = g/cm3
  Dvalue = 1.42
  Group = -> [C_element054,H_element048,N_element021,O_element050]
  conduct = 2
  density = 1
  expand = 3
  formula = G4_KAPTON
  name = G4_KAPTON
  specific = 4
FEATURE [App::DocumentObjectGroupPython] La_element001  label="La_element : 1"  # scripted group (container) (typed FeaturePython)
  n = 1
  ref = La_element
FEATURE [App::DocumentObjectGroupPython] Br_element003  label="Br_element : 002"  # scripted group (container) (typed FeaturePython)
  n = 1
  ref = Br_element
FEATURE [App::DocumentObjectGroupPython] O_element051  label="O_element : 026"  # scripted group (container) (typed FeaturePython)
  n = 1
  ref = O_element
FEATURE [App::DocumentObjectGroupPython] G4_LANTHANUM_OXYBROMIDE  # scripted group (container) (typed FeaturePython)
  Dunit = g/cm3
  Dvalue = 6.28
  Group = -> [La_element001,Br_element003,O_element051]
  conduct = 2
  density = 1
  expand = 3
  formula = G4_LANTHANUM_OXYBROMIDE
  name = G4_LANTHANUM_OXYBROMIDE
  specific = 4
FEATURE [App::DocumentObjectGroupPython] La_element002  label="La_element : 2"  # scripted group (container) (typed FeaturePython)
  n = 2
  ref = La_element
FEATURE [App::DocumentObjectGroupPython] O_element052  label="O_element : 027"  # scripted group (container) (typed FeaturePython)
  n = 2
  ref = O_element
FEATURE [App::DocumentObjectGroupPython] S_element015  label="S_element : 006"  # scripted group (container) (typed FeaturePython)
  n = 1
  ref = S_element
FEATURE [App::DocumentObjectGroupPython] G4_LANTHANUM_OXYSULFIDE  # scripted group (container) (typed FeaturePython)
  Dunit = g/cm3
  Dvalue = 5.86
  Group = -> [La_element002,O_element052,S_element015]
  conduct = 2
  density = 1
  expand = 3
  formula = G4_LANTHANUM_OXYSULFIDE
  name = G4_LANTHANUM_OXYSULFIDE
  specific = 4
FEATURE [App::DocumentObjectGroupPython] O_element053  label="O_element : 0.072"  # scripted group (container) (typed FeaturePython)
  n = 0.071682
FEATURE [App::DocumentObjectGroupPython] Pb_element002  label="Pb_element : 0.928"  # scripted group (container) (typed FeaturePython)
  n = 0.928318
FEATURE [App::DocumentObjectGroupPython] G4_LEAD_OXIDE  # scripted group (container) (typed FeaturePython)
  Dunit = g/cm3
  Dvalue = 9.53
  Group = -> [O_element053,Pb_element002]
  conduct = 2
  density = 1
  expand = 3
  formula = G4_LEAD_OXIDE
  name = G4_LEAD_OXIDE
  specific = 4
FEATURE [App::DocumentObjectGroupPython] Li_element001  label="Li_element : 1"  # scripted group (container) (typed FeaturePython)
  n = 1
  ref = Li_element
FEATURE [App::DocumentObjectGroupPython] N_element022  label="N_element : 011"  # scripted group (container) (typed FeaturePython)
  n = 1
  ref = N_element
FEATURE [App::DocumentObjectGroupPython] H_element049  label="H_element : 026"  # scripted group (container) (typed FeaturePython)
  n = 2
  ref = H_element
FEATURE [App::DocumentObjectGroupPython] G4_LITHIUM_AMIDE  # scripted group (container) (typed FeaturePython)
  Dunit = g/cm3
  Dvalue = 1.178
  Group = -> [Li_element001,N_element022,H_element049]
  conduct = 2
  density = 1
  expand = 3
  formula = G4_LITHIUM_AMIDE
  name = G4_LITHIUM_AMIDE
  specific = 4
FEATURE [App::DocumentObjectGroupPython] Li_element002  label="Li_element : 2"  # scripted group (container) (typed FeaturePython)
  n = 2
  ref = Li_element
FEATURE [App::DocumentObjectGroupPython] C_element055  label="C_element : 030"  # scripted group (container) (typed FeaturePython)
  n = 1
  ref = C_element
FEATURE [App::DocumentObjectGroupPython] O_element054  label="O_element : 028"  # scripted group (container) (typed FeaturePython)
  n = 3
  ref = O_element
FEATURE [App::DocumentObjectGroupPython] G4_LITHIUM_CARBONATE  # scripted group (container) (typed FeaturePython)
  Dunit = g/cm3
  Dvalue = 2.11
  Group = -> [Li_element002,C_element055,O_element054]
  conduct = 2
  density = 1
  expand = 3
  formula = G4_LITHIUM_CARBONATE
  name = G4_LITHIUM_CARBONATE
  specific = 4
FEATURE [App::DocumentObjectGroupPython] Li_element003  label="Li_element : 003"  # scripted group (container) (typed FeaturePython)
  n = 1
  ref = Li_element
FEATURE [App::DocumentObjectGroupPython] F_element012  label="F_element : 004"  # scripted group (container) (typed FeaturePython)
  n = 1
  ref = F_element
FEATURE [App::DocumentObjectGroupPython] G4_LITHIUM_FLUORIDE  # scripted group (container) (typed FeaturePython)
  Dunit = g/cm3
  Dvalue = 2.635
  Group = -> [Li_element003,F_element012]
  conduct = 2
  density = 1
  expand = 3
  formula = G4_LITHIUM_FLUORIDE
  name = G4_LITHIUM_FLUORIDE
  specific = 4
FEATURE [App::DocumentObjectGroupPython] Li_element004  label="Li_element : 004"  # scripted group (container) (typed FeaturePython)
  n = 1
  ref = Li_element
FEATURE [App::DocumentObjectGroupPython] H_element050  label="H_element : 027"  # scripted group (container) (typed FeaturePython)
  n = 1
  ref = H_element
FEATURE [App::DocumentObjectGroupPython] G4_LITHIUM_HYDRIDE  # scripted group (container) (typed FeaturePython)
  Dunit = g/cm3
  Dvalue = 0.82
  Group = -> [Li_element004,H_element050]
  conduct = 2
  density = 1
  expand = 3
  formula = G4_LITHIUM_HYDRIDE
  name = G4_LITHIUM_HYDRIDE
  specific = 4
FEATURE [App::DocumentObjectGroupPython] Li_element005  label="Li_element : 005"  # scripted group (container) (typed FeaturePython)
  n = 1
  ref = Li_element
FEATURE [App::DocumentObjectGroupPython] I_element003  label="I_element : 002"  # scripted group (container) (typed FeaturePython)
  n = 1
  ref = I_element
FEATURE [App::DocumentObjectGroupPython] G4_LITHIUM_IODIDE  # scripted group (container) (typed FeaturePython)
  Dunit = g/cm3
  Dvalue = 3.494
  Group = -> [Li_element005,I_element003]
  conduct = 2
  density = 1
  expand = 3
  formula = G4_LITHIUM_IODIDE
  name = G4_LITHIUM_IODIDE
  specific = 4
FEATURE [App::DocumentObjectGroupPython] Li_element006  label="Li_element : 006"  # scripted group (container) (typed FeaturePython)
  n = 2
  ref = Li_element
FEATURE [App::DocumentObjectGroupPython] O_element055  label="O_element : 029"  # scripted group (container) (typed FeaturePython)
  n = 1
  ref = O_element
FEATURE [App::DocumentObjectGroupPython] G4_LITHIUM_OXIDE  # scripted group (container) (typed FeaturePython)
  Dunit = g/cm3
  Dvalue = 2.013
  Group = -> [Li_element006,O_element055]
  conduct = 2
  density = 1
  expand = 3
  formula = G4_LITHIUM_OXIDE
  name = G4_LITHIUM_OXIDE
  specific = 4
FEATURE [App::DocumentObjectGroupPython] Li_element007  label="Li_element : 007"  # scripted group (container) (typed FeaturePython)
  n = 2
  ref = Li_element
FEATURE [App::DocumentObjectGroupPython] B_element005  label="B_element : 005"  # scripted group (container) (typed FeaturePython)
  n = 4
  ref = B_element
FEATURE [App::DocumentObjectGroupPython] O_element056  label="O_element : 7"  # scripted group (container) (typed FeaturePython)
  n = 7
  ref = O_element
FEATURE [App::DocumentObjectGroupPython] G4_LITHIUM_TETRABORATE  # scripted group (container) (typed FeaturePython)
  Dunit = g/cm3
  Dvalue = 2.44
  Group = -> [Li_element007,B_element005,O_element056]
  conduct = 2
  density = 1
  expand = 3
  formula = G4_LITHIUM_TETRABORATE
  name = G4_LITHIUM_TETRABORATE
  specific = 4
FEATURE [App::DocumentObjectGroupPython] H_element051  label="H_element : 0.105"  # scripted group (container) (typed FeaturePython)
  n = 0.105
FEATURE [App::DocumentObjectGroupPython] C_element056  label="C_element : 0.083"  # scripted group (container) (typed FeaturePython)
  n = 0.083
FEATURE [App::DocumentObjectGroupPython] N_element023  label="N_element : 0.023"  # scripted group (container) (typed FeaturePython)
  n = 0.023
FEATURE [App::DocumentObjectGroupPython] O_element057  label="O_element : 0.779"  # scripted group (container) (typed FeaturePython)
  n = 0.779
FEATURE [App::DocumentObjectGroupPython] Na_element010  label="Na_element : 0.097"  # scripted group (container) (typed FeaturePython)
  n = 0.002
FEATURE [App::DocumentObjectGroupPython] P_element006  label="P_element : 0.105"  # scripted group (container) (typed FeaturePython)
  n = 0.001
FEATURE [App::DocumentObjectGroupPython] S_element016  label="S_element : 0.017"  # scripted group (container) (typed FeaturePython)
  n = 0.002
FEATURE [App::DocumentObjectGroupPython] Cl_element014  label="Cl_element : 0.587"  # scripted group (container) (typed FeaturePython)
  n = 0.003
FEATURE [App::DocumentObjectGroupPython] K_element005  label="K_element : 0.015"  # scripted group (container) (typed FeaturePython)
  n = 0.002
FEATURE [App::DocumentObjectGroupPython] G4_LUNG_ICRP  # scripted group (container) (typed FeaturePython)
  Dunit = g/cm3
  Dvalue = 1.04
  Group = -> [H_element051,C_element056,N_element023,O_element057,Na_element010,P_element006,S_element016,Cl_element014,K_element005]
  conduct = 2
  density = 1
  expand = 3
  formula = G4_LUNG_ICRP
  name = G4_LUNG_ICRP
  specific = 4
FEATURE [App::DocumentObjectGroupPython] H_element052  label="H_element : 0.116"  # scripted group (container) (typed FeaturePython)
  n = 0.114318
FEATURE [App::DocumentObjectGroupPython] C_element057  label="C_element : 0.656"  # scripted group (container) (typed FeaturePython)
  n = 0.655824
FEATURE [App::DocumentObjectGroupPython] O_element058  label="O_element : 0.092"  # scripted group (container) (typed FeaturePython)
  n = 0.0921831
FEATURE [App::DocumentObjectGroupPython] Mg_element004  label="Mg_element : 0.135"  # scripted group (container) (typed FeaturePython)
  n = 0.134792
FEATURE [App::DocumentObjectGroupPython] Ca_element013  label="Ca_element : 0.003"  # scripted group (container) (typed FeaturePython)
  n = 0.002883
FEATURE [App::DocumentObjectGroupPython] G4_M3_WAX  # scripted group (container) (typed FeaturePython)
  Dunit = g/cm3
  Dvalue = 1.05
  Group = -> [H_element052,C_element057,O_element058,Mg_element004,Ca_element013]
  conduct = 2
  density = 1
  expand = 3
  formula = G4_M3_WAX
  name = G4_M3_WAX
  specific = 4
FEATURE [App::DocumentObjectGroupPython] Mg_element005  label="Mg_element : 1"  # scripted group (container) (typed FeaturePython)
  n = 1
  ref = Mg_element
FEATURE [App::DocumentObjectGroupPython] C_element058  label="C_element : 031"  # scripted group (container) (typed FeaturePython)
  n = 1
  ref = C_element
FEATURE [App::DocumentObjectGroupPython] O_element059  label="O_element : 030"  # scripted group (container) (typed FeaturePython)
  n = 3
  ref = O_element
FEATURE [App::DocumentObjectGroupPython] G4_MAGNESIUM_CARBONATE  # scripted group (container) (typed FeaturePython)
  Dunit = g/cm3
  Dvalue = 2.958
  Group = -> [Mg_element005,C_element058,O_element059]
  conduct = 2
  density = 1
  expand = 3
  formula = G4_MAGNESIUM_CARBONATE
  name = G4_MAGNESIUM_CARBONATE
  specific = 4
FEATURE [App::DocumentObjectGroupPython] Mg_element006  label="Mg_element : 002"  # scripted group (container) (typed FeaturePython)
  n = 1
  ref = Mg_element
FEATURE [App::DocumentObjectGroupPython] F_element013  label="F_element : 005"  # scripted group (container) (typed FeaturePython)
  n = 2
  ref = F_element
FEATURE [App::DocumentObjectGroupPython] G4_MAGNESIUM_FLUORIDE  # scripted group (container) (typed FeaturePython)
  Dunit = g/cm3
  Dvalue = 3
  Group = -> [Mg_element006,F_element013]
  conduct = 2
  density = 1
  expand = 3
  formula = G4_MAGNESIUM_FLUORIDE
  name = G4_MAGNESIUM_FLUORIDE
  specific = 4
FEATURE [App::DocumentObjectGroupPython] Mg_element007  label="Mg_element : 003"  # scripted group (container) (typed FeaturePython)
  n = 1
  ref = Mg_element
FEATURE [App::DocumentObjectGroupPython] O_element060  label="O_element : 031"  # scripted group (container) (typed FeaturePython)
  n = 1
  ref = O_element
FEATURE [App::DocumentObjectGroupPython] G4_MAGNESIUM_OXIDE  # scripted group (container) (typed FeaturePython)
  Dunit = g/cm3
  Dvalue = 3.58
  Group = -> [Mg_element007,O_element060]
  conduct = 2
  density = 1
  expand = 3
  formula = G4_MAGNESIUM_OXIDE
  name = G4_MAGNESIUM_OXIDE
  specific = 4
FEATURE [App::DocumentObjectGroupPython] Mg_element008  label="Mg_element : 004"  # scripted group (container) (typed FeaturePython)
  n = 1
  ref = Mg_element
FEATURE [App::DocumentObjectGroupPython] B_element006  label="B_element : 006"  # scripted group (container) (typed FeaturePython)
  n = 4
  ref = B_element
FEATURE [App::DocumentObjectGroupPython] O_element061  label="O_element : 032"  # scripted group (container) (typed FeaturePython)
  n = 7
  ref = O_element
FEATURE [App::DocumentObjectGroupPython] G4_MAGNESIUM_TETRABORATE  # scripted group (container) (typed FeaturePython)
  Dunit = g/cm3
  Dvalue = 2.53
  Group = -> [Mg_element008,B_element006,O_element061]
  conduct = 2
  density = 1
  expand = 3
  formula = G4_MAGNESIUM_TETRABORATE
  name = G4_MAGNESIUM_TETRABORATE
  specific = 4
FEATURE [App::DocumentObjectGroupPython] Hg_element001  label="Hg_element : 1"  # scripted group (container) (typed FeaturePython)
  n = 1
  ref = Hg_element
FEATURE [App::DocumentObjectGroupPython] I_element004  label="I_element : 2"  # scripted group (container) (typed FeaturePython)
  n = 2
  ref = I_element
FEATURE [App::DocumentObjectGroupPython] G4_MERCURIC_IODIDE  # scripted group (container) (typed FeaturePython)
  Dunit = g/cm3
  Dvalue = 6.36
  Group = -> [Hg_element001,I_element004]
  conduct = 2
  density = 1
  expand = 3
  formula = G4_MERCURIC_IODIDE
  name = G4_MERCURIC_IODIDE
  specific = 4
FEATURE [App::DocumentObjectGroupPython] C_element059  label="C_element : 032"  # scripted group (container) (typed FeaturePython)
  n = 1
  ref = C_element
FEATURE [App::DocumentObjectGroupPython] H_element053  label="H_element : 028"  # scripted group (container) (typed FeaturePython)
  n = 4
  ref = H_element
FEATURE [App::DocumentObjectGroupPython] G4_METHANE  # scripted group (container) (typed FeaturePython)
  Dunit = g/cm3
  Dvalue = 0.000667151
  Group = -> [C_element059,H_element053]
  conduct = 2
  density = 1
  expand = 3
  formula = G4_METHANE
  name = G4_METHANE
  specific = 4
FEATURE [App::DocumentObjectGroupPython] C_element060  label="C_element : 033"  # scripted group (container) (typed FeaturePython)
  n = 1
  ref = C_element
FEATURE [App::DocumentObjectGroupPython] H_element054  label="H_element : 029"  # scripted group (container) (typed FeaturePython)
  n = 4
  ref = H_element
FEATURE [App::DocumentObjectGroupPython] O_element062  label="O_element : 033"  # scripted group (container) (typed FeaturePython)
  n = 1
  ref = O_element
FEATURE [App::DocumentObjectGroupPython] G4_METHANOL  # scripted group (container) (typed FeaturePython)
  Dunit = g/cm3
  Dvalue = 0.7914
  Group = -> [C_element060,H_element054,O_element062]
  conduct = 2
  density = 1
  expand = 3
  formula = G4_METHANOL
  name = G4_METHANOL
  specific = 4
FEATURE [App::DocumentObjectGroupPython] H_element055  label="H_element : 0.134"  # scripted group (container) (typed FeaturePython)
  n = 0.13404
FEATURE [App::DocumentObjectGroupPython] C_element061  label="C_element : 0.778"  # scripted group (container) (typed FeaturePython)
  n = 0.77796
FEATURE [App::DocumentObjectGroupPython] O_element063  label="O_element : 0.035"  # scripted group (container) (typed FeaturePython)
  n = 0.03502
FEATURE [App::DocumentObjectGroupPython] Mg_element009  label="Mg_element : 0.039"  # scripted group (container) (typed FeaturePython)
  n = 0.038594
FEATURE [App::DocumentObjectGroupPython] Ti_element002  label="Ti_element : 0.014"  # scripted group (container) (typed FeaturePython)
  n = 0.014386
FEATURE [App::DocumentObjectGroupPython] G4_MIX_D_WAX  # scripted group (container) (typed FeaturePython)
  Dunit = g/cm3
  Dvalue = 0.99
  Group = -> [H_element055,C_element061,O_element063,Mg_element009,Ti_element002]
  conduct = 2
  density = 1
  expand = 3
  formula = G4_MIX_D_WAX
  name = G4_MIX_D_WAX
  specific = 4
FEATURE [App::DocumentObjectGroupPython] H_element056  label="H_element : 0.135"  # scripted group (container) (typed FeaturePython)
  n = 0.081192
FEATURE [App::DocumentObjectGroupPython] C_element062  label="C_element : 0.583"  # scripted group (container) (typed FeaturePython)
  n = 0.583442
FEATURE [App::DocumentObjectGroupPython] N_element024  label="N_element : 0.018"  # scripted group (container) (typed FeaturePython)
  n = 0.017798
FEATURE [App::DocumentObjectGroupPython] O_element064  label="O_element : 0.186"  # scripted group (container) (typed FeaturePython)
  n = 0.186381
FEATURE [App::DocumentObjectGroupPython] Mg_element010  label="Mg_element : 0.130"  # scripted group (container) (typed FeaturePython)
  n = 0.130287
FEATURE [App::DocumentObjectGroupPython] Cl_element015  label="Cl_element : 0.588"  # scripted group (container) (typed FeaturePython)
  n = 0.0009
FEATURE [App::DocumentObjectGroupPython] G4_MS20_TISSUE  # scripted group (container) (typed FeaturePython)
  Dunit = g/cm3
  Dvalue = 1
  Group = -> [H_element056,C_element062,N_element024,O_element064,Mg_element010,Cl_element015]
  conduct = 2
  density = 1
  expand = 3
  formula = G4_MS20_TISSUE
  name = G4_MS20_TISSUE
  specific = 4
FEATURE [App::DocumentObjectGroupPython] H_element057  label="H_element : 0.136"  # scripted group (container) (typed FeaturePython)
  n = 0.102
FEATURE [App::DocumentObjectGroupPython] C_element063  label="C_element : 0.143"  # scripted group (container) (typed FeaturePython)
  n = 0.143
FEATURE [App::DocumentObjectGroupPython] N_element025  label="N_element : 0.034"  # scripted group (container) (typed FeaturePython)
  n = 0.034
FEATURE [App::DocumentObjectGroupPython] O_element065  label="O_element : 0.710"  # scripted group (container) (typed FeaturePython)
  n = 0.71
FEATURE [App::DocumentObjectGroupPython] Na_element011  label="Na_element : 0.098"  # scripted group (container) (typed FeaturePython)
  n = 0.001
FEATURE [App::DocumentObjectGroupPython] P_element007  label="P_element : 0.002"  # scripted group (container) (typed FeaturePython)
  n = 0.002
FEATURE [App::DocumentObjectGroupPython] S_element017  label="S_element : 0.018"  # scripted group (container) (typed FeaturePython)
  n = 0.003
FEATURE [App::DocumentObjectGroupPython] Cl_element016  label="Cl_element : 0.589"  # scripted group (container) (typed FeaturePython)
  n = 0.001
FEATURE [App::DocumentObjectGroupPython] K_element006  label="K_element : 0.004"  # scripted group (container) (typed FeaturePython)
  n = 0.004
FEATURE [App::DocumentObjectGroupPython] G4_MUSCLE_SKELETAL_ICRP  # scripted group (container) (typed FeaturePython)
  Dunit = g/cm3
  Dvalue = 1.05
  Group = -> [H_element057,C_element063,N_element025,O_element065,Na_element011,P_element007,S_element017,Cl_element016,K_element006]
  conduct = 2
  density = 1
  expand = 3
  formula = G4_MUSCLE_SKELETAL_ICRP
  name = G4_MUSCLE_SKELETAL_ICRP
  specific = 4
FEATURE [App::DocumentObjectGroupPython] H_element058  label="H_element : 0.137"  # scripted group (container) (typed FeaturePython)
  n = 0.102102
FEATURE [App::DocumentObjectGroupPython] C_element064  label="C_element : 0.123"  # scripted group (container) (typed FeaturePython)
  n = 0.123123
FEATURE [App::DocumentObjectGroupPython] N_element026  label="N_element : 0.756"  # scripted group (container) (typed FeaturePython)
  n = 0.035035
FEATURE [App::DocumentObjectGroupPython] O_element066  label="O_element : 0.730"  # scripted group (container) (typed FeaturePython)
  n = 0.72973
FEATURE [App::DocumentObjectGroupPython] Na_element012  label="Na_element : 0.099"  # scripted group (container) (typed FeaturePython)
  n = 0.001001
FEATURE [App::DocumentObjectGroupPython] P_element008  label="P_element : 0.106"  # scripted group (container) (typed FeaturePython)
  n = 0.002002
FEATURE [App::DocumentObjectGroupPython] S_element018  label="S_element : 0.019"  # scripted group (container) (typed FeaturePython)
  n = 0.004004
FEATURE [App::DocumentObjectGroupPython] K_element007  label="K_element : 0.016"  # scripted group (container) (typed FeaturePython)
  n = 0.003003
FEATURE [App::DocumentObjectGroupPython] G4_MUSCLE_STRIATED_ICRU  # scripted group (container) (typed FeaturePython)
  Dunit = g/cm3
  Dvalue = 1.04
  Group = -> [H_element058,C_element064,N_element026,O_element066,Na_element012,P_element008,S_element018,K_element007]
  conduct = 2
  density = 1
  expand = 3
  formula = G4_MUSCLE_STRIATED_ICRU
  name = G4_MUSCLE_STRIATED_ICRU
  specific = 4
FEATURE [App::DocumentObjectGroupPython] H_element059  label="H_element : 0.098"  # scripted group (container) (typed FeaturePython)
  n = 0.0982341
FEATURE [App::DocumentObjectGroupPython] C_element065  label="C_element : 0.156"  # scripted group (container) (typed FeaturePython)
  n = 0.156214
FEATURE [App::DocumentObjectGroupPython] N_element027  label="N_element : 0.757"  # scripted group (container) (typed FeaturePython)
  n = 0.035451
FEATURE [App::DocumentObjectGroupPython] O_element067  label="O_element : 0.880"  # scripted group (container) (typed FeaturePython)
  n = 0.710101
FEATURE [App::DocumentObjectGroupPython] G4_MUSCLE_WITH_SUCROSE  # scripted group (container) (typed FeaturePython)
  Dunit = g/cm3
  Dvalue = 1.11
  Group = -> [H_element059,C_element065,N_element027,O_element067]
  conduct = 2
  density = 1
  expand = 3
  formula = G4_MUSCLE_WITH_SUCROSE
  name = G4_MUSCLE_WITH_SUCROSE
  specific = 4
FEATURE [App::DocumentObjectGroupPython] H_element060  label="H_element : 0.138"  # scripted group (container) (typed FeaturePython)
  n = 0.101969
FEATURE [App::DocumentObjectGroupPython] C_element066  label="C_element : 0.120"  # scripted group (container) (typed FeaturePython)
  n = 0.120058
FEATURE [App::DocumentObjectGroupPython] N_element028  label="N_element : 0.758"  # scripted group (container) (typed FeaturePython)
  n = 0.035451
FEATURE [App::DocumentObjectGroupPython] O_element068  label="O_element : 0.743"  # scripted group (container) (typed FeaturePython)
  n = 0.742522
FEATURE [App::DocumentObjectGroupPython] G4_MUSCLE_WITHOUT_SUCROSE  # scripted group (container) (typed FeaturePython)
  Dunit = g/cm3
  Dvalue = 1.07
  Group = -> [H_element060,C_element066,N_element028,O_element068]
  conduct = 2
  density = 1
  expand = 3
  formula = G4_MUSCLE_WITHOUT_SUCROSE
  name = G4_MUSCLE_WITHOUT_SUCROSE
  specific = 4
FEATURE [App::DocumentObjectGroupPython] C_element067  label="C_element : 10"  # scripted group (container) (typed FeaturePython)
  n = 10
  ref = C_element
FEATURE [App::DocumentObjectGroupPython] H_element061  label="H_element : 030"  # scripted group (container) (typed FeaturePython)
  n = 8
  ref = H_element
FEATURE [App::DocumentObjectGroupPython] G4_NAPHTHALENE  # scripted group (container) (typed FeaturePython)
  Dunit = g/cm3
  Dvalue = 1.145
  Group = -> [C_element067,H_element061]
  conduct = 2
  density = 1
  expand = 3
  formula = G4_NAPHTHALENE
  name = G4_NAPHTHALENE
  specific = 4
FEATURE [App::DocumentObjectGroupPython] C_element068  label="C_element : 034"  # scripted group (container) (typed FeaturePython)
  n = 6
  ref = C_element
FEATURE [App::DocumentObjectGroupPython] H_element062  label="H_element : 031"  # scripted group (container) (typed FeaturePython)
  n = 5
  ref = H_element
FEATURE [App::DocumentObjectGroupPython] N_element029  label="N_element : 012"  # scripted group (container) (typed FeaturePython)
  n = 1
  ref = N_element
FEATURE [App::DocumentObjectGroupPython] O_element069  label="O_element : 034"  # scripted group (container) (typed FeaturePython)
  n = 2
  ref = O_element
FEATURE [App::DocumentObjectGroupPython] G4_NITROBENZENE  # scripted group (container) (typed FeaturePython)
  Dunit = g/cm3
  Dvalue = 1.19867
  Group = -> [C_element068,H_element062,N_element029,O_element069]
  conduct = 2
  density = 1
  expand = 3
  formula = G4_NITROBENZENE
  name = G4_NITROBENZENE
  specific = 4
FEATURE [App::DocumentObjectGroupPython] N_element030  label="N_element : 013"  # scripted group (container) (typed FeaturePython)
  n = 2
  ref = N_element
FEATURE [App::DocumentObjectGroupPython] O_element070  label="O_element : 035"  # scripted group (container) (typed FeaturePython)
  n = 1
  ref = O_element
FEATURE [App::DocumentObjectGroupPython] G4_NITROUS_OXIDE  # scripted group (container) (typed FeaturePython)
  Dunit = g/cm3
  Dvalue = 0.00183094
  Group = -> [N_element030,O_element070]
  conduct = 2
  density = 1
  expand = 3
  formula = G4_NITROUS_OXIDE
  name = G4_NITROUS_OXIDE
  specific = 4
FEATURE [App::DocumentObjectGroupPython] H_element063  label="H_element : 0.104"  # scripted group (container) (typed FeaturePython)
  n = 0.103509
FEATURE [App::DocumentObjectGroupPython] C_element069  label="C_element : 0.648"  # scripted group (container) (typed FeaturePython)
  n = 0.648416
FEATURE [App::DocumentObjectGroupPython] N_element031  label="N_element : 0.100"  # scripted group (container) (typed FeaturePython)
  n = 0.0995361
FEATURE [App::DocumentObjectGroupPython] O_element071  label="O_element : 0.149"  # scripted group (container) (typed FeaturePython)
  n = 0.148539
FEATURE [App::DocumentObjectGroupPython] G4_NYLON_8062  label="G4_NYLON-8062"  # scripted group (container) (typed FeaturePython)
  Dunit = g/cm3
  Dvalue = 1.08
  Group = -> [H_element063,C_element069,N_element031,O_element071]
  conduct = 2
  density = 1
  expand = 3
  formula = G4_NYLON-8062
  name = G4_NYLON-8062
  specific = 4
FEATURE [App::DocumentObjectGroupPython] C_element070  label="C_element : 035"  # scripted group (container) (typed FeaturePython)
  n = 6
  ref = C_element
FEATURE [App::DocumentObjectGroupPython] H_element064  label="H_element : 11"  # scripted group (container) (typed FeaturePython)
  n = 11
  ref = H_element
FEATURE [App::DocumentObjectGroupPython] N_element032  label="N_element : 014"  # scripted group (container) (typed FeaturePython)
  n = 1
  ref = N_element
FEATURE [App::DocumentObjectGroupPython] O_element072  label="O_element : 036"  # scripted group (container) (typed FeaturePython)
  n = 1
  ref = O_element
FEATURE [App::DocumentObjectGroupPython] G4_NYLON_6_6  label="G4_NYLON-6-6"  # scripted group (container) (typed FeaturePython)
  Dunit = g/cm3
  Dvalue = 1.14
  Group = -> [C_element070,H_element064,N_element032,O_element072]
  conduct = 2
  density = 1
  expand = 3
  formula = G4_NYLON-6-6
  name = G4_NYLON-6-6
  specific = 4
FEATURE [App::DocumentObjectGroupPython] H_element065  label="H_element : 0.139"  # scripted group (container) (typed FeaturePython)
  n = 0.107062
FEATURE [App::DocumentObjectGroupPython] C_element071  label="C_element : 0.680"  # scripted group (container) (typed FeaturePython)
  n = 0.680449
FEATURE [App::DocumentObjectGroupPython] N_element033  label="N_element : 0.099"  # scripted group (container) (typed FeaturePython)
  n = 0.099189
FEATURE [App::DocumentObjectGroupPython] O_element073  label="O_element : 0.113"  # scripted group (container) (typed FeaturePython)
  n = 0.1133
FEATURE [App::DocumentObjectGroupPython] G4_NYLON_6_10  label="G4_NYLON-6-10"  # scripted group (container) (typed FeaturePython)
  Dunit = g/cm3
  Dvalue = 1.14
  Group = -> [H_element065,C_element071,N_element033,O_element073]
  conduct = 2
  density = 1
  expand = 3
  formula = G4_NYLON-6-10
  name = G4_NYLON-6-10
  specific = 4
FEATURE [App::DocumentObjectGroupPython] H_element066  label="H_element : 0.140"  # scripted group (container) (typed FeaturePython)
  n = 0.115476
FEATURE [App::DocumentObjectGroupPython] C_element072  label="C_element : 0.721"  # scripted group (container) (typed FeaturePython)
  n = 0.720818
FEATURE [App::DocumentObjectGroupPython] N_element034  label="N_element : 0.076"  # scripted group (container) (typed FeaturePython)
  n = 0.0764169
FEATURE [App::DocumentObjectGroupPython] O_element074  label="O_element : 0.087"  # scripted group (container) (typed FeaturePython)
  n = 0.0872889
FEATURE [App::DocumentObjectGroupPython] G4_NYLON_11_RILSAN  label="G4_NYLON-11_RILSAN"  # scripted group (container) (typed FeaturePython)
  Dunit = g/cm3
  Dvalue = 1.425
  Group = -> [H_element066,C_element072,N_element034,O_element074]
  conduct = 2
  density = 1
  expand = 3
  formula = G4_NYLON-11_RILSAN
  name = G4_NYLON-11_RILSAN
  specific = 4
FEATURE [App::DocumentObjectGroupPython] C_element073  label="C_element : 8"  # scripted group (container) (typed FeaturePython)
  n = 8
  ref = C_element
FEATURE [App::DocumentObjectGroupPython] H_element067  label="H_element : 18"  # scripted group (container) (typed FeaturePython)
  n = 18
  ref = H_element
FEATURE [App::DocumentObjectGroupPython] G4_OCTANE  # scripted group (container) (typed FeaturePython)
  Dunit = g/cm3
  Dvalue = 0.7026
  Group = -> [C_element073,H_element067]
  conduct = 2
  density = 1
  expand = 3
  formula = G4_OCTANE
  name = G4_OCTANE
  specific = 4
FEATURE [App::DocumentObjectGroupPython] C_element074  label="C_element : 25"  # scripted group (container) (typed FeaturePython)
  n = 25
  ref = C_element
FEATURE [App::DocumentObjectGroupPython] H_element068  label="H_element : 52"  # scripted group (container) (typed FeaturePython)
  n = 52
  ref = H_element
FEATURE [App::DocumentObjectGroupPython] G4_PARAFFIN  # scripted group (container) (typed FeaturePython)
  Dunit = g/cm3
  Dvalue = 0.93
  Group = -> [C_element074,H_element068]
  conduct = 2
  density = 1
  expand = 3
  formula = G4_PARAFFIN
  name = G4_PARAFFIN
  specific = 4
FEATURE [App::DocumentObjectGroupPython] C_element075  label="C_element : 036"  # scripted group (container) (typed FeaturePython)
  n = 5
  ref = C_element
FEATURE [App::DocumentObjectGroupPython] H_element069  label="H_element : 032"  # scripted group (container) (typed FeaturePython)
  n = 12
  ref = H_element
FEATURE [App::DocumentObjectGroupPython] G4_N_PENTANE  label="G4_N-PENTANE"  # scripted group (container) (typed FeaturePython)
  Dunit = g/cm3
  Dvalue = 0.6262
  Group = -> [C_element075,H_element069]
  conduct = 2
  density = 1
  expand = 3
  formula = G4_N-PENTANE
  name = G4_N-PENTANE
  specific = 4
FEATURE [App::DocumentObjectGroupPython] H_element070  label="H_element : 0.014"  # scripted group (container) (typed FeaturePython)
  n = 0.0141
FEATURE [App::DocumentObjectGroupPython] C_element076  label="C_element : 0.072"  # scripted group (container) (typed FeaturePython)
  n = 0.072261
FEATURE [App::DocumentObjectGroupPython] N_element035  label="N_element : 0.019"  # scripted group (container) (typed FeaturePython)
  n = 0.01932
FEATURE [App::DocumentObjectGroupPython] O_element075  label="O_element : 0.066"  # scripted group (container) (typed FeaturePython)
  n = 0.066101
FEATURE [App::DocumentObjectGroupPython] S_element019  label="S_element : 0.020"  # scripted group (container) (typed FeaturePython)
  n = 0.00189
FEATURE [App::DocumentObjectGroupPython] Br_element004  label="Br_element : 0.349"  # scripted group (container) (typed FeaturePython)
  n = 0.349103
FEATURE [App::DocumentObjectGroupPython] Ag_element001  label="Ag_element : 0.474"  # scripted group (container) (typed FeaturePython)
  n = 0.474105
FEATURE [App::DocumentObjectGroupPython] I_element005  label="I_element : 0.003"  # scripted group (container) (typed FeaturePython)
  n = 0.00312
FEATURE [App::DocumentObjectGroupPython] G4_PHOTO_EMULSION  # scripted group (container) (typed FeaturePython)
  Dunit = g/cm3
  Dvalue = 3.815
  Group = -> [H_element070,C_element076,N_element035,O_element075,S_element019,Br_element004,Ag_element001,I_element005]
  conduct = 2
  density = 1
  expand = 3
  formula = G4_PHOTO_EMULSION
  name = G4_PHOTO_EMULSION
  specific = 4
FEATURE [App::DocumentObjectGroupPython] C_element077  label="C_element : 9"  # scripted group (container) (typed FeaturePython)
  n = 9
  ref = C_element
FEATURE [App::DocumentObjectGroupPython] H_element071  label="H_element : 033"  # scripted group (container) (typed FeaturePython)
  n = 10
  ref = H_element
FEATURE [App::DocumentObjectGroupPython] G4_PLASTIC_SC_VINYLTOLUENE  # scripted group (container) (typed FeaturePython)
  Dunit = g/cm3
  Dvalue = 1.032
  Group = -> [C_element077,H_element071]
  conduct = 2
  density = 1
  expand = 3
  formula = G4_PLASTIC_SC_VINYLTOLUENE
  name = G4_PLASTIC_SC_VINYLTOLUENE
  specific = 4
FEATURE [App::DocumentObjectGroupPython] Pu_element001  label="Pu_element : 1"  # scripted group (container) (typed FeaturePython)
  n = 1
  ref = Pu_element
FEATURE [App::DocumentObjectGroupPython] O_element076  label="O_element : 037"  # scripted group (container) (typed FeaturePython)
  n = 2
  ref = O_element
FEATURE [App::DocumentObjectGroupPython] G4_PLUTONIUM_DIOXIDE  # scripted group (container) (typed FeaturePython)
  Dunit = g/cm3
  Dvalue = 11.46
  Group = -> [Pu_element001,O_element076]
  conduct = 2
  density = 1
  expand = 3
  formula = G4_PLUTONIUM_DIOXIDE
  name = G4_PLUTONIUM_DIOXIDE
  specific = 4
FEATURE [App::DocumentObjectGroupPython] C_element078  label="C_element : 037"  # scripted group (container) (typed FeaturePython)
  n = 3
  ref = C_element
FEATURE [App::DocumentObjectGroupPython] H_element072  label="H_element : 034"  # scripted group (container) (typed FeaturePython)
  n = 3
  ref = H_element
FEATURE [App::DocumentObjectGroupPython] N_element036  label="N_element : 015"  # scripted group (container) (typed FeaturePython)
  n = 1
  ref = N_element
FEATURE [App::DocumentObjectGroupPython] G4_POLYACRYLONITRILE  # scripted group (container) (typed FeaturePython)
  Dunit = g/cm3
  Dvalue = 1.17
  Group = -> [C_element078,H_element072,N_element036]
  conduct = 2
  density = 1
  expand = 3
  formula = G4_POLYACRYLONITRILE
  name = G4_POLYACRYLONITRILE
  specific = 4
FEATURE [App::DocumentObjectGroupPython] C_element079  label="C_element : 16"  # scripted group (container) (typed FeaturePython)
  n = 16
  ref = C_element
FEATURE [App::DocumentObjectGroupPython] H_element073  label="H_element : 035"  # scripted group (container) (typed FeaturePython)
  n = 14
  ref = H_element
FEATURE [App::DocumentObjectGroupPython] O_element077  label="O_element : 038"  # scripted group (container) (typed FeaturePython)
  n = 3
  ref = O_element
FEATURE [App::DocumentObjectGroupPython] G4_POLYCARBONATE  # scripted group (container) (typed FeaturePython)
  Dunit = g/cm3
  Dvalue = 1.2
  Group = -> [C_element079,H_element073,O_element077]
  conduct = 2
  density = 1
  expand = 3
  formula = G4_POLYCARBONATE
  name = G4_POLYCARBONATE
  specific = 4
FEATURE [App::DocumentObjectGroupPython] C_element080  label="C_element : 038"  # scripted group (container) (typed FeaturePython)
  n = 8
  ref = C_element
FEATURE [App::DocumentObjectGroupPython] H_element074  label="H_element : 036"  # scripted group (container) (typed FeaturePython)
  n = 7
  ref = H_element
FEATURE [App::DocumentObjectGroupPython] Cl_element017  label="Cl_element : 007"  # scripted group (container) (typed FeaturePython)
  n = 1
  ref = Cl_element
FEATURE [App::DocumentObjectGroupPython] G4_POLYCHLOROSTYRENE  # scripted group (container) (typed FeaturePython)
  Dunit = g/cm3
  Dvalue = 1.3
  Group = -> [C_element080,H_element074,Cl_element017]
  conduct = 2
  density = 1
  expand = 3
  formula = G4_POLYCHLOROSTYRENE
  name = G4_POLYCHLOROSTYRENE
  specific = 4
FEATURE [App::DocumentObjectGroupPython] C_element081  label="C_element : 039"  # scripted group (container) (typed FeaturePython)
  n = 1
  ref = C_element
FEATURE [App::DocumentObjectGroupPython] H_element075  label="H_element : 037"  # scripted group (container) (typed FeaturePython)
  n = 2
  ref = H_element
FEATURE [App::DocumentObjectGroupPython] G4_POLYETHYLENE  # scripted group (container) (typed FeaturePython)
  Dunit = g/cm3
  Dvalue = 0.94
  Group = -> [C_element081,H_element075]
  conduct = 2
  density = 1
  expand = 3
  formula = G4_POLYETHYLENE
  name = G4_POLYETHYLENE
  specific = 4
FEATURE [App::DocumentObjectGroupPython] C_element082  label="C_element : 040"  # scripted group (container) (typed FeaturePython)
  n = 10
  ref = C_element
FEATURE [App::DocumentObjectGroupPython] H_element076  label="H_element : 038"  # scripted group (container) (typed FeaturePython)
  n = 8
  ref = H_element
FEATURE [App::DocumentObjectGroupPython] O_element078  label="O_element : 039"  # scripted group (container) (typed FeaturePython)
  n = 4
  ref = O_element
FEATURE [App::DocumentObjectGroupPython] G4_MYLAR  # scripted group (container) (typed FeaturePython)
  Dunit = g/cm3
  Dvalue = 1.4
  Group = -> [C_element082,H_element076,O_element078]
  conduct = 2
  density = 1
  expand = 3
  formula = G4_MYLAR
  name = G4_MYLAR
  specific = 4
FEATURE [App::DocumentObjectGroupPython] C_element083  label="C_element : 041"  # scripted group (container) (typed FeaturePython)
  n = 5
  ref = C_element
FEATURE [App::DocumentObjectGroupPython] H_element077  label="H_element : 039"  # scripted group (container) (typed FeaturePython)
  n = 8
  ref = H_element
FEATURE [App::DocumentObjectGroupPython] O_element079  label="O_element : 040"  # scripted group (container) (typed FeaturePython)
  n = 2
  ref = O_element
FEATURE [App::DocumentObjectGroupPython] G4_PLEXIGLASS  # scripted group (container) (typed FeaturePython)
  Dunit = g/cm3
  Dvalue = 1.19
  Group = -> [C_element083,H_element077,O_element079]
  conduct = 2
  density = 1
  expand = 3
  formula = G4_PLEXIGLASS
  name = G4_PLEXIGLASS
  specific = 4
FEATURE [App::DocumentObjectGroupPython] C_element084  label="C_element : 042"  # scripted group (container) (typed FeaturePython)
  n = 1
  ref = C_element
FEATURE [App::DocumentObjectGroupPython] H_element078  label="H_element : 040"  # scripted group (container) (typed FeaturePython)
  n = 2
  ref = H_element
FEATURE [App::DocumentObjectGroupPython] O_element080  label="O_element : 041"  # scripted group (container) (typed FeaturePython)
  n = 1
  ref = O_element
FEATURE [App::DocumentObjectGroupPython] G4_POLYOXYMETHYLENE  # scripted group (container) (typed FeaturePython)
  Dunit = g/cm3
  Dvalue = 1.425
  Group = -> [C_element084,H_element078,O_element080]
  conduct = 2
  density = 1
  expand = 3
  formula = G4_POLYOXYMETHYLENE
  name = G4_POLYOXYMETHYLENE
  specific = 4
FEATURE [App::DocumentObjectGroupPython] C_element085  label="C_element : 043"  # scripted group (container) (typed FeaturePython)
  n = 2
  ref = C_element
FEATURE [App::DocumentObjectGroupPython] H_element079  label="H_element : 041"  # scripted group (container) (typed FeaturePython)
  n = 4
  ref = H_element
FEATURE [App::DocumentObjectGroupPython] G4_POLYPROPYLENE  # scripted group (container) (typed FeaturePython)
  Dunit = g/cm3
  Dvalue = 0.9
  Group = -> [C_element085,H_element079]
  conduct = 2
  density = 1
  expand = 3
  formula = G4_POLYPROPYLENE
  name = G4_POLYPROPYLENE
  specific = 4
FEATURE [App::DocumentObjectGroupPython] C_element086  label="C_element : 044"  # scripted group (container) (typed FeaturePython)
  n = 8
  ref = C_element
FEATURE [App::DocumentObjectGroupPython] H_element080  label="H_element : 042"  # scripted group (container) (typed FeaturePython)
  n = 8
  ref = H_element
FEATURE [App::DocumentObjectGroupPython] G4_POLYSTYRENE  # scripted group (container) (typed FeaturePython)
  Dunit = g/cm3
  Dvalue = 1.06
  Group = -> [C_element086,H_element080]
  conduct = 2
  density = 1
  expand = 3
  formula = G4_POLYSTYRENE
  name = G4_POLYSTYRENE
  specific = 4
FEATURE [App::DocumentObjectGroupPython] C_element087  label="C_element : 045"  # scripted group (container) (typed FeaturePython)
  n = 2
  ref = C_element
FEATURE [App::DocumentObjectGroupPython] F_element014  label="F_element : 4"  # scripted group (container) (typed FeaturePython)
  n = 4
  ref = F_element
FEATURE [App::DocumentObjectGroupPython] G4_TEFLON  # scripted group (container) (typed FeaturePython)
  Dunit = g/cm3
  Dvalue = 2.2
  Group = -> [C_element087,F_element014]
  conduct = 2
  density = 1
  expand = 3
  formula = G4_TEFLON
  name = G4_TEFLON
  specific = 4
FEATURE [App::DocumentObjectGroupPython] C_element088  label="C_element : 046"  # scripted group (container) (typed FeaturePython)
  n = 2
  ref = C_element
FEATURE [App::DocumentObjectGroupPython] F_element015  label="F_element : 006"  # scripted group (container) (typed FeaturePython)
  n = 3
  ref = F_element
FEATURE [App::DocumentObjectGroupPython] Cl_element018  label="Cl_element : 008"  # scripted group (container) (typed FeaturePython)
  n = 1
  ref = Cl_element
FEATURE [App::DocumentObjectGroupPython] G4_POLYTRIFLUOROCHLOROETHYLENE  # scripted group (container) (typed FeaturePython)
  Dunit = g/cm3
  Dvalue = 2.1
  Group = -> [C_element088,F_element015,Cl_element018]
  conduct = 2
  density = 1
  expand = 3
  formula = G4_POLYTRIFLUOROCHLOROETHYLENE
  name = G4_POLYTRIFLUOROCHLOROETHYLENE
  specific = 4
FEATURE [App::DocumentObjectGroupPython] C_element089  label="C_element : 047"  # scripted group (container) (typed FeaturePython)
  n = 4
  ref = C_element
FEATURE [App::DocumentObjectGroupPython] H_element081  label="H_element : 043"  # scripted group (container) (typed FeaturePython)
  n = 6
  ref = H_element
FEATURE [App::DocumentObjectGroupPython] O_element081  label="O_element : 042"  # scripted group (container) (typed FeaturePython)
  n = 2
  ref = O_element
FEATURE [App::DocumentObjectGroupPython] G4_POLYVINYL_ACETATE  # scripted group (container) (typed FeaturePython)
  Dunit = g/cm3
  Dvalue = 1.19
  Group = -> [C_element089,H_element081,O_element081]
  conduct = 2
  density = 1
  expand = 3
  formula = G4_POLYVINYL_ACETATE
  name = G4_POLYVINYL_ACETATE
  specific = 4
FEATURE [App::DocumentObjectGroupPython] C_element090  label="C_element : 048"  # scripted group (container) (typed FeaturePython)
  n = 2
  ref = C_element
FEATURE [App::DocumentObjectGroupPython] H_element082  label="H_element : 044"  # scripted group (container) (typed FeaturePython)
  n = 4
  ref = H_element
FEATURE [App::DocumentObjectGroupPython] O_element082  label="O_element : 043"  # scripted group (container) (typed FeaturePython)
  n = 1
  ref = O_element
FEATURE [App::DocumentObjectGroupPython] G4_POLYVINYL_ALCOHOL  # scripted group (container) (typed FeaturePython)
  Dunit = g/cm3
  Dvalue = 1.3
  Group = -> [C_element090,H_element082,O_element082]
  conduct = 2
  density = 1
  expand = 3
  formula = G4_POLYVINYL_ALCOHOL
  name = G4_POLYVINYL_ALCOHOL
  specific = 4
FEATURE [App::DocumentObjectGroupPython] C_element091  label="C_element : 049"  # scripted group (container) (typed FeaturePython)
  n = 8
  ref = C_element
FEATURE [App::DocumentObjectGroupPython] H_element083  label="H_element : 045"  # scripted group (container) (typed FeaturePython)
  n = 14
  ref = H_element
FEATURE [App::DocumentObjectGroupPython] O_element083  label="O_element : 044"  # scripted group (container) (typed FeaturePython)
  n = 2
  ref = O_element
FEATURE [App::DocumentObjectGroupPython] G4_POLYVINYL_BUTYRAL  # scripted group (container) (typed FeaturePython)
  Dunit = g/cm3
  Dvalue = 1.12
  Group = -> [C_element091,H_element083,O_element083]
  conduct = 2
  density = 1
  expand = 3
  formula = G4_POLYVINYL_BUTYRAL
  name = G4_POLYVINYL_BUTYRAL
  specific = 4
FEATURE [App::DocumentObjectGroupPython] C_element092  label="C_element : 050"  # scripted group (container) (typed FeaturePython)
  n = 2
  ref = C_element
FEATURE [App::DocumentObjectGroupPython] H_element084  label="H_element : 046"  # scripted group (container) (typed FeaturePython)
  n = 3
  ref = H_element
FEATURE [App::DocumentObjectGroupPython] Cl_element019  label="Cl_element : 009"  # scripted group (container) (typed FeaturePython)
  n = 1
  ref = Cl_element
FEATURE [App::DocumentObjectGroupPython] G4_POLYVINYL_CHLORIDE  # scripted group (container) (typed FeaturePython)
  Dunit = g/cm3
  Dvalue = 1.3
  Group = -> [C_element092,H_element084,Cl_element019]
  conduct = 2
  density = 1
  expand = 3
  formula = G4_POLYVINYL_CHLORIDE
  name = G4_POLYVINYL_CHLORIDE
  specific = 4
FEATURE [App::DocumentObjectGroupPython] C_element093  label="C_element : 051"  # scripted group (container) (typed FeaturePython)
  n = 2
  ref = C_element
FEATURE [App::DocumentObjectGroupPython] H_element085  label="H_element : 047"  # scripted group (container) (typed FeaturePython)
  n = 2
  ref = H_element
FEATURE [App::DocumentObjectGroupPython] Cl_element020  label="Cl_element : 010"  # scripted group (container) (typed FeaturePython)
  n = 2
  ref = Cl_element
FEATURE [App::DocumentObjectGroupPython] G4_POLYVINYLIDENE_CHLORIDE  # scripted group (container) (typed FeaturePython)
  Dunit = g/cm3
  Dvalue = 1.7
  Group = -> [C_element093,H_element085,Cl_element020]
  conduct = 2
  density = 1
  expand = 3
  formula = G4_POLYVINYLIDENE_CHLORIDE
  name = G4_POLYVINYLIDENE_CHLORIDE
  specific = 4
FEATURE [App::DocumentObjectGroupPython] C_element094  label="C_element : 052"  # scripted group (container) (typed FeaturePython)
  n = 2
  ref = C_element
FEATURE [App::DocumentObjectGroupPython] H_element086  label="H_element : 048"  # scripted group (container) (typed FeaturePython)
  n = 2
  ref = H_element
FEATURE [App::DocumentObjectGroupPython] F_element016  label="F_element : 007"  # scripted group (container) (typed FeaturePython)
  n = 2
  ref = F_element
FEATURE [App::DocumentObjectGroupPython] G4_POLYVINYLIDENE_FLUORIDE  # scripted group (container) (typed FeaturePython)
  Dunit = g/cm3
  Dvalue = 1.76
  Group = -> [C_element094,H_element086,F_element016]
  conduct = 2
  density = 1
  expand = 3
  formula = G4_POLYVINYLIDENE_FLUORIDE
  name = G4_POLYVINYLIDENE_FLUORIDE
  specific = 4
FEATURE [App::DocumentObjectGroupPython] C_element095  label="C_element : 053"  # scripted group (container) (typed FeaturePython)
  n = 6
  ref = C_element
FEATURE [App::DocumentObjectGroupPython] H_element087  label="H_element : 9"  # scripted group (container) (typed FeaturePython)
  n = 9
  ref = H_element
FEATURE [App::DocumentObjectGroupPython] N_element037  label="N_element : 016"  # scripted group (container) (typed FeaturePython)
  n = 1
  ref = N_element
FEATURE [App::DocumentObjectGroupPython] O_element084  label="O_element : 045"  # scripted group (container) (typed FeaturePython)
  n = 1
  ref = O_element
FEATURE [App::DocumentObjectGroupPython] G4_POLYVINYL_PYRROLIDONE  # scripted group (container) (typed FeaturePython)
  Dunit = g/cm3
  Dvalue = 1.25
  Group = -> [C_element095,H_element087,N_element037,O_element084]
  conduct = 2
  density = 1
  expand = 3
  formula = G4_POLYVINYL_PYRROLIDONE
  name = G4_POLYVINYL_PYRROLIDONE
  specific = 4
FEATURE [App::DocumentObjectGroupPython] K_element008  label="K_element : 1"  # scripted group (container) (typed FeaturePython)
  n = 1
  ref = K_element
FEATURE [App::DocumentObjectGroupPython] I_element006  label="I_element : 003"  # scripted group (container) (typed FeaturePython)
  n = 1
  ref = I_element
FEATURE [App::DocumentObjectGroupPython] G4_POTASSIUM_IODIDE  # scripted group (container) (typed FeaturePython)
  Dunit = g/cm3
  Dvalue = 3.13
  Group = -> [K_element008,I_element006]
  conduct = 2
  density = 1
  expand = 3
  formula = G4_POTASSIUM_IODIDE
  name = G4_POTASSIUM_IODIDE
  specific = 4
FEATURE [App::DocumentObjectGroupPython] K_element009  label="K_element : 2"  # scripted group (container) (typed FeaturePython)
  n = 2
  ref = K_element
FEATURE [App::DocumentObjectGroupPython] O_element085  label="O_element : 046"  # scripted group (container) (typed FeaturePython)
  n = 1
  ref = O_element
FEATURE [App::DocumentObjectGroupPython] G4_POTASSIUM_OXIDE  # scripted group (container) (typed FeaturePython)
  Dunit = g/cm3
  Dvalue = 2.32
  Group = -> [K_element009,O_element085]
  conduct = 2
  density = 1
  expand = 3
  formula = G4_POTASSIUM_OXIDE
  name = G4_POTASSIUM_OXIDE
  specific = 4
FEATURE [App::DocumentObjectGroupPython] C_element096  label="C_element : 054"  # scripted group (container) (typed FeaturePython)
  n = 3
  ref = C_element
FEATURE [App::DocumentObjectGroupPython] H_element088  label="H_element : 049"  # scripted group (container) (typed FeaturePython)
  n = 8
  ref = H_element
FEATURE [App::DocumentObjectGroupPython] G4_PROPANE  # scripted group (container) (typed FeaturePython)
  Dunit = g/cm3
  Dvalue = 0.00187939
  Group = -> [C_element096,H_element088]
  conduct = 2
  density = 1
  expand = 3
  formula = G4_PROPANE
  name = G4_PROPANE
  specific = 4
FEATURE [App::DocumentObjectGroupPython] C_element097  label="C_element : 055"  # scripted group (container) (typed FeaturePython)
  n = 3
  ref = C_element
FEATURE [App::DocumentObjectGroupPython] H_element089  label="H_element : 050"  # scripted group (container) (typed FeaturePython)
  n = 8
  ref = H_element
FEATURE [App::DocumentObjectGroupPython] G4_lPROPANE  # scripted group (container) (typed FeaturePython)
  Dunit = g/cm3
  Dvalue = 0.43
  Group = -> [C_element097,H_element089]
  conduct = 2
  density = 1
  expand = 3
  formula = G4_lPROPANE
  name = G4_lPROPANE
  specific = 4
FEATURE [App::DocumentObjectGroupPython] C_element098  label="C_element : 056"  # scripted group (container) (typed FeaturePython)
  n = 3
  ref = C_element
FEATURE [App::DocumentObjectGroupPython] H_element090  label="H_element : 051"  # scripted group (container) (typed FeaturePython)
  n = 8
  ref = H_element
FEATURE [App::DocumentObjectGroupPython] O_element086  label="O_element : 047"  # scripted group (container) (typed FeaturePython)
  n = 1
  ref = O_element
FEATURE [App::DocumentObjectGroupPython] G4_N_PROPYL_ALCOHOL  label="G4_N-PROPYL_ALCOHOL"  # scripted group (container) (typed FeaturePython)
  Dunit = g/cm3
  Dvalue = 0.8035
  Group = -> [C_element098,H_element090,O_element086]
  conduct = 2
  density = 1
  expand = 3
  formula = G4_N-PROPYL_ALCOHOL
  name = G4_N-PROPYL_ALCOHOL
  specific = 4
FEATURE [App::DocumentObjectGroupPython] C_element099  label="C_element : 057"  # scripted group (container) (typed FeaturePython)
  n = 5
  ref = C_element
FEATURE [App::DocumentObjectGroupPython] H_element091  label="H_element : 052"  # scripted group (container) (typed FeaturePython)
  n = 5
  ref = H_element
FEATURE [App::DocumentObjectGroupPython] N_element038  label="N_element : 017"  # scripted group (container) (typed FeaturePython)
  n = 1
  ref = N_element
FEATURE [App::DocumentObjectGroupPython] G4_PYRIDINE  # scripted group (container) (typed FeaturePython)
  Dunit = g/cm3
  Dvalue = 0.9819
  Group = -> [C_element099,H_element091,N_element038]
  conduct = 2
  density = 1
  expand = 3
  formula = G4_PYRIDINE
  name = G4_PYRIDINE
  specific = 4
FEATURE [App::DocumentObjectGroupPython] H_element092  label="H_element : 0.144"  # scripted group (container) (typed FeaturePython)
  n = 0.143711
FEATURE [App::DocumentObjectGroupPython] C_element100  label="C_element : 0.856"  # scripted group (container) (typed FeaturePython)
  n = 0.856289
FEATURE [App::DocumentObjectGroupPython] G4_RUBBER_BUTYL  # scripted group (container) (typed FeaturePython)
  Dunit = g/cm3
  Dvalue = 0.92
  Group = -> [H_element092,C_element100]
  conduct = 2
  density = 1
  expand = 3
  formula = G4_RUBBER_BUTYL
  name = G4_RUBBER_BUTYL
  specific = 4
FEATURE [App::DocumentObjectGroupPython] H_element093  label="H_element : 0.118"  # scripted group (container) (typed FeaturePython)
  n = 0.118371
FEATURE [App::DocumentObjectGroupPython] C_element101  label="C_element : 0.882"  # scripted group (container) (typed FeaturePython)
  n = 0.881629
FEATURE [App::DocumentObjectGroupPython] G4_RUBBER_NATURAL  # scripted group (container) (typed FeaturePython)
  Dunit = g/cm3
  Dvalue = 0.92
  Group = -> [H_element093,C_element101]
  conduct = 2
  density = 1
  expand = 3
  formula = G4_RUBBER_NATURAL
  name = G4_RUBBER_NATURAL
  specific = 4
FEATURE [App::DocumentObjectGroupPython] H_element094  label="H_element : 0.145"  # scripted group (container) (typed FeaturePython)
  n = 0.05692
FEATURE [App::DocumentObjectGroupPython] C_element102  label="C_element : 0.543"  # scripted group (container) (typed FeaturePython)
  n = 0.542646
FEATURE [App::DocumentObjectGroupPython] Cl_element021  label="Cl_element : 0.400"  # scripted group (container) (typed FeaturePython)
  n = 0.400434
FEATURE [App::DocumentObjectGroupPython] G4_RUBBER_NEOPRENE  # scripted group (container) (typed FeaturePython)
  Dunit = g/cm3
  Dvalue = 1.23
  Group = -> [H_element094,C_element102,Cl_element021]
  conduct = 2
  density = 1
  expand = 3
  formula = G4_RUBBER_NEOPRENE
  name = G4_RUBBER_NEOPRENE
  specific = 4
FEATURE [App::DocumentObjectGroupPython] Si_element006  label="Si_element : 1"  # scripted group (container) (typed FeaturePython)
  n = 1
  ref = Si_element
FEATURE [App::DocumentObjectGroupPython] O_element087  label="O_element : 048"  # scripted group (container) (typed FeaturePython)
  n = 2
  ref = O_element
FEATURE [App::DocumentObjectGroupPython] G4_SILICON_DIOXIDE  # scripted group (container) (typed FeaturePython)
  Dunit = g/cm3
  Dvalue = 2.32
  Group = -> [Si_element006,O_element087]
  conduct = 2
  density = 1
  expand = 3
  formula = G4_SILICON_DIOXIDE
  name = G4_SILICON_DIOXIDE
  specific = 4
FEATURE [App::DocumentObjectGroupPython] Ag_element002  label="Ag_element : 1"  # scripted group (container) (typed FeaturePython)
  n = 1
  ref = Ag_element
FEATURE [App::DocumentObjectGroupPython] Br_element005  label="Br_element : 003"  # scripted group (container) (typed FeaturePython)
  n = 1
  ref = Br_element
FEATURE [App::DocumentObjectGroupPython] G4_SILVER_BROMIDE  # scripted group (container) (typed FeaturePython)
  Dunit = g/cm3
  Dvalue = 6.473
  Group = -> [Ag_element002,Br_element005]
  conduct = 2
  density = 1
  expand = 3
  formula = G4_SILVER_BROMIDE
  name = G4_SILVER_BROMIDE
  specific = 4
FEATURE [App::DocumentObjectGroupPython] Ag_element003  label="Ag_element : 002"  # scripted group (container) (typed FeaturePython)
  n = 1
  ref = Ag_element
FEATURE [App::DocumentObjectGroupPython] Cl_element022  label="Cl_element : 011"  # scripted group (container) (typed FeaturePython)
  n = 1
  ref = Cl_element
FEATURE [App::DocumentObjectGroupPython] G4_SILVER_CHLORIDE  # scripted group (container) (typed FeaturePython)
  Dunit = g/cm3
  Dvalue = 5.56
  Group = -> [Ag_element003,Cl_element022]
  conduct = 2
  density = 1
  expand = 3
  formula = G4_SILVER_CHLORIDE
  name = G4_SILVER_CHLORIDE
  specific = 4
FEATURE [App::DocumentObjectGroupPython] Br_element006  label="Br_element : 0.423"  # scripted group (container) (typed FeaturePython)
  n = 0.422895
FEATURE [App::DocumentObjectGroupPython] Ag_element004  label="Ag_element : 0.574"  # scripted group (container) (typed FeaturePython)
  n = 0.573748
FEATURE [App::DocumentObjectGroupPython] I_element007  label="I_element : 0.649"  # scripted group (container) (typed FeaturePython)
  n = 0.003357
FEATURE [App::DocumentObjectGroupPython] G4_SILVER_HALIDES  # scripted group (container) (typed FeaturePython)
  Dunit = g/cm3
  Dvalue = 6.47
  Group = -> [Br_element006,Ag_element004,I_element007]
  conduct = 2
  density = 1
  expand = 3
  formula = G4_SILVER_HALIDES
  name = G4_SILVER_HALIDES
  specific = 4
FEATURE [App::DocumentObjectGroupPython] Ag_element005  label="Ag_element : 003"  # scripted group (container) (typed FeaturePython)
  n = 1
  ref = Ag_element
FEATURE [App::DocumentObjectGroupPython] I_element008  label="I_element : 004"  # scripted group (container) (typed FeaturePython)
  n = 1
  ref = I_element
FEATURE [App::DocumentObjectGroupPython] G4_SILVER_IODIDE  # scripted group (container) (typed FeaturePython)
  Dunit = g/cm3
  Dvalue = 6.01
  Group = -> [Ag_element005,I_element008]
  conduct = 2
  density = 1
  expand = 3
  formula = G4_SILVER_IODIDE
  name = G4_SILVER_IODIDE
  specific = 4
FEATURE [App::DocumentObjectGroupPython] H_element095  label="H_element : 0.100"  # scripted group (container) (typed FeaturePython)
  n = 0.1
FEATURE [App::DocumentObjectGroupPython] C_element103  label="C_element : 0.204"  # scripted group (container) (typed FeaturePython)
  n = 0.204
FEATURE [App::DocumentObjectGroupPython] N_element039  label="N_element : 0.759"  # scripted group (container) (typed FeaturePython)
  n = 0.042
FEATURE [App::DocumentObjectGroupPython] O_element088  label="O_element : 0.645"  # scripted group (container) (typed FeaturePython)
  n = 0.645
FEATURE [App::DocumentObjectGroupPython] Na_element013  label="Na_element : 0.100"  # scripted group (container) (typed FeaturePython)
  n = 0.002
FEATURE [App::DocumentObjectGroupPython] P_element009  label="P_element : 0.107"  # scripted group (container) (typed FeaturePython)
  n = 0.001
FEATURE [App::DocumentObjectGroupPython] S_element020  label="S_element : 0.021"  # scripted group (container) (typed FeaturePython)
  n = 0.002
FEATURE [App::DocumentObjectGroupPython] Cl_element023  label="Cl_element : 0.590"  # scripted group (container) (typed FeaturePython)
  n = 0.003
FEATURE [App::DocumentObjectGroupPython] K_element010  label="K_element : 0.001"  # scripted group (container) (typed FeaturePython)
  n = 0.001
FEATURE [App::DocumentObjectGroupPython] G4_SKIN_ICRP  # scripted group (container) (typed FeaturePython)
  Dunit = g/cm3
  Dvalue = 1.09
  Group = -> [H_element095,C_element103,N_element039,O_element088,Na_element013,P_element009,S_element020,Cl_element023,K_element010]
  conduct = 2
  density = 1
  expand = 3
  formula = G4_SKIN_ICRP
  name = G4_SKIN_ICRP
  specific = 4
FEATURE [App::DocumentObjectGroupPython] Na_element014  label="Na_element : 2"  # scripted group (container) (typed FeaturePython)
  n = 2
  ref = Na_element
FEATURE [App::DocumentObjectGroupPython] C_element104  label="C_element : 058"  # scripted group (container) (typed FeaturePython)
  n = 1
  ref = C_element
FEATURE [App::DocumentObjectGroupPython] O_element089  label="O_element : 049"  # scripted group (container) (typed FeaturePython)
  n = 3
  ref = O_element
FEATURE [App::DocumentObjectGroupPython] G4_SODIUM_CARBONATE  # scripted group (container) (typed FeaturePython)
  Dunit = g/cm3
  Dvalue = 2.532
  Group = -> [Na_element014,C_element104,O_element089]
  conduct = 2
  density = 1
  expand = 3
  formula = G4_SODIUM_CARBONATE
  name = G4_SODIUM_CARBONATE
  specific = 4
FEATURE [App::DocumentObjectGroupPython] Na_element015  label="Na_element : 1"  # scripted group (container) (typed FeaturePython)
  n = 1
  ref = Na_element
FEATURE [App::DocumentObjectGroupPython] I_element009  label="I_element : 005"  # scripted group (container) (typed FeaturePython)
  n = 1
  ref = I_element
FEATURE [App::DocumentObjectGroupPython] G4_SODIUM_IODIDE  # scripted group (container) (typed FeaturePython)
  Dunit = g/cm3
  Dvalue = 3.667
  Group = -> [Na_element015,I_element009]
  conduct = 2
  density = 1
  expand = 3
  formula = G4_SODIUM_IODIDE
  name = G4_SODIUM_IODIDE
  specific = 4
FEATURE [App::DocumentObjectGroupPython] Na_element016  label="Na_element : 003"  # scripted group (container) (typed FeaturePython)
  n = 2
  ref = Na_element
FEATURE [App::DocumentObjectGroupPython] O_element090  label="O_element : 050"  # scripted group (container) (typed FeaturePython)
  n = 1
  ref = O_element
FEATURE [App::DocumentObjectGroupPython] G4_SODIUM_MONOXIDE  # scripted group (container) (typed FeaturePython)
  Dunit = g/cm3
  Dvalue = 2.27
  Group = -> [Na_element016,O_element090]
  conduct = 2
  density = 1
  expand = 3
  formula = G4_SODIUM_MONOXIDE
  name = G4_SODIUM_MONOXIDE
  specific = 4
FEATURE [App::DocumentObjectGroupPython] Na_element017  label="Na_element : 004"  # scripted group (container) (typed FeaturePython)
  n = 1
  ref = Na_element
FEATURE [App::DocumentObjectGroupPython] N_element040  label="N_element : 018"  # scripted group (container) (typed FeaturePython)
  n = 1
  ref = N_element
FEATURE [App::DocumentObjectGroupPython] O_element091  label="O_element : 051"  # scripted group (container) (typed FeaturePython)
  n = 3
  ref = O_element
FEATURE [App::DocumentObjectGroupPython] G4_SODIUM_NITRATE  # scripted group (container) (typed FeaturePython)
  Dunit = g/cm3
  Dvalue = 2.261
  Group = -> [Na_element017,N_element040,O_element091]
  conduct = 2
  density = 1
  expand = 3
  formula = G4_SODIUM_NITRATE
  name = G4_SODIUM_NITRATE
  specific = 4
FEATURE [App::DocumentObjectGroupPython] C_element105  label="C_element : 059"  # scripted group (container) (typed FeaturePython)
  n = 14
  ref = C_element
FEATURE [App::DocumentObjectGroupPython] H_element096  label="H_element : 053"  # scripted group (container) (typed FeaturePython)
  n = 12
  ref = H_element
FEATURE [App::DocumentObjectGroupPython] G4_STILBENE  # scripted group (container) (typed FeaturePython)
  Dunit = g/cm3
  Dvalue = 0.9707
  Group = -> [C_element105,H_element096]
  conduct = 2
  density = 1
  expand = 3
  formula = G4_STILBENE
  name = G4_STILBENE
  specific = 4
FEATURE [App::DocumentObjectGroupPython] C_element106  label="C_element : 12"  # scripted group (container) (typed FeaturePython)
  n = 12
  ref = C_element
FEATURE [App::DocumentObjectGroupPython] H_element097  label="H_element : 22"  # scripted group (container) (typed FeaturePython)
  n = 22
  ref = H_element
FEATURE [App::DocumentObjectGroupPython] O_element092  label="O_element : 11"  # scripted group (container) (typed FeaturePython)
  n = 11
  ref = O_element
FEATURE [App::DocumentObjectGroupPython] G4_SUCROSE  # scripted group (container) (typed FeaturePython)
  Dunit = g/cm3
  Dvalue = 1.5805
  Group = -> [C_element106,H_element097,O_element092]
  conduct = 2
  density = 1
  expand = 3
  formula = G4_SUCROSE
  name = G4_SUCROSE
  specific = 4
FEATURE [App::DocumentObjectGroupPython] C_element107  label="C_element : 18"  # scripted group (container) (typed FeaturePython)
  n = 18
  ref = C_element
FEATURE [App::DocumentObjectGroupPython] H_element098  label="H_element : 054"  # scripted group (container) (typed FeaturePython)
  n = 14
  ref = H_element
FEATURE [App::DocumentObjectGroupPython] G4_TERPHENYL  # scripted group (container) (typed FeaturePython)
  Dunit = g/cm3
  Dvalue = 1.24
  Group = -> [C_element107,H_element098]
  conduct = 2
  density = 1
  expand = 3
  formula = G4_TERPHENYL
  name = G4_TERPHENYL
  specific = 4
FEATURE [App::DocumentObjectGroupPython] H_element099  label="H_element : 0.146"  # scripted group (container) (typed FeaturePython)
  n = 0.106
FEATURE [App::DocumentObjectGroupPython] C_element108  label="C_element : 0.883"  # scripted group (container) (typed FeaturePython)
  n = 0.099
FEATURE [App::DocumentObjectGroupPython] N_element041  label="N_element : 0.020"  # scripted group (container) (typed FeaturePython)
  n = 0.02
FEATURE [App::DocumentObjectGroupPython] O_element093  label="O_element : 0.766"  # scripted group (container) (typed FeaturePython)
  n = 0.766
FEATURE [App::DocumentObjectGroupPython] Na_element018  label="Na_element : 0.101"  # scripted group (container) (typed FeaturePython)
  n = 0.002
FEATURE [App::DocumentObjectGroupPython] P_element010  label="P_element : 0.108"  # scripted group (container) (typed FeaturePython)
  n = 0.001
FEATURE [App::DocumentObjectGroupPython] S_element021  label="S_element : 0.022"  # scripted group (container) (typed FeaturePython)
  n = 0.002
FEATURE [App::DocumentObjectGroupPython] Cl_element024  label="Cl_element : 0.002"  # scripted group (container) (typed FeaturePython)
  n = 0.002
FEATURE [App::DocumentObjectGroupPython] K_element011  label="K_element : 0.017"  # scripted group (container) (typed FeaturePython)
  n = 0.002
FEATURE [App::DocumentObjectGroupPython] G4_TESTIS_ICRP  # scripted group (container) (typed FeaturePython)
  Dunit = g/cm3
  Dvalue = 1.04
  Group = -> [H_element099,C_element108,N_element041,O_element093,Na_element018,P_element010,S_element021,Cl_element024,K_element011]
  conduct = 2
  density = 1
  expand = 3
  formula = G4_TESTIS_ICRP
  name = G4_TESTIS_ICRP
  specific = 4
FEATURE [App::DocumentObjectGroupPython] C_element109  label="C_element : 060"  # scripted group (container) (typed FeaturePython)
  n = 2
  ref = C_element
FEATURE [App::DocumentObjectGroupPython] Cl_element025  label="Cl_element : 012"  # scripted group (container) (typed FeaturePython)
  n = 4
  ref = Cl_element
FEATURE [App::DocumentObjectGroupPython] G4_TETRACHLOROETHYLENE  # scripted group (container) (typed FeaturePython)
  Dunit = g/cm3
  Dvalue = 1.625
  Group = -> [C_element109,Cl_element025]
  conduct = 2
  density = 1
  expand = 3
  formula = G4_TETRACHLOROETHYLENE
  name = G4_TETRACHLOROETHYLENE
  specific = 4
FEATURE [App::DocumentObjectGroupPython] Tl_element001  label="Tl_element : 1"  # scripted group (container) (typed FeaturePython)
  n = 1
  ref = Tl_element
FEATURE [App::DocumentObjectGroupPython] Cl_element026  label="Cl_element : 013"  # scripted group (container) (typed FeaturePython)
  n = 1
  ref = Cl_element
FEATURE [App::DocumentObjectGroupPython] G4_THALLIUM_CHLORIDE  # scripted group (container) (typed FeaturePython)
  Dunit = g/cm3
  Dvalue = 7.004
  Group = -> [Tl_element001,Cl_element026]
  conduct = 2
  density = 1
  expand = 3
  formula = G4_THALLIUM_CHLORIDE
  name = G4_THALLIUM_CHLORIDE
  specific = 4
FEATURE [App::DocumentObjectGroupPython] H_element100  label="H_element : 0.147"  # scripted group (container) (typed FeaturePython)
  n = 0.105
FEATURE [App::DocumentObjectGroupPython] C_element110  label="C_element : 0.256"  # scripted group (container) (typed FeaturePython)
  n = 0.256
FEATURE [App::DocumentObjectGroupPython] N_element042  label="N_element : 0.760"  # scripted group (container) (typed FeaturePython)
  n = 0.027
FEATURE [App::DocumentObjectGroupPython] O_element094  label="O_element : 0.602"  # scripted group (container) (typed FeaturePython)
  n = 0.602
FEATURE [App::DocumentObjectGroupPython] Na_element019  label="Na_element : 0.102"  # scripted group (container) (typed FeaturePython)
  n = 0.001
FEATURE [App::DocumentObjectGroupPython] P_element011  label="P_element : 0.109"  # scripted group (container) (typed FeaturePython)
  n = 0.002
FEATURE [App::DocumentObjectGroupPython] S_element022  label="S_element : 0.023"  # scripted group (container) (typed FeaturePython)
  n = 0.003
FEATURE [App::DocumentObjectGroupPython] Cl_element027  label="Cl_element : 0.591"  # scripted group (container) (typed FeaturePython)
  n = 0.002
FEATURE [App::DocumentObjectGroupPython] K_element012  label="K_element : 0.018"  # scripted group (container) (typed FeaturePython)
  n = 0.002
FEATURE [App::DocumentObjectGroupPython] G4_TISSUE_SOFT_ICRP  # scripted group (container) (typed FeaturePython)
  Dunit = g/cm3
  Dvalue = 1.03
  Group = -> [H_element100,C_element110,N_element042,O_element094,Na_element019,P_element011,S_element022,Cl_element027,K_element012]
  conduct = 2
  density = 1
  expand = 3
  formula = G4_TISSUE_SOFT_ICRP
  name = G4_TISSUE_SOFT_ICRP
  specific = 4
FEATURE [App::DocumentObjectGroupPython] H_element101  label="H_element : 0.148"  # scripted group (container) (typed FeaturePython)
  n = 0.101
FEATURE [App::DocumentObjectGroupPython] C_element111  label="C_element : 0.111"  # scripted group (container) (typed FeaturePython)
  n = 0.111
FEATURE [App::DocumentObjectGroupPython] N_element043  label="N_element : 0.026"  # scripted group (container) (typed FeaturePython)
  n = 0.026
FEATURE [App::DocumentObjectGroupPython] O_element095  label="O_element : 0.762"  # scripted group (container) (typed FeaturePython)
  n = 0.762
FEATURE [App::DocumentObjectGroupPython] G4_TISSUE_SOFT_ICRU_4  label="G4_TISSUE_SOFT_ICRU-4"  # scripted group (container) (typed FeaturePython)
  Dunit = g/cm3
  Dvalue = 1
  Group = -> [H_element101,C_element111,N_element043,O_element095]
  conduct = 2
  density = 1
  expand = 3
  formula = G4_TISSUE_SOFT_ICRU-4
  name = G4_TISSUE_SOFT_ICRU-4
  specific = 4
FEATURE [App::DocumentObjectGroupPython] H_element102  label="H_element : 0.149"  # scripted group (container) (typed FeaturePython)
  n = 0.101869
FEATURE [App::DocumentObjectGroupPython] C_element112  label="C_element : 0.456"  # scripted group (container) (typed FeaturePython)
  n = 0.456179
FEATURE [App::DocumentObjectGroupPython] N_element044  label="N_element : 0.761"  # scripted group (container) (typed FeaturePython)
  n = 0.035172
FEATURE [App::DocumentObjectGroupPython] O_element096  label="O_element : 0.407"  # scripted group (container) (typed FeaturePython)
  n = 0.40678
FEATURE [App::DocumentObjectGroupPython] G4_TISSUE_METHANE  label="G4_TISSUE-METHANE"  # scripted group (container) (typed FeaturePython)
  Dunit = g/cm3
  Dvalue = 0.00106409
  Group = -> [H_element102,C_element112,N_element044,O_element096]
  conduct = 2
  density = 1
  expand = 3
  formula = G4_TISSUE-METHANE
  name = G4_TISSUE-METHANE
  specific = 4
FEATURE [App::DocumentObjectGroupPython] H_element103  label="H_element : 0.103"  # scripted group (container) (typed FeaturePython)
  n = 0.102672
FEATURE [App::DocumentObjectGroupPython] C_element113  label="C_element : 0.569"  # scripted group (container) (typed FeaturePython)
  n = 0.56894
FEATURE [App::DocumentObjectGroupPython] N_element045  label="N_element : 0.762"  # scripted group (container) (typed FeaturePython)
  n = 0.035022
FEATURE [App::DocumentObjectGroupPython] O_element097  label="O_element : 0.293"  # scripted group (container) (typed FeaturePython)
  n = 0.293366
FEATURE [App::DocumentObjectGroupPython] G4_TISSUE_PROPANE  label="G4_TISSUE-PROPANE"  # scripted group (container) (typed FeaturePython)
  Dunit = g/cm3
  Dvalue = 0.00182628
  Group = -> [H_element103,C_element113,N_element045,O_element097]
  conduct = 2
  density = 1
  expand = 3
  formula = G4_TISSUE-PROPANE
  name = G4_TISSUE-PROPANE
  specific = 4
FEATURE [App::DocumentObjectGroupPython] Ti_element003  label="Ti_element : 1"  # scripted group (container) (typed FeaturePython)
  n = 1
  ref = Ti_element
FEATURE [App::DocumentObjectGroupPython] O_element098  label="O_element : 052"  # scripted group (container) (typed FeaturePython)
  n = 2
  ref = O_element
FEATURE [App::DocumentObjectGroupPython] G4_TITANIUM_DIOXIDE  # scripted group (container) (typed FeaturePython)
  Dunit = g/cm3
  Dvalue = 4.26
  Group = -> [Ti_element003,O_element098]
  conduct = 2
  density = 1
  expand = 3
  formula = G4_TITANIUM_DIOXIDE
  name = G4_TITANIUM_DIOXIDE
  specific = 4
FEATURE [App::DocumentObjectGroupPython] C_element114  label="C_element : 061"  # scripted group (container) (typed FeaturePython)
  n = 7
  ref = C_element
FEATURE [App::DocumentObjectGroupPython] H_element104  label="H_element : 055"  # scripted group (container) (typed FeaturePython)
  n = 8
  ref = H_element
FEATURE [App::DocumentObjectGroupPython] G4_TOLUENE  # scripted group (container) (typed FeaturePython)
  Dunit = g/cm3
  Dvalue = 0.8669
  Group = -> [C_element114,H_element104]
  conduct = 2
  density = 1
  expand = 3
  formula = G4_TOLUENE
  name = G4_TOLUENE
  specific = 4
FEATURE [App::DocumentObjectGroupPython] C_element115  label="C_element : 062"  # scripted group (container) (typed FeaturePython)
  n = 2
  ref = C_element
FEATURE [App::DocumentObjectGroupPython] H_element105  label="H_element : 056"  # scripted group (container) (typed FeaturePython)
  n = 1
  ref = H_element
FEATURE [App::DocumentObjectGroupPython] Cl_element028  label="Cl_element : 014"  # scripted group (container) (typed FeaturePython)
  n = 3
  ref = Cl_element
FEATURE [App::DocumentObjectGroupPython] G4_TRICHLOROETHYLENE  # scripted group (container) (typed FeaturePython)
  Dunit = g/cm3
  Dvalue = 1.46
  Group = -> [C_element115,H_element105,Cl_element028]
  conduct = 2
  density = 1
  expand = 3
  formula = G4_TRICHLOROETHYLENE
  name = G4_TRICHLOROETHYLENE
  specific = 4
FEATURE [App::DocumentObjectGroupPython] C_element116  label="C_element : 063"  # scripted group (container) (typed FeaturePython)
  n = 6
  ref = C_element
FEATURE [App::DocumentObjectGroupPython] H_element106  label="H_element : 15"  # scripted group (container) (typed FeaturePython)
  n = 15
  ref = H_element
FEATURE [App::DocumentObjectGroupPython] O_element099  label="O_element : 053"  # scripted group (container) (typed FeaturePython)
  n = 4
  ref = O_element
FEATURE [App::DocumentObjectGroupPython] P_element012  label="P_element : 1"  # scripted group (container) (typed FeaturePython)
  n = 1
  ref = P_element
FEATURE [App::DocumentObjectGroupPython] G4_TRIETHYL_PHOSPHATE  # scripted group (container) (typed FeaturePython)
  Dunit = g/cm3
  Dvalue = 1.07
  Group = -> [C_element116,H_element106,O_element099,P_element012]
  conduct = 2
  density = 1
  expand = 3
  formula = G4_TRIETHYL_PHOSPHATE
  name = G4_TRIETHYL_PHOSPHATE
  specific = 4
FEATURE [App::DocumentObjectGroupPython] W_element003  label="W_element : 003"  # scripted group (container) (typed FeaturePython)
  n = 1
  ref = W_element
FEATURE [App::DocumentObjectGroupPython] F_element017  label="F_element : 6"  # scripted group (container) (typed FeaturePython)
  n = 6
  ref = F_element
FEATURE [App::DocumentObjectGroupPython] G4_TUNGSTEN_HEXAFLUORIDE  # scripted group (container) (typed FeaturePython)
  Dunit = g/cm3
  Dvalue = 2.4
  Group = -> [W_element003,F_element017]
  conduct = 2
  density = 1
  expand = 3
  formula = G4_TUNGSTEN_HEXAFLUORIDE
  name = G4_TUNGSTEN_HEXAFLUORIDE
  specific = 4
FEATURE [App::DocumentObjectGroupPython] U_element001  label="U_element : 1"  # scripted group (container) (typed FeaturePython)
  n = 1
  ref = U_element
FEATURE [App::DocumentObjectGroupPython] C_element117  label="C_element : 064"  # scripted group (container) (typed FeaturePython)
  n = 2
  ref = C_element
FEATURE [App::DocumentObjectGroupPython] G4_URANIUM_DICARBIDE  # scripted group (container) (typed FeaturePython)
  Dunit = g/cm3
  Dvalue = 11.28
  Group = -> [U_element001,C_element117]
  conduct = 2
  density = 1
  expand = 3
  formula = G4_URANIUM_DICARBIDE
  name = G4_URANIUM_DICARBIDE
  specific = 4
FEATURE [App::DocumentObjectGroupPython] U_element002  label="U_element : 002"  # scripted group (container) (typed FeaturePython)
  n = 1
  ref = U_element
FEATURE [App::DocumentObjectGroupPython] C_element118  label="C_element : 065"  # scripted group (container) (typed FeaturePython)
  n = 1
  ref = C_element
FEATURE [App::DocumentObjectGroupPython] G4_URANIUM_MONOCARBIDE  # scripted group (container) (typed FeaturePython)
  Dunit = g/cm3
  Dvalue = 13.63
  Group = -> [U_element002,C_element118]
  conduct = 2
  density = 1
  expand = 3
  formula = G4_URANIUM_MONOCARBIDE
  name = G4_URANIUM_MONOCARBIDE
  specific = 4
FEATURE [App::DocumentObjectGroupPython] U_element003  label="U_element : 003"  # scripted group (container) (typed FeaturePython)
  n = 1
  ref = U_element
FEATURE [App::DocumentObjectGroupPython] O_element100  label="O_element : 054"  # scripted group (container) (typed FeaturePython)
  n = 2
  ref = O_element
FEATURE [App::DocumentObjectGroupPython] G4_URANIUM_OXIDE  # scripted group (container) (typed FeaturePython)
  Dunit = g/cm3
  Dvalue = 10.96
  Group = -> [U_element003,O_element100]
  conduct = 2
  density = 1
  expand = 3
  formula = G4_URANIUM_OXIDE
  name = G4_URANIUM_OXIDE
  specific = 4
FEATURE [App::DocumentObjectGroupPython] C_element119  label="C_element : 066"  # scripted group (container) (typed FeaturePython)
  n = 1
  ref = C_element
FEATURE [App::DocumentObjectGroupPython] H_element107  label="H_element : 057"  # scripted group (container) (typed FeaturePython)
  n = 4
  ref = H_element
FEATURE [App::DocumentObjectGroupPython] N_element046  label="N_element : 019"  # scripted group (container) (typed FeaturePython)
  n = 2
  ref = N_element
FEATURE [App::DocumentObjectGroupPython] O_element101  label="O_element : 055"  # scripted group (container) (typed FeaturePython)
  n = 1
  ref = O_element
FEATURE [App::DocumentObjectGroupPython] G4_UREA  # scripted group (container) (typed FeaturePython)
  Dunit = g/cm3
  Dvalue = 1.323
  Group = -> [C_element119,H_element107,N_element046,O_element101]
  conduct = 2
  density = 1
  expand = 3
  formula = G4_UREA
  name = G4_UREA
  specific = 4
FEATURE [App::DocumentObjectGroupPython] C_element120  label="C_element : 067"  # scripted group (container) (typed FeaturePython)
  n = 5
  ref = C_element
FEATURE [App::DocumentObjectGroupPython] H_element108  label="H_element : 058"  # scripted group (container) (typed FeaturePython)
  n = 11
  ref = H_element
FEATURE [App::DocumentObjectGroupPython] N_element047  label="N_element : 020"  # scripted group (container) (typed FeaturePython)
  n = 1
  ref = N_element
FEATURE [App::DocumentObjectGroupPython] O_element102  label="O_element : 056"  # scripted group (container) (typed FeaturePython)
  n = 2
  ref = O_element
FEATURE [App::DocumentObjectGroupPython] G4_VALINE  # scripted group (container) (typed FeaturePython)
  Dunit = g/cm3
  Dvalue = 1.23
  Group = -> [C_element120,H_element108,N_element047,O_element102]
  conduct = 2
  density = 1
  expand = 3
  formula = G4_VALINE
  name = G4_VALINE
  specific = 4
FEATURE [App::DocumentObjectGroupPython] H_element109  label="H_element : 0.009"  # scripted group (container) (typed FeaturePython)
  n = 0.009417
FEATURE [App::DocumentObjectGroupPython] C_element121  label="C_element : 0.281"  # scripted group (container) (typed FeaturePython)
  n = 0.280555
FEATURE [App::DocumentObjectGroupPython] F_element018  label="F_element : 0.710"  # scripted group (container) (typed FeaturePython)
  n = 0.710028
FEATURE [App::DocumentObjectGroupPython] G4_VITON  # scripted group (container) (typed FeaturePython)
  Dunit = g/cm3
  Dvalue = 1.8
  Group = -> [H_element109,C_element121,F_element018]
  conduct = 2
  density = 1
  expand = 3
  formula = G4_VITON
  name = G4_VITON
  specific = 4
FEATURE [App::DocumentObjectGroupPython] H_element110  label="H_element : 059"  # scripted group (container) (typed FeaturePython)
  n = 2
  ref = H_element
FEATURE [App::DocumentObjectGroupPython] O_element103  label="O_element : 057"  # scripted group (container) (typed FeaturePython)
  n = 1
  ref = O_element
FEATURE [App::DocumentObjectGroupPython] G4_WATER  # scripted group (container) (typed FeaturePython)
  Dunit = g/cm3
  Dvalue = 1
  Group = -> [H_element110,O_element103]
  conduct = 2
  density = 1
  expand = 3
  formula = G4_WATER
  name = G4_WATER
  specific = 4
FEATURE [App::DocumentObjectGroupPython] H_element111  label="H_element : 060"  # scripted group (container) (typed FeaturePython)
  n = 2
  ref = H_element
FEATURE [App::DocumentObjectGroupPython] O_element104  label="O_element : 058"  # scripted group (container) (typed FeaturePython)
  n = 1
  ref = O_element
FEATURE [App::DocumentObjectGroupPython] G4_WATER_VAPOR  # scripted group (container) (typed FeaturePython)
  Dunit = g/cm3
  Dvalue = 0.000756182
  Group = -> [H_element111,O_element104]
  conduct = 2
  density = 1
  expand = 3
  formula = G4_WATER_VAPOR
  name = G4_WATER_VAPOR
  specific = 4
FEATURE [App::DocumentObjectGroupPython] C_element122  label="C_element : 068"  # scripted group (container) (typed FeaturePython)
  n = 8
  ref = C_element
FEATURE [App::DocumentObjectGroupPython] H_element112  label="H_element : 061"  # scripted group (container) (typed FeaturePython)
  n = 10
  ref = H_element
FEATURE [App::DocumentObjectGroupPython] G4_XYLENE  # scripted group (container) (typed FeaturePython)
  Dunit = g/cm3
  Dvalue = 0.87
  Group = -> [C_element122,H_element112]
  conduct = 2
  density = 1
  expand = 3
  formula = G4_XYLENE
  name = G4_XYLENE
  specific = 4
FEATURE [App::DocumentObjectGroupPython] C_element123  label="C_element : 069"  # scripted group (container) (typed FeaturePython)
  n = 1
  ref = C_element
FEATURE [App::DocumentObjectGroupPython] G4_GRAPHITE  # scripted group (container) (typed FeaturePython)
  Dunit = g/cm3
  Dvalue = 2.21
  Group = -> [C_element123]
  conduct = 2
  density = 1
  expand = 3
  formula = G4_GRAPHITE
  name = G4_GRAPHITE
  specific = 4
FEATURE [App::DocumentObjectGroupPython] NIST  # scripted group (container) (typed FeaturePython)
  Group = -> [G4_A_150_TISSUE,G4_ACETONE,G4_ACETYLENE,G4_ADENINE,G4_ADIPOSE_TISSUE_ICRP,G4_AIR,G4_ALANINE,G4_ALUMINUM_OXIDE,G4_AMBER,G4_AMMONIA,G4_ANILINE,G4_ANTHRACENE,G4_B_100_BONE,G4_BAKELITE,G4_BARIUM_FLUORIDE,G4_BARIUM_SULFATE,G4_BENZENE,G4_BERYLLIUM_OXIDE,G4_BGO,G4_BLOOD_ICRP,G4_BONE_COMPACT_ICRU,G4_BONE_CORTICAL_ICRP,G4_BORON_CARBIDE,G4_BORON_OXIDE,G4_BRAIN_ICRP,G4_BUTANE,G4_N_BUTYL_ALCOHOL,G4_C_552,+152 more]
FEATURE [App::DocumentObjectGroupPython] H_element113  label="H_element : 062"  # scripted group (container) (typed FeaturePython)
  n = 1
  ref = H_element
FEATURE [App::DocumentObjectGroupPython] G4_H  # scripted group (container) (typed FeaturePython)
  Dunit = g/cm3
  Dvalue = 8.3748e-05
  Group = -> [H_element113]
  conduct = 2
  density = 1
  expand = 3
  formula = H
  name = G4_H
  specific = 4
FEATURE [App::DocumentObjectGroupPython] He_element001  label="He_element : 1"  # scripted group (container) (typed FeaturePython)
  n = 1
  ref = He_element
FEATURE [App::DocumentObjectGroupPython] G4_He  # scripted group (container) (typed FeaturePython)
  Dunit = g/cm3
  Dvalue = 0.000166322
  Group = -> [He_element001]
  conduct = 2
  density = 1
  expand = 3
  formula = He
  name = G4_He
  specific = 4
FEATURE [App::DocumentObjectGroupPython] Li_element008  label="Li_element : 008"  # scripted group (container) (typed FeaturePython)
  n = 1
  ref = Li_element
FEATURE [App::DocumentObjectGroupPython] G4_Li  # scripted group (container) (typed FeaturePython)
  Dunit = g/cm3
  Dvalue = 0.534
  Group = -> [Li_element008]
  conduct = 2
  density = 1
  expand = 3
  formula = Li
  name = G4_Li
  specific = 4
FEATURE [App::DocumentObjectGroupPython] Be_element002  label="Be_element : 002"  # scripted group (container) (typed FeaturePython)
  n = 1
  ref = Be_element
FEATURE [App::DocumentObjectGroupPython] G4_Be  # scripted group (container) (typed FeaturePython)
  Dunit = g/cm3
  Dvalue = 1.848
  Group = -> [Be_element002]
  conduct = 2
  density = 1
  expand = 3
  formula = Be
  name = G4_Be
  specific = 4
FEATURE [App::DocumentObjectGroupPython] B_element007  label="B_element : 007"  # scripted group (container) (typed FeaturePython)
  n = 1
  ref = B_element
FEATURE [App::DocumentObjectGroupPython] G4_B  # scripted group (container) (typed FeaturePython)
  Dunit = g/cm3
  Dvalue = 2.37
  Group = -> [B_element007]
  conduct = 2
  density = 1
  expand = 3
  formula = B
  name = G4_B
  specific = 4
FEATURE [App::DocumentObjectGroupPython] C_element124  label="C_element : 070"  # scripted group (container) (typed FeaturePython)
  n = 1
  ref = C_element
FEATURE [App::DocumentObjectGroupPython] G4_C  # scripted group (container) (typed FeaturePython)
  Dunit = g/cm3
  Dvalue = 2
  Group = -> [C_element124]
  conduct = 2
  density = 1
  expand = 3
  formula = C
  name = G4_C
  specific = 4
FEATURE [App::DocumentObjectGroupPython] N_element048  label="N_element : 021"  # scripted group (container) (typed FeaturePython)
  n = 1
  ref = N_element
FEATURE [App::DocumentObjectGroupPython] G4_N  # scripted group (container) (typed FeaturePython)
  Dunit = g/cm3
  Dvalue = 0.0011652
  Group = -> [N_element048]
  conduct = 2
  density = 1
  expand = 3
  formula = N
  name = G4_N
  specific = 4
FEATURE [App::DocumentObjectGroupPython] O_element105  label="O_element : 059"  # scripted group (container) (typed FeaturePython)
  n = 1
  ref = O_element
FEATURE [App::DocumentObjectGroupPython] G4_O  # scripted group (container) (typed FeaturePython)
  Dunit = g/cm3
  Dvalue = 0.00133151
  Group = -> [O_element105]
  conduct = 2
  density = 1
  expand = 3
  formula = O
  name = G4_O
  specific = 4
FEATURE [App::DocumentObjectGroupPython] F_element019  label="F_element : 008"  # scripted group (container) (typed FeaturePython)
  n = 1
  ref = F_element
FEATURE [App::DocumentObjectGroupPython] G4_F  # scripted group (container) (typed FeaturePython)
  Dunit = g/cm3
  Dvalue = 0.00158029
  Group = -> [F_element019]
  conduct = 2
  density = 1
  expand = 3
  formula = F
  name = G4_F
  specific = 4
FEATURE [App::DocumentObjectGroupPython] Ne_element001  label="Ne_element : 1"  # scripted group (container) (typed FeaturePython)
  n = 1
  ref = Ne_element
FEATURE [App::DocumentObjectGroupPython] G4_Ne  # scripted group (container) (typed FeaturePython)
  Dunit = g/cm3
  Dvalue = 0.000838505
  Group = -> [Ne_element001]
  conduct = 2
  density = 1
  expand = 3
  formula = Ne
  name = G4_Ne
  specific = 4
FEATURE [App::DocumentObjectGroupPython] Na_element020  label="Na_element : 005"  # scripted group (container) (typed FeaturePython)
  n = 1
  ref = Na_element
FEATURE [App::DocumentObjectGroupPython] G4_Na  # scripted group (container) (typed FeaturePython)
  Dunit = g/cm3
  Dvalue = 0.971
  Group = -> [Na_element020]
  conduct = 2
  density = 1
  expand = 3
  formula = Na
  name = G4_Na
  specific = 4
FEATURE [App::DocumentObjectGroupPython] Mg_element011  label="Mg_element : 005"  # scripted group (container) (typed FeaturePython)
  n = 1
  ref = Mg_element
FEATURE [App::DocumentObjectGroupPython] G4_Mg  # scripted group (container) (typed FeaturePython)
  Dunit = g/cm3
  Dvalue = 1.74
  Group = -> [Mg_element011]
  conduct = 2
  density = 1
  expand = 3
  formula = Mg
  name = G4_Mg
  specific = 4
FEATURE [App::DocumentObjectGroupPython] Al_element004  label="Al_element : 1"  # scripted group (container) (typed FeaturePython)
  n = 1
  ref = Al_element
FEATURE [App::DocumentObjectGroupPython] G4_Al  # scripted group (container) (typed FeaturePython)
  Dunit = g/cm3
  Dvalue = 2.699
  Group = -> [Al_element004]
  conduct = 2
  density = 1
  expand = 3
  formula = Al
  name = G4_Al
  specific = 4
FEATURE [App::DocumentObjectGroupPython] Si_element007  label="Si_element : 002"  # scripted group (container) (typed FeaturePython)
  n = 1
  ref = Si_element
FEATURE [App::DocumentObjectGroupPython] G4_Si  # scripted group (container) (typed FeaturePython)
  Dunit = g/cm3
  Dvalue = 2.33
  Group = -> [Si_element007]
  conduct = 2
  density = 1
  expand = 3
  formula = Si
  name = G4_Si
  specific = 4
FEATURE [App::DocumentObjectGroupPython] P_element013  label="P_element : 002"  # scripted group (container) (typed FeaturePython)
  n = 1
  ref = P_element
FEATURE [App::DocumentObjectGroupPython] G4_P  # scripted group (container) (typed FeaturePython)
  Dunit = g/cm3
  Dvalue = 2.2
  Group = -> [P_element013]
  conduct = 2
  density = 1
  expand = 3
  formula = P
  name = G4_P
  specific = 4
FEATURE [App::DocumentObjectGroupPython] S_element023  label="S_element : 007"  # scripted group (container) (typed FeaturePython)
  n = 1
  ref = S_element
FEATURE [App::DocumentObjectGroupPython] G4_S  # scripted group (container) (typed FeaturePython)
  Dunit = g/cm3
  Dvalue = 2
  Group = -> [S_element023]
  conduct = 2
  density = 1
  expand = 3
  formula = S
  name = G4_S
  specific = 4
FEATURE [App::DocumentObjectGroupPython] Cl_element029  label="Cl_element : 015"  # scripted group (container) (typed FeaturePython)
  n = 1
  ref = Cl_element
FEATURE [App::DocumentObjectGroupPython] G4_Cl  # scripted group (container) (typed FeaturePython)
  Dunit = g/cm3
  Dvalue = 0.00299473
  Group = -> [Cl_element029]
  conduct = 2
  density = 1
  expand = 3
  formula = Cl
  name = G4_Cl
  specific = 4
FEATURE [App::DocumentObjectGroupPython] Ar_element002  label="Ar_element : 1"  # scripted group (container) (typed FeaturePython)
  n = 1
  ref = Ar_element
FEATURE [App::DocumentObjectGroupPython] G4_Ar  # scripted group (container) (typed FeaturePython)
  Dunit = g/cm3
  Dvalue = 0.00166201
  Group = -> [Ar_element002]
  conduct = 2
  density = 1
  expand = 3
  formula = Ar
  name = G4_Ar
  specific = 4
FEATURE [App::DocumentObjectGroupPython] K_element013  label="K_element : 003"  # scripted group (container) (typed FeaturePython)
  n = 1
  ref = K_element
FEATURE [App::DocumentObjectGroupPython] G4_K  # scripted group (container) (typed FeaturePython)
  Dunit = g/cm3
  Dvalue = 0.862
  Group = -> [K_element013]
  conduct = 2
  density = 1
  expand = 3
  formula = K
  name = G4_K
  specific = 4
FEATURE [App::DocumentObjectGroupPython] Ca_element014  label="Ca_element : 007"  # scripted group (container) (typed FeaturePython)
  n = 1
  ref = Ca_element
FEATURE [App::DocumentObjectGroupPython] G4_Ca  # scripted group (container) (typed FeaturePython)
  Dunit = g/cm3
  Dvalue = 1.55
  Group = -> [Ca_element014]
  conduct = 2
  density = 1
  expand = 3
  formula = Ca
  name = G4_Ca
  specific = 4
FEATURE [App::DocumentObjectGroupPython] Sc_element001  label="Sc_element : 1"  # scripted group (container) (typed FeaturePython)
  n = 1
  ref = Sc_element
FEATURE [App::DocumentObjectGroupPython] G4_Sc  # scripted group (container) (typed FeaturePython)
  Dunit = g/cm3
  Dvalue = 2.989
  Group = -> [Sc_element001]
  conduct = 2
  density = 1
  expand = 3
  formula = Sc
  name = G4_Sc
  specific = 4
FEATURE [App::DocumentObjectGroupPython] Ti_element004  label="Ti_element : 002"  # scripted group (container) (typed FeaturePython)
  n = 1
  ref = Ti_element
FEATURE [App::DocumentObjectGroupPython] G4_Ti  # scripted group (container) (typed FeaturePython)
  Dunit = g/cm3
  Dvalue = 4.54
  Group = -> [Ti_element004]
  conduct = 2
  density = 1
  expand = 3
  formula = Ti
  name = G4_Ti
  specific = 4
FEATURE [App::DocumentObjectGroupPython] V_element001  label="V_element : 1"  # scripted group (container) (typed FeaturePython)
  n = 1
  ref = V_element
FEATURE [App::DocumentObjectGroupPython] G4_V  # scripted group (container) (typed FeaturePython)
  Dunit = g/cm3
  Dvalue = 6.11
  Group = -> [V_element001]
  conduct = 2
  density = 1
  expand = 3
  formula = V
  name = G4_V
  specific = 4
FEATURE [App::DocumentObjectGroupPython] Cr_element001  label="Cr_element : 1"  # scripted group (container) (typed FeaturePython)
  n = 1
  ref = Cr_element
FEATURE [App::DocumentObjectGroupPython] G4_Cr  # scripted group (container) (typed FeaturePython)
  Dunit = g/cm3
  Dvalue = 7.18
  Group = -> [Cr_element001]
  conduct = 2
  density = 1
  expand = 3
  formula = Cr
  name = G4_Cr
  specific = 4
FEATURE [App::DocumentObjectGroupPython] Mn_element001  label="Mn_element : 1"  # scripted group (container) (typed FeaturePython)
  n = 1
  ref = Mn_element
FEATURE [App::DocumentObjectGroupPython] G4_Mn  # scripted group (container) (typed FeaturePython)
  Dunit = g/cm3
  Dvalue = 7.44
  Group = -> [Mn_element001]
  conduct = 2
  density = 1
  expand = 3
  formula = Mn
  name = G4_Mn
  specific = 4
FEATURE [App::DocumentObjectGroupPython] Fe_element007  label="Fe_element : 004"  # scripted group (container) (typed FeaturePython)
  n = 1
  ref = Fe_element
FEATURE [App::DocumentObjectGroupPython] G4_Fe  # scripted group (container) (typed FeaturePython)
  Dunit = g/cm3
  Dvalue = 7.874
  Group = -> [Fe_element007]
  conduct = 2
  density = 1
  expand = 3
  formula = Fe
  name = G4_Fe
  specific = 4
FEATURE [App::DocumentObjectGroupPython] Co_element001  label="Co_element : 1"  # scripted group (container) (typed FeaturePython)
  n = 1
  ref = Co_element
FEATURE [App::DocumentObjectGroupPython] G4_Co  # scripted group (container) (typed FeaturePython)
  Dunit = g/cm3
  Dvalue = 8.9
  Group = -> [Co_element001]
  conduct = 2
  density = 1
  expand = 3
  formula = Co
  name = G4_Co
  specific = 4
FEATURE [App::DocumentObjectGroupPython] Ni_element001  label="Ni_element : 1"  # scripted group (container) (typed FeaturePython)
  n = 1
  ref = Ni_element
FEATURE [App::DocumentObjectGroupPython] G4_Ni  # scripted group (container) (typed FeaturePython)
  Dunit = g/cm3
  Dvalue = 8.902
  Group = -> [Ni_element001]
  conduct = 2
  density = 1
  expand = 3
  formula = Ni
  name = G4_Ni
  specific = 4
FEATURE [App::DocumentObjectGroupPython] Cu_element001  label="Cu_element : 1"  # scripted group (container) (typed FeaturePython)
  n = 1
  ref = Cu_element
FEATURE [App::DocumentObjectGroupPython] G4_Cu  # scripted group (container) (typed FeaturePython)
  Dunit = g/cm3
  Dvalue = 8.96
  Group = -> [Cu_element001]
  conduct = 2
  density = 1
  expand = 3
  formula = Cu
  name = G4_Cu
  specific = 4
FEATURE [App::DocumentObjectGroupPython] Zn_element001  label="Zn_element : 1"  # scripted group (container) (typed FeaturePython)
  n = 1
  ref = Zn_element
FEATURE [App::DocumentObjectGroupPython] G4_Zn  # scripted group (container) (typed FeaturePython)
  Dunit = g/cm3
  Dvalue = 7.133
  Group = -> [Zn_element001]
  conduct = 2
  density = 1
  expand = 3
  formula = Zn
  name = G4_Zn
  specific = 4
FEATURE [App::DocumentObjectGroupPython] Ga_element002  label="Ga_element : 002"  # scripted group (container) (typed FeaturePython)
  n = 1
  ref = Ga_element
FEATURE [App::DocumentObjectGroupPython] G4_Ga  # scripted group (container) (typed FeaturePython)
  Dunit = g/cm3
  Dvalue = 5.904
  Group = -> [Ga_element002]
  conduct = 2
  density = 1
  expand = 3
  formula = Ga
  name = G4_Ga
  specific = 4
FEATURE [App::DocumentObjectGroupPython] Ge_element002  label="Ge_element : 1"  # scripted group (container) (typed FeaturePython)
  n = 1
  ref = Ge_element
FEATURE [App::DocumentObjectGroupPython] G4_Ge  # scripted group (container) (typed FeaturePython)
  Dunit = g/cm3
  Dvalue = 5.323
  Group = -> [Ge_element002]
  conduct = 2
  density = 1
  expand = 3
  formula = Ge
  name = G4_Ge
  specific = 4
FEATURE [App::DocumentObjectGroupPython] As_element003  label="As_element : 002"  # scripted group (container) (typed FeaturePython)
  n = 1
  ref = As_element
FEATURE [App::DocumentObjectGroupPython] G4_As  # scripted group (container) (typed FeaturePython)
  Dunit = g/cm3
  Dvalue = 5.73
  Group = -> [As_element003]
  conduct = 2
  density = 1
  expand = 3
  formula = As
  name = G4_As
  specific = 4
FEATURE [App::DocumentObjectGroupPython] Se_element001  label="Se_element : 1"  # scripted group (container) (typed FeaturePython)
  n = 1
  ref = Se_element
FEATURE [App::DocumentObjectGroupPython] G4_Se  # scripted group (container) (typed FeaturePython)
  Dunit = g/cm3
  Dvalue = 4.5
  Group = -> [Se_element001]
  conduct = 2
  density = 1
  expand = 3
  formula = Se
  name = G4_Se
  specific = 4
FEATURE [App::DocumentObjectGroupPython] Br_element007  label="Br_element : 004"  # scripted group (container) (typed FeaturePython)
  n = 1
  ref = Br_element
FEATURE [App::DocumentObjectGroupPython] G4_Br  # scripted group (container) (typed FeaturePython)
  Dunit = g/cm3
  Dvalue = 0.0070721
  Group = -> [Br_element007]
  conduct = 2
  density = 1
  expand = 3
  formula = Br
  name = G4_Br
  specific = 4
FEATURE [App::DocumentObjectGroupPython] Kr_element001  label="Kr_element : 1"  # scripted group (container) (typed FeaturePython)
  n = 1
  ref = Kr_element
FEATURE [App::DocumentObjectGroupPython] G4_Kr  # scripted group (container) (typed FeaturePython)
  Dunit = g/cm3
  Dvalue = 0.00347832
  Group = -> [Kr_element001]
  conduct = 2
  density = 1
  expand = 3
  formula = Kr
  name = G4_Kr
  specific = 4
FEATURE [App::DocumentObjectGroupPython] Rb_element001  label="Rb_element : 1"  # scripted group (container) (typed FeaturePython)
  n = 1
  ref = Rb_element
FEATURE [App::DocumentObjectGroupPython] G4_Rb  # scripted group (container) (typed FeaturePython)
  Dunit = g/cm3
  Dvalue = 1.532
  Group = -> [Rb_element001]
  conduct = 2
  density = 1
  expand = 3
  formula = Rb
  name = G4_Rb
  specific = 4
FEATURE [App::DocumentObjectGroupPython] Sr_element001  label="Sr_element : 1"  # scripted group (container) (typed FeaturePython)
  n = 1
  ref = Sr_element
FEATURE [App::DocumentObjectGroupPython] G4_Sr  # scripted group (container) (typed FeaturePython)
  Dunit = g/cm3
  Dvalue = 2.54
  Group = -> [Sr_element001]
  conduct = 2
  density = 1
  expand = 3
  formula = Sr
  name = G4_Sr
  specific = 4
FEATURE [App::DocumentObjectGroupPython] Y_element001  label="Y_element : 1"  # scripted group (container) (typed FeaturePython)
  n = 1
  ref = Y_element
FEATURE [App::DocumentObjectGroupPython] G4_Y  # scripted group (container) (typed FeaturePython)
  Dunit = g/cm3
  Dvalue = 4.469
  Group = -> [Y_element001]
  conduct = 2
  density = 1
  expand = 3
  formula = Y
  name = G4_Y
  specific = 4
FEATURE [App::DocumentObjectGroupPython] Zr_element001  label="Zr_element : 1"  # scripted group (container) (typed FeaturePython)
  n = 1
  ref = Zr_element
FEATURE [App::DocumentObjectGroupPython] G4_Zr  # scripted group (container) (typed FeaturePython)
  Dunit = g/cm3
  Dvalue = 6.506
  Group = -> [Zr_element001]
  conduct = 2
  density = 1
  expand = 3
  formula = Zr
  name = G4_Zr
  specific = 4
FEATURE [App::DocumentObjectGroupPython] Nb_element001  label="Nb_element : 1"  # scripted group (container) (typed FeaturePython)
  n = 1
  ref = Nb_element
FEATURE [App::DocumentObjectGroupPython] G4_Nb  # scripted group (container) (typed FeaturePython)
  Dunit = g/cm3
  Dvalue = 8.57
  Group = -> [Nb_element001]
  conduct = 2
  density = 1
  expand = 3
  formula = Nb
  name = G4_Nb
  specific = 4
FEATURE [App::DocumentObjectGroupPython] Mo_element001  label="Mo_element : 1"  # scripted group (container) (typed FeaturePython)
  n = 1
  ref = Mo_element
FEATURE [App::DocumentObjectGroupPython] G4_Mo  # scripted group (container) (typed FeaturePython)
  Dunit = g/cm3
  Dvalue = 10.22
  Group = -> [Mo_element001]
  conduct = 2
  density = 1
  expand = 3
  formula = Mo
  name = G4_Mo
  specific = 4
FEATURE [App::DocumentObjectGroupPython] Tc_element001  label="Tc_element : 1"  # scripted group (container) (typed FeaturePython)
  n = 1
  ref = Tc_element
FEATURE [App::DocumentObjectGroupPython] G4_Tc  # scripted group (container) (typed FeaturePython)
  Dunit = g/cm3
  Dvalue = 11.5
  Group = -> [Tc_element001]
  conduct = 2
  density = 1
  expand = 3
  formula = Tc
  name = G4_Tc
  specific = 4
FEATURE [App::DocumentObjectGroupPython] Ru_element001  label="Ru_element : 1"  # scripted group (container) (typed FeaturePython)
  n = 1
  ref = Ru_element
FEATURE [App::DocumentObjectGroupPython] G4_Ru  # scripted group (container) (typed FeaturePython)
  Dunit = g/cm3
  Dvalue = 12.41
  Group = -> [Ru_element001]
  conduct = 2
  density = 1
  expand = 3
  formula = Ru
  name = G4_Ru
  specific = 4
FEATURE [App::DocumentObjectGroupPython] Rh_element001  label="Rh_element : 1"  # scripted group (container) (typed FeaturePython)
  n = 1
  ref = Rh_element
FEATURE [App::DocumentObjectGroupPython] G4_Rh  # scripted group (container) (typed FeaturePython)
  Dunit = g/cm3
  Dvalue = 12.41
  Group = -> [Rh_element001]
  conduct = 2
  density = 1
  expand = 3
  formula = Rh
  name = G4_Rh
  specific = 4
FEATURE [App::DocumentObjectGroupPython] Pd_element001  label="Pd_element : 1"  # scripted group (container) (typed FeaturePython)
  n = 1
  ref = Pd_element
FEATURE [App::DocumentObjectGroupPython] G4_Pd  # scripted group (container) (typed FeaturePython)
  Dunit = g/cm3
  Dvalue = 12.02
  Group = -> [Pd_element001]
  conduct = 2
  density = 1
  expand = 3
  formula = Pd
  name = G4_Pd
  specific = 4
FEATURE [App::DocumentObjectGroupPython] Ag_element006  label="Ag_element : 004"  # scripted group (container) (typed FeaturePython)
  n = 1
  ref = Ag_element
FEATURE [App::DocumentObjectGroupPython] G4_Ag  # scripted group (container) (typed FeaturePython)
  Dunit = g/cm3
  Dvalue = 10.5
  Group = -> [Ag_element006]
  conduct = 2
  density = 1
  expand = 3
  formula = Ag
  name = G4_Ag
  specific = 4
FEATURE [App::DocumentObjectGroupPython] Cd_element003  label="Cd_element : 003"  # scripted group (container) (typed FeaturePython)
  n = 1
  ref = Cd_element
FEATURE [App::DocumentObjectGroupPython] G4_Cd  # scripted group (container) (typed FeaturePython)
  Dunit = g/cm3
  Dvalue = 8.65
  Group = -> [Cd_element003]
  conduct = 2
  density = 1
  expand = 3
  formula = Cd
  name = G4_Cd
  specific = 4
FEATURE [App::DocumentObjectGroupPython] In_element001  label="In_element : 1"  # scripted group (container) (typed FeaturePython)
  n = 1
  ref = In_element
FEATURE [App::DocumentObjectGroupPython] G4_In  # scripted group (container) (typed FeaturePython)
  Dunit = g/cm3
  Dvalue = 7.31
  Group = -> [In_element001]
  conduct = 2
  density = 1
  expand = 3
  formula = In
  name = G4_In
  specific = 4
FEATURE [App::DocumentObjectGroupPython] Sn_element001  label="Sn_element : 1"  # scripted group (container) (typed FeaturePython)
  n = 1
  ref = Sn_element
FEATURE [App::DocumentObjectGroupPython] G4_Sn  # scripted group (container) (typed FeaturePython)
  Dunit = g/cm3
  Dvalue = 7.31
  Group = -> [Sn_element001]
  conduct = 2
  density = 1
  expand = 3
  formula = Sn
  name = G4_Sn
  specific = 4
FEATURE [App::DocumentObjectGroupPython] Sb_element001  label="Sb_element : 1"  # scripted group (container) (typed FeaturePython)
  n = 1
  ref = Sb_element
FEATURE [App::DocumentObjectGroupPython] G4_Sb  # scripted group (container) (typed FeaturePython)
  Dunit = g/cm3
  Dvalue = 6.691
  Group = -> [Sb_element001]
  conduct = 2
  density = 1
  expand = 3
  formula = Sb
  name = G4_Sb
  specific = 4
FEATURE [App::DocumentObjectGroupPython] Te_element002  label="Te_element : 002"  # scripted group (container) (typed FeaturePython)
  n = 1
  ref = Te_element
FEATURE [App::DocumentObjectGroupPython] G4_Te  # scripted group (container) (typed FeaturePython)
  Dunit = g/cm3
  Dvalue = 6.24
  Group = -> [Te_element002]
  conduct = 2
  density = 1
  expand = 3
  formula = Te
  name = G4_Te
  specific = 4
FEATURE [App::DocumentObjectGroupPython] I_element010  label="I_element : 006"  # scripted group (container) (typed FeaturePython)
  n = 1
  ref = I_element
FEATURE [App::DocumentObjectGroupPython] G4_I  # scripted group (container) (typed FeaturePython)
  Dunit = g/cm3
  Dvalue = 4.93
  Group = -> [I_element010]
  conduct = 2
  density = 1
  expand = 3
  formula = I
  name = G4_I
  specific = 4
FEATURE [App::DocumentObjectGroupPython] Xe_element001  label="Xe_element : 1"  # scripted group (container) (typed FeaturePython)
  n = 1
  ref = Xe_element
FEATURE [App::DocumentObjectGroupPython] G4_Xe  # scripted group (container) (typed FeaturePython)
  Dunit = g/cm3
  Dvalue = 0.00548536
  Group = -> [Xe_element001]
  conduct = 2
  density = 1
  expand = 3
  formula = Xe
  name = G4_Xe
  specific = 4
FEATURE [App::DocumentObjectGroupPython] Cs_element003  label="Cs_element : 003"  # scripted group (container) (typed FeaturePython)
  n = 1
  ref = Cs_element
FEATURE [App::DocumentObjectGroupPython] G4_Cs  # scripted group (container) (typed FeaturePython)
  Dunit = g/cm3
  Dvalue = 1.873
  Group = -> [Cs_element003]
  conduct = 2
  density = 1
  expand = 3
  formula = Cs
  name = G4_Cs
  specific = 4
FEATURE [App::DocumentObjectGroupPython] Ba_element003  label="Ba_element : 003"  # scripted group (container) (typed FeaturePython)
  n = 1
  ref = Ba_element
FEATURE [App::DocumentObjectGroupPython] G4_Ba  # scripted group (container) (typed FeaturePython)
  Dunit = g/cm3
  Dvalue = 3.5
  Group = -> [Ba_element003]
  conduct = 2
  density = 1
  expand = 3
  formula = Ba
  name = G4_Ba
  specific = 4
FEATURE [App::DocumentObjectGroupPython] La_element003  label="La_element : 003"  # scripted group (container) (typed FeaturePython)
  n = 1
  ref = La_element
FEATURE [App::DocumentObjectGroupPython] G4_La  # scripted group (container) (typed FeaturePython)
  Dunit = g/cm3
  Dvalue = 6.154
  Group = -> [La_element003]
  conduct = 2
  density = 1
  expand = 3
  formula = La
  name = G4_La
  specific = 4
FEATURE [App::DocumentObjectGroupPython] Ce_element002  label="Ce_element : 1"  # scripted group (container) (typed FeaturePython)
  n = 1
  ref = Ce_element
FEATURE [App::DocumentObjectGroupPython] G4_Ce  # scripted group (container) (typed FeaturePython)
  Dunit = g/cm3
  Dvalue = 6.657
  Group = -> [Ce_element002]
  conduct = 2
  density = 1
  expand = 3
  formula = Ce
  name = G4_Ce
  specific = 4
FEATURE [App::DocumentObjectGroupPython] Pr_element001  label="Pr_element : 1"  # scripted group (container) (typed FeaturePython)
  n = 1
  ref = Pr_element
FEATURE [App::DocumentObjectGroupPython] G4_Pr  # scripted group (container) (typed FeaturePython)
  Dunit = g/cm3
  Dvalue = 6.71
  Group = -> [Pr_element001]
  conduct = 2
  density = 1
  expand = 3
  formula = Pr
  name = G4_Pr
  specific = 4
FEATURE [App::DocumentObjectGroupPython] Nd_element001  label="Nd_element : 1"  # scripted group (container) (typed FeaturePython)
  n = 1
  ref = Nd_element
FEATURE [App::DocumentObjectGroupPython] G4_Nd  # scripted group (container) (typed FeaturePython)
  Dunit = g/cm3
  Dvalue = 6.9
  Group = -> [Nd_element001]
  conduct = 2
  density = 1
  expand = 3
  formula = Nd
  name = G4_Nd
  specific = 4
FEATURE [App::DocumentObjectGroupPython] Pm_element001  label="Pm_element : 1"  # scripted group (container) (typed FeaturePython)
  n = 1
  ref = Pm_element
FEATURE [App::DocumentObjectGroupPython] G4_Pm  # scripted group (container) (typed FeaturePython)
  Dunit = g/cm3
  Dvalue = 7.22
  Group = -> [Pm_element001]
  conduct = 2
  density = 1
  expand = 3
  formula = Pm
  name = G4_Pm
  specific = 4
FEATURE [App::DocumentObjectGroupPython] Sm_element001  label="Sm_element : 1"  # scripted group (container) (typed FeaturePython)
  n = 1
  ref = Sm_element
FEATURE [App::DocumentObjectGroupPython] G4_Sm  # scripted group (container) (typed FeaturePython)
  Dunit = g/cm3
  Dvalue = 7.46
  Group = -> [Sm_element001]
  conduct = 2
  density = 1
  expand = 3
  formula = Sm
  name = G4_Sm
  specific = 4
FEATURE [App::DocumentObjectGroupPython] Eu_element001  label="Eu_element : 1"  # scripted group (container) (typed FeaturePython)
  n = 1
  ref = Eu_element
FEATURE [App::DocumentObjectGroupPython] G4_Eu  # scripted group (container) (typed FeaturePython)
  Dunit = g/cm3
  Dvalue = 5.243
  Group = -> [Eu_element001]
  conduct = 2
  density = 1
  expand = 3
  formula = Eu
  name = G4_Eu
  specific = 4
FEATURE [App::DocumentObjectGroupPython] Gd_element002  label="Gd_element : 1"  # scripted group (container) (typed FeaturePython)
  n = 1
  ref = Gd_element
FEATURE [App::DocumentObjectGroupPython] G4_Gd  # scripted group (container) (typed FeaturePython)
  Dunit = g/cm3
  Dvalue = 7.9004
  Group = -> [Gd_element002]
  conduct = 2
  density = 1
  expand = 3
  formula = Gd
  name = G4_Gd
  specific = 4
FEATURE [App::DocumentObjectGroupPython] Tb_element001  label="Tb_element : 1"  # scripted group (container) (typed FeaturePython)
  n = 1
  ref = Tb_element
FEATURE [App::DocumentObjectGroupPython] G4_Tb  # scripted group (container) (typed FeaturePython)
  Dunit = g/cm3
  Dvalue = 8.229
  Group = -> [Tb_element001]
  conduct = 2
  density = 1
  expand = 3
  formula = Tb
  name = G4_Tb
  specific = 4
FEATURE [App::DocumentObjectGroupPython] Dy_element001  label="Dy_element : 1"  # scripted group (container) (typed FeaturePython)
  n = 1
  ref = Dy_element
FEATURE [App::DocumentObjectGroupPython] G4_Dy  # scripted group (container) (typed FeaturePython)
  Dunit = g/cm3
  Dvalue = 8.55
  Group = -> [Dy_element001]
  conduct = 2
  density = 1
  expand = 3
  formula = Dy
  name = G4_Dy
  specific = 4
FEATURE [App::DocumentObjectGroupPython] Ho_element001  label="Ho_element : 1"  # scripted group (container) (typed FeaturePython)
  n = 1
  ref = Ho_element
FEATURE [App::DocumentObjectGroupPython] G4_Ho  # scripted group (container) (typed FeaturePython)
  Dunit = g/cm3
  Dvalue = 8.795
  Group = -> [Ho_element001]
  conduct = 2
  density = 1
  expand = 3
  formula = Ho
  name = G4_Ho
  specific = 4
FEATURE [App::DocumentObjectGroupPython] Er_element001  label="Er_element : 1"  # scripted group (container) (typed FeaturePython)
  n = 1
  ref = Er_element
FEATURE [App::DocumentObjectGroupPython] G4_Er  # scripted group (container) (typed FeaturePython)
  Dunit = g/cm3
  Dvalue = 9.066
  Group = -> [Er_element001]
  conduct = 2
  density = 1
  expand = 3
  formula = Er
  name = G4_Er
  specific = 4
FEATURE [App::DocumentObjectGroupPython] Tm_element001  label="Tm_element : 1"  # scripted group (container) (typed FeaturePython)
  n = 1
  ref = Tm_element
FEATURE [App::DocumentObjectGroupPython] G4_Tm  # scripted group (container) (typed FeaturePython)
  Dunit = g/cm3
  Dvalue = 9.321
  Group = -> [Tm_element001]
  conduct = 2
  density = 1
  expand = 3
  formula = Tm
  name = G4_Tm
  specific = 4
FEATURE [App::DocumentObjectGroupPython] Yb_element001  label="Yb_element : 1"  # scripted group (container) (typed FeaturePython)
  n = 1
  ref = Yb_element
FEATURE [App::DocumentObjectGroupPython] G4_Yb  # scripted group (container) (typed FeaturePython)
  Dunit = g/cm3
  Dvalue = 6.73
  Group = -> [Yb_element001]
  conduct = 2
  density = 1
  expand = 3
  formula = Yb
  name = G4_Yb
  specific = 4
FEATURE [App::DocumentObjectGroupPython] Lu_element001  label="Lu_element : 1"  # scripted group (container) (typed FeaturePython)
  n = 1
  ref = Lu_element
FEATURE [App::DocumentObjectGroupPython] G4_Lu  # scripted group (container) (typed FeaturePython)
  Dunit = g/cm3
  Dvalue = 9.84
  Group = -> [Lu_element001]
  conduct = 2
  density = 1
  expand = 3
  formula = Lu
  name = G4_Lu
  specific = 4
FEATURE [App::DocumentObjectGroupPython] Hf_element001  label="Hf_element : 1"  # scripted group (container) (typed FeaturePython)
  n = 1
  ref = Hf_element
FEATURE [App::DocumentObjectGroupPython] G4_Hf  # scripted group (container) (typed FeaturePython)
  Dunit = g/cm3
  Dvalue = 13.31
  Group = -> [Hf_element001]
  conduct = 2
  density = 1
  expand = 3
  formula = Hf
  name = G4_Hf
  specific = 4
FEATURE [App::DocumentObjectGroupPython] Ta_element001  label="Ta_element : 1"  # scripted group (container) (typed FeaturePython)
  n = 1
  ref = Ta_element
FEATURE [App::DocumentObjectGroupPython] G4_Ta  # scripted group (container) (typed FeaturePython)
  Dunit = g/cm3
  Dvalue = 16.654
  Group = -> [Ta_element001]
  conduct = 2
  density = 1
  expand = 3
  formula = Ta
  name = G4_Ta
  specific = 4
FEATURE [App::DocumentObjectGroupPython] W_element004  label="W_element : 004"  # scripted group (container) (typed FeaturePython)
  n = 1
  ref = W_element
FEATURE [App::DocumentObjectGroupPython] G4_W  # scripted group (container) (typed FeaturePython)
  Dunit = g/cm3
  Dvalue = 19.3
  Group = -> [W_element004]
  conduct = 2
  density = 1
  expand = 3
  formula = W
  name = G4_W
  specific = 4
FEATURE [App::DocumentObjectGroupPython] Re_element001  label="Re_element : 1"  # scripted group (container) (typed FeaturePython)
  n = 1
  ref = Re_element
FEATURE [App::DocumentObjectGroupPython] G4_Re  # scripted group (container) (typed FeaturePython)
  Dunit = g/cm3
  Dvalue = 21.02
  Group = -> [Re_element001]
  conduct = 2
  density = 1
  expand = 3
  formula = Re
  name = G4_Re
  specific = 4
FEATURE [App::DocumentObjectGroupPython] Os_element001  label="Os_element : 1"  # scripted group (container) (typed FeaturePython)
  n = 1
  ref = Os_element
FEATURE [App::DocumentObjectGroupPython] G4_Os  # scripted group (container) (typed FeaturePython)
  Dunit = g/cm3
  Dvalue = 22.57
  Group = -> [Os_element001]
  conduct = 2
  density = 1
  expand = 3
  formula = Os
  name = G4_Os
  specific = 4
FEATURE [App::DocumentObjectGroupPython] Ir_element001  label="Ir_element : 1"  # scripted group (container) (typed FeaturePython)
  n = 1
  ref = Ir_element
FEATURE [App::DocumentObjectGroupPython] G4_Ir  # scripted group (container) (typed FeaturePython)
  Dunit = g/cm3
  Dvalue = 22.42
  Group = -> [Ir_element001]
  conduct = 2
  density = 1
  expand = 3
  formula = Ir
  name = G4_Ir
  specific = 4
FEATURE [App::DocumentObjectGroupPython] Pt_element001  label="Pt_element : 1"  # scripted group (container) (typed FeaturePython)
  n = 1
  ref = Pt_element
FEATURE [App::DocumentObjectGroupPython] G4_Pt  # scripted group (container) (typed FeaturePython)
  Dunit = g/cm3
  Dvalue = 21.45
  Group = -> [Pt_element001]
  conduct = 2
  density = 1
  expand = 3
  formula = Pt
  name = G4_Pt
  specific = 4
FEATURE [App::DocumentObjectGroupPython] Au_element001  label="Au_element : 1"  # scripted group (container) (typed FeaturePython)
  n = 1
  ref = Au_element
FEATURE [App::DocumentObjectGroupPython] G4_Au  # scripted group (container) (typed FeaturePython)
  Dunit = g/cm3
  Dvalue = 19.32
  Group = -> [Au_element001]
  conduct = 2
  density = 1
  expand = 3
  formula = Au
  name = G4_Au
  specific = 4
FEATURE [App::DocumentObjectGroupPython] Hg_element002  label="Hg_element : 002"  # scripted group (container) (typed FeaturePython)
  n = 1
  ref = Hg_element
FEATURE [App::DocumentObjectGroupPython] G4_Hg  # scripted group (container) (typed FeaturePython)
  Dunit = g/cm3
  Dvalue = 13.546
  Group = -> [Hg_element002]
  conduct = 2
  density = 1
  expand = 3
  formula = Hg
  name = G4_Hg
  specific = 4
FEATURE [App::DocumentObjectGroupPython] Tl_element002  label="Tl_element : 002"  # scripted group (container) (typed FeaturePython)
  n = 1
  ref = Tl_element
FEATURE [App::DocumentObjectGroupPython] G4_Tl  # scripted group (container) (typed FeaturePython)
  Dunit = g/cm3
  Dvalue = 11.72
  Group = -> [Tl_element002]
  conduct = 2
  density = 1
  expand = 3
  formula = Tl
  name = G4_Tl
  specific = 4
FEATURE [App::DocumentObjectGroupPython] Pb_element003  label="Pb_element : 1"  # scripted group (container) (typed FeaturePython)
  n = 1
  ref = Pb_element
FEATURE [App::DocumentObjectGroupPython] G4_Pb  # scripted group (container) (typed FeaturePython)
  Dunit = g/cm3
  Dvalue = 11.35
  Group = -> [Pb_element003]
  conduct = 2
  density = 1
  expand = 3
  formula = Pb
  name = G4_Pb
  specific = 4
FEATURE [App::DocumentObjectGroupPython] Bi_element002  label="Bi_element : 1"  # scripted group (container) (typed FeaturePython)
  n = 1
  ref = Bi_element
FEATURE [App::DocumentObjectGroupPython] G4_Bi  # scripted group (container) (typed FeaturePython)
  Dunit = g/cm3
  Dvalue = 9.747
  Group = -> [Bi_element002]
  conduct = 2
  density = 1
  expand = 3
  formula = Bi
  name = G4_Bi
  specific = 4
FEATURE [App::DocumentObjectGroupPython] Po_element001  label="Po_element : 1"  # scripted group (container) (typed FeaturePython)
  n = 1
  ref = Po_element
FEATURE [App::DocumentObjectGroupPython] G4_Po  # scripted group (container) (typed FeaturePython)
  Dunit = g/cm3
  Dvalue = 9.32
  Group = -> [Po_element001]
  conduct = 2
  density = 1
  expand = 3
  formula = Po
  name = G4_Po
  specific = 4
FEATURE [App::DocumentObjectGroupPython] At_element001  label="At_element : 1"  # scripted group (container) (typed FeaturePython)
  n = 1
  ref = At_element
FEATURE [App::DocumentObjectGroupPython] G4_At  # scripted group (container) (typed FeaturePython)
  Dunit = g/cm3
  Dvalue = 9.32
  Group = -> [At_element001]
  conduct = 2
  density = 1
  expand = 3
  formula = At
  name = G4_At
  specific = 4
FEATURE [App::DocumentObjectGroupPython] Rn_element001  label="Rn_element : 1"  # scripted group (container) (typed FeaturePython)
  n = 1
  ref = Rn_element
FEATURE [App::DocumentObjectGroupPython] G4_Rn  # scripted group (container) (typed FeaturePython)
  Dunit = g/cm3
  Dvalue = 0.00900662
  Group = -> [Rn_element001]
  conduct = 2
  density = 1
  expand = 3
  formula = Rn
  name = G4_Rn
  specific = 4
FEATURE [App::DocumentObjectGroupPython] Fr_element001  label="Fr_element : 1"  # scripted group (container) (typed FeaturePython)
  n = 1
  ref = Fr_element
FEATURE [App::DocumentObjectGroupPython] G4_Fr  # scripted group (container) (typed FeaturePython)
  Dunit = g/cm3
  Dvalue = 1
  Group = -> [Fr_element001]
  conduct = 2
  density = 1
  expand = 3
  formula = Fr
  name = G4_Fr
  specific = 4
FEATURE [App::DocumentObjectGroupPython] Ra_element001  label="Ra_element : 1"  # scripted group (container) (typed FeaturePython)
  n = 1
  ref = Ra_element
FEATURE [App::DocumentObjectGroupPython] G4_Ra  # scripted group (container) (typed FeaturePython)
  Dunit = g/cm3
  Dvalue = 5
  Group = -> [Ra_element001]
  conduct = 2
  density = 1
  expand = 3
  formula = Ra
  name = G4_Ra
  specific = 4
FEATURE [App::DocumentObjectGroupPython] Ac_element001  label="Ac_element : 1"  # scripted group (container) (typed FeaturePython)
  n = 1
  ref = Ac_element
FEATURE [App::DocumentObjectGroupPython] G4_Ac  # scripted group (container) (typed FeaturePython)
  Dunit = g/cm3
  Dvalue = 10.07
  Group = -> [Ac_element001]
  conduct = 2
  density = 1
  expand = 3
  formula = Ac
  name = G4_Ac
  specific = 4
FEATURE [App::DocumentObjectGroupPython] Th_element001  label="Th_element : 1"  # scripted group (container) (typed FeaturePython)
  n = 1
  ref = Th_element
FEATURE [App::DocumentObjectGroupPython] G4_Th  # scripted group (container) (typed FeaturePython)
  Dunit = g/cm3
  Dvalue = 11.72
  Group = -> [Th_element001]
  conduct = 2
  density = 1
  expand = 3
  formula = Th
  name = G4_Th
  specific = 4
FEATURE [App::DocumentObjectGroupPython] Pa_element001  label="Pa_element : 1"  # scripted group (container) (typed FeaturePython)
  n = 1
  ref = Pa_element
FEATURE [App::DocumentObjectGroupPython] G4_Pa  # scripted group (container) (typed FeaturePython)
  Dunit = g/cm3
  Dvalue = 15.37
  Group = -> [Pa_element001]
  conduct = 2
  density = 1
  expand = 3
  formula = Pa
  name = G4_Pa
  specific = 4
FEATURE [App::DocumentObjectGroupPython] U_element004  label="U_element : 004"  # scripted group (container) (typed FeaturePython)
  n = 1
  ref = U_element
FEATURE [App::DocumentObjectGroupPython] G4_U  # scripted group (container) (typed FeaturePython)
  Dunit = g/cm3
  Dvalue = 18.95
  Group = -> [U_element004]
  conduct = 2
  density = 1
  expand = 3
  formula = U
  name = G4_U
  specific = 4
FEATURE [App::DocumentObjectGroupPython] Np_element001  label="Np_element : 1"  # scripted group (container) (typed FeaturePython)
  n = 1
  ref = Np_element
FEATURE [App::DocumentObjectGroupPython] G4_Np  # scripted group (container) (typed FeaturePython)
  Dunit = g/cm3
  Dvalue = 20.25
  Group = -> [Np_element001]
  conduct = 2
  density = 1
  expand = 3
  formula = Np
  name = G4_Np
  specific = 4
FEATURE [App::DocumentObjectGroupPython] Pu_element002  label="Pu_element : 002"  # scripted group (container) (typed FeaturePython)
  n = 1
  ref = Pu_element
FEATURE [App::DocumentObjectGroupPython] G4_Pu  # scripted group (container) (typed FeaturePython)
  Dunit = g/cm3
  Dvalue = 19.84
  Group = -> [Pu_element002]
  conduct = 2
  density = 1
  expand = 3
  formula = Pu
  name = G4_Pu
  specific = 4
FEATURE [App::DocumentObjectGroupPython] Am_element001  label="Am_element : 1"  # scripted group (container) (typed FeaturePython)
  n = 1
  ref = Am_element
FEATURE [App::DocumentObjectGroupPython] G4_Am  # scripted group (container) (typed FeaturePython)
  Dunit = g/cm3
  Dvalue = 13.67
  Group = -> [Am_element001]
  conduct = 2
  density = 1
  expand = 3
  formula = Am
  name = G4_Am
  specific = 4
FEATURE [App::DocumentObjectGroupPython] Cm_element001  label="Cm_element : 1"  # scripted group (container) (typed FeaturePython)
  n = 1
  ref = Cm_element
FEATURE [App::DocumentObjectGroupPython] G4_Cm  # scripted group (container) (typed FeaturePython)
  Dunit = g/cm3
  Dvalue = 13.51
  Group = -> [Cm_element001]
  conduct = 2
  density = 1
  expand = 3
  formula = Cm
  name = G4_Cm
  specific = 4
FEATURE [App::DocumentObjectGroupPython] Bk_element001  label="Bk_element : 1"  # scripted group (container) (typed FeaturePython)
  n = 1
  ref = Bk_element
FEATURE [App::DocumentObjectGroupPython] G4_Bk  # scripted group (container) (typed FeaturePython)
  Dunit = g/cm3
  Dvalue = 14
  Group = -> [Bk_element001]
  conduct = 2
  density = 1
  expand = 3
  formula = Bk
  name = G4_Bk
  specific = 4
FEATURE [App::DocumentObjectGroupPython] Cf_element001  label="Cf_element : 1"  # scripted group (container) (typed FeaturePython)
  n = 1
  ref = Cf_element
FEATURE [App::DocumentObjectGroupPython] G4_Cf  # scripted group (container) (typed FeaturePython)
  Dunit = g/cm3
  Dvalue = 10
  Group = -> [Cf_element001]
  conduct = 2
  density = 1
  expand = 3
  formula = Cf
  name = G4_Cf
  specific = 4
FEATURE [App::DocumentObjectGroupPython] Element  # scripted group (container) (typed FeaturePython)
  Group = -> [G4_H,G4_He,G4_Li,G4_Be,G4_B,G4_C,G4_N,G4_O,G4_F,G4_Ne,G4_Na,G4_Mg,G4_Al,G4_Si,G4_P,G4_S,G4_Cl,G4_Ar,G4_K,G4_Ca,G4_Sc,G4_Ti,G4_V,G4_Cr,G4_Mn,G4_Fe,G4_Co,G4_Ni,G4_Cu,G4_Zn,G4_Ga,G4_Ge,G4_As,G4_Se,G4_Br,G4_Kr,G4_Rb,G4_Sr,G4_Y,G4_Zr,G4_Nb,G4_Mo,G4_Tc,G4_Ru,G4_Rh,G4_Pd,G4_Ag,G4_Cd,G4_In,G4_Sn,G4_Sb,G4_Te,G4_I,G4_Xe,G4_Cs,G4_Ba,G4_La,G4_Ce,G4_Pr,G4_Nd,G4_Pm,G4_Sm,G4_Eu,G4_Gd,G4_Tb,G4_Dy,G4_Ho,G4_Er,+30 more]
FEATURE [App::DocumentObjectGroupPython] H_element114  label="H_element : 063"  # scripted group (container) (typed FeaturePython)
  n = 2
  ref = H_element
FEATURE [App::DocumentObjectGroupPython] G4_lH2  # scripted group (container) (typed FeaturePython)
  Dunit = g/cm3
  Dvalue = 0.0708
  Group = -> [H_element114]
  conduct = 2
  density = 1
  expand = 3
  formula = G4_lH2
  name = G4_lH2
  specific = 4
FEATURE [App::DocumentObjectGroupPython] N_element049  label="N_element : 022"  # scripted group (container) (typed FeaturePython)
  n = 2
  ref = N_element
FEATURE [App::DocumentObjectGroupPython] G4_lN2  # scripted group (container) (typed FeaturePython)
  Dunit = g/cm3
  Dvalue = 0.807
  Group = -> [N_element049]
  conduct = 2
  density = 1
  expand = 3
  formula = G4_lN2
  name = G4_lN2
  specific = 4
FEATURE [App::DocumentObjectGroupPython] O_element106  label="O_element : 060"  # scripted group (container) (typed FeaturePython)
  n = 2
  ref = O_element
FEATURE [App::DocumentObjectGroupPython] G4_lO2  # scripted group (container) (typed FeaturePython)
  Dunit = g/cm3
  Dvalue = 1.141
  Group = -> [O_element106]
  conduct = 2
  density = 1
  expand = 3
  formula = G4_lO2
  name = G4_lO2
  specific = 4
FEATURE [App::DocumentObjectGroupPython] Ar  label="Ar : 1"  # scripted group (container) (typed FeaturePython)
  n = 1
  ref = Ar
FEATURE [App::DocumentObjectGroupPython] G4_lAr  # scripted group (container) (typed FeaturePython)
  Dunit = g/cm3
  Dvalue = 1.396
  Group = -> [Ar]
  conduct = 2
  density = 1
  expand = 3
  formula = G4_lAr
  name = G4_lAr
  specific = 4
FEATURE [App::DocumentObjectGroupPython] Br  label="Br : 1"  # scripted group (container) (typed FeaturePython)
  n = 1
  ref = Br
FEATURE [App::DocumentObjectGroupPython] G4_lBr  # scripted group (container) (typed FeaturePython)
  Dunit = g/cm3
  Dvalue = 3.1028
  Group = -> [Br]
  conduct = 2
  density = 1
  expand = 3
  formula = G4_lBr
  name = G4_lBr
  specific = 4
FEATURE [App::DocumentObjectGroupPython] Kr  label="Kr : 1"  # scripted group (container) (typed FeaturePython)
  n = 1
  ref = Kr
FEATURE [App::DocumentObjectGroupPython] G4_lKr  # scripted group (container) (typed FeaturePython)
  Dunit = g/cm3
  Dvalue = 2.418
  Group = -> [Kr]
  conduct = 2
  density = 1
  expand = 3
  formula = G4_lKr
  name = G4_lKr
  specific = 4
FEATURE [App::DocumentObjectGroupPython] Xe  label="Xe : 1"  # scripted group (container) (typed FeaturePython)
  n = 1
  ref = Xe
FEATURE [App::DocumentObjectGroupPython] G4_lXe  # scripted group (container) (typed FeaturePython)
  Dunit = g/cm3
  Dvalue = 2.953
  Group = -> [Xe]
  conduct = 2
  density = 1
  expand = 3
  formula = G4_lXe
  name = G4_lXe
  specific = 4
FEATURE [App::DocumentObjectGroupPython] O_element107  label="O_element : 061"  # scripted group (container) (typed FeaturePython)
  n = 4
  ref = O_element
FEATURE [App::DocumentObjectGroupPython] Pb_element004  label="Pb_element : 002"  # scripted group (container) (typed FeaturePython)
  n = 1
  ref = Pb_element
FEATURE [App::DocumentObjectGroupPython] W_element005  label="W_element : 005"  # scripted group (container) (typed FeaturePython)
  n = 1
  ref = W_element
FEATURE [App::DocumentObjectGroupPython] G4_PbWO4  # scripted group (container) (typed FeaturePython)
  Dunit = g/cm3
  Dvalue = 8.28
  Group = -> [O_element107,Pb_element004,W_element005]
  conduct = 2
  density = 1
  expand = 3
  formula = G4_PbWO4
  name = G4_PbWO4
  specific = 4
FEATURE [App::DocumentObjectGroupPython] alactic  label="alactic : 1"  # scripted group (container) (typed FeaturePython)
  n = 1
  ref = alactic
FEATURE [App::DocumentObjectGroupPython] G4_Galactic  # scripted group (container) (typed FeaturePython)
  Dunit = g/cm3
  Dvalue = 0
  Group = -> [alactic]
  conduct = 2
  density = 1
  expand = 3
  formula = G4_Galactic
  name = G4_Galactic
  specific = 4
FEATURE [App::DocumentObjectGroupPython] RAPHITE_POROUS  label="RAPHITE_POROUS : 1"  # scripted group (container) (typed FeaturePython)
  n = 1
  ref = RAPHITE_POROUS
FEATURE [App::DocumentObjectGroupPython] G4_GRAPHITE_POROUS  # scripted group (container) (typed FeaturePython)
  Dunit = g/cm3
  Dvalue = 1.7
  Group = -> [RAPHITE_POROUS]
  conduct = 2
  density = 1
  expand = 3
  formula = G4_GRAPHITE_POROUS
  name = G4_GRAPHITE_POROUS
  specific = 4
FEATURE [App::DocumentObjectGroupPython] H_element115  label="H_element : 0.150"  # scripted group (container) (typed FeaturePython)
  n = 0.080538
FEATURE [App::DocumentObjectGroupPython] C_element125  label="C_element : 0.600"  # scripted group (container) (typed FeaturePython)
  n = 0.599848
FEATURE [App::DocumentObjectGroupPython] O_element108  label="O_element : 0.320"  # scripted group (container) (typed FeaturePython)
  n = 0.319614
FEATURE [App::DocumentObjectGroupPython] G4_LUCITE  # scripted group (container) (typed FeaturePython)
  Dunit = g/cm3
  Dvalue = 1.19
  Group = -> [H_element115,C_element125,O_element108]
  conduct = 2
  density = 1
  expand = 3
  formula = G4_LUCITE
  name = G4_LUCITE
  specific = 4
FEATURE [App::DocumentObjectGroupPython] Cu_element002  label="Cu_element : 62"  # scripted group (container) (typed FeaturePython)
  n = 62
  ref = Cu_element
FEATURE [App::DocumentObjectGroupPython] Zn_element002  label="Zn_element : 35"  # scripted group (container) (typed FeaturePython)
  n = 35
  ref = Zn_element
FEATURE [App::DocumentObjectGroupPython] Pb_element005  label="Pb_element : 3"  # scripted group (container) (typed FeaturePython)
  n = 3
  ref = Pb_element
FEATURE [App::DocumentObjectGroupPython] G4_BRASS  # scripted group (container) (typed FeaturePython)
  Dunit = g/cm3
  Dvalue = 8.52
  Group = -> [Cu_element002,Zn_element002,Pb_element005]
  conduct = 2
  density = 1
  expand = 3
  formula = G4_BRASS
  name = G4_BRASS
  specific = 4
FEATURE [App::DocumentObjectGroupPython] Cu_element003  label="Cu_element : 89"  # scripted group (container) (typed FeaturePython)
  n = 89
  ref = Cu_element
FEATURE [App::DocumentObjectGroupPython] Zn_element003  label="Zn_element : 9"  # scripted group (container) (typed FeaturePython)
  n = 9
  ref = Zn_element
FEATURE [App::DocumentObjectGroupPython] Pb_element006  label="Pb_element : 2"  # scripted group (container) (typed FeaturePython)
  n = 2
  ref = Pb_element
FEATURE [App::DocumentObjectGroupPython] G4_BRONZE  # scripted group (container) (typed FeaturePython)
  Dunit = g/cm3
  Dvalue = 8.82
  Group = -> [Cu_element003,Zn_element003,Pb_element006]
  conduct = 2
  density = 1
  expand = 3
  formula = G4_BRONZE
  name = G4_BRONZE
  specific = 4
FEATURE [App::DocumentObjectGroupPython] Fe_element008  label="Fe_element : 74"  # scripted group (container) (typed FeaturePython)
  n = 74
  ref = Fe_element
FEATURE [App::DocumentObjectGroupPython] Cr_element002  label="Cr_element : 18"  # scripted group (container) (typed FeaturePython)
  n = 18
  ref = Cr_element
FEATURE [App::DocumentObjectGroupPython] Ni_element002  label="Ni_element : 8"  # scripted group (container) (typed FeaturePython)
  n = 8
  ref = Ni_element
FEATURE [App::DocumentObjectGroupPython] G4_STAINLESS_STEEL  label="G4_STAINLESS-STEEL"  # scripted group (container) (typed FeaturePython)
  Dunit = g/cm3
  Dvalue = 8
  Group = -> [Fe_element008,Cr_element002,Ni_element002]
  conduct = 2
  density = 1
  expand = 3
  formula = G4_STAINLESS-STEEL
  name = G4_STAINLESS-STEEL
  specific = 4
FEATURE [App::DocumentObjectGroupPython] H_element116  label="H_element : 064"  # scripted group (container) (typed FeaturePython)
  n = 18
  ref = H_element
FEATURE [App::DocumentObjectGroupPython] C_element126  label="C_element : 071"  # scripted group (container) (typed FeaturePython)
  n = 12
  ref = C_element
FEATURE [App::DocumentObjectGroupPython] O_element109  label="O_element : 062"  # scripted group (container) (typed FeaturePython)
  n = 7
  ref = O_element
FEATURE [App::DocumentObjectGroupPython] G4_CR39  # scripted group (container) (typed FeaturePython)
  Dunit = g/cm3
  Dvalue = 1.32
  Group = -> [H_element116,C_element126,O_element109]
  conduct = 2
  density = 1
  expand = 3
  formula = G4_CR39
  name = G4_CR39
  specific = 4
FEATURE [App::DocumentObjectGroupPython] H_element117  label="H_element : 38"  # scripted group (container) (typed FeaturePython)
  n = 38
  ref = H_element
FEATURE [App::DocumentObjectGroupPython] C_element127  label="C_element : 072"  # scripted group (container) (typed FeaturePython)
  n = 18
  ref = C_element
FEATURE [App::DocumentObjectGroupPython] O_element110  label="O_element : 063"  # scripted group (container) (typed FeaturePython)
  n = 1
  ref = O_element
FEATURE [App::DocumentObjectGroupPython] G4_OCTADECANOL  # scripted group (container) (typed FeaturePython)
  Dunit = g/cm3
  Dvalue = 0.812
  Group = -> [H_element117,C_element127,O_element110]
  conduct = 2
  density = 1
  expand = 3
  formula = G4_OCTADECANOL
  name = G4_OCTADECANOL
  specific = 4
FEATURE [App::DocumentObjectGroupPython] HEP  # scripted group (container) (typed FeaturePython)
  Group = -> [G4_lH2,G4_lN2,G4_lO2,G4_lAr,G4_lBr,G4_lKr,G4_lXe,G4_PbWO4,G4_Galactic,G4_GRAPHITE_POROUS,G4_LUCITE,G4_BRASS,G4_BRONZE,G4_STAINLESS_STEEL,G4_CR39,G4_OCTADECANOL]
FEATURE [App::DocumentObjectGroupPython] C_element128  label="C_element : 073"  # scripted group (container) (typed FeaturePython)
  n = 14
  ref = C_element
FEATURE [App::DocumentObjectGroupPython] H_element118  label="H_element : 065"  # scripted group (container) (typed FeaturePython)
  n = 10
  ref = H_element
FEATURE [App::DocumentObjectGroupPython] O_element111  label="O_element : 064"  # scripted group (container) (typed FeaturePython)
  n = 2
  ref = O_element
FEATURE [App::DocumentObjectGroupPython] N_element050  label="N_element : 023"  # scripted group (container) (typed FeaturePython)
  n = 2
  ref = N_element
FEATURE [App::DocumentObjectGroupPython] G4_KEVLAR  # scripted group (container) (typed FeaturePython)
  Dunit = g/cm3
  Dvalue = 1.44
  Group = -> [C_element128,H_element118,O_element111,N_element050]
  conduct = 2
  density = 1
  expand = 3
  formula = G4_KEVLAR
  name = G4_KEVLAR
  specific = 4
FEATURE [App::DocumentObjectGroupPython] C_element129  label="C_element : 074"  # scripted group (container) (typed FeaturePython)
  n = 10
  ref = C_element
FEATURE [App::DocumentObjectGroupPython] H_element119  label="H_element : 066"  # scripted group (container) (typed FeaturePython)
  n = 8
  ref = H_element
FEATURE [App::DocumentObjectGroupPython] O_element112  label="O_element : 065"  # scripted group (container) (typed FeaturePython)
  n = 4
  ref = O_element
FEATURE [App::DocumentObjectGroupPython] G4_DACRON  # scripted group (container) (typed FeaturePython)
  Dunit = g/cm3
  Dvalue = 1.4
  Group = -> [C_element129,H_element119,O_element112]
  conduct = 2
  density = 1
  expand = 3
  formula = G4_DACRON
  name = G4_DACRON
  specific = 4
FEATURE [App::DocumentObjectGroupPython] C_element130  label="C_element : 075"  # scripted group (container) (typed FeaturePython)
  n = 4
  ref = C_element
FEATURE [App::DocumentObjectGroupPython] H_element120  label="H_element : 067"  # scripted group (container) (typed FeaturePython)
  n = 5
  ref = H_element
FEATURE [App::DocumentObjectGroupPython] Cl_element030  label="Cl_element : 016"  # scripted group (container) (typed FeaturePython)
  n = 1
  ref = Cl_element
FEATURE [App::DocumentObjectGroupPython] G4_NEOPRENE  # scripted group (container) (typed FeaturePython)
  Dunit = g/cm3
  Dvalue = 1.23
  Group = -> [C_element130,H_element120,Cl_element030]
  conduct = 2
  density = 1
  expand = 3
  formula = G4_NEOPRENE
  name = G4_NEOPRENE
  specific = 4
FEATURE [App::DocumentObjectGroupPython] Space  # scripted group (container) (typed FeaturePython)
  Group = -> [G4_KEVLAR,G4_DACRON,G4_NEOPRENE]
FEATURE [App::DocumentObjectGroupPython] H_element121  label="H_element : 068"  # scripted group (container) (typed FeaturePython)
  n = 5
  ref = H_element
FEATURE [App::DocumentObjectGroupPython] C_element131  label="C_element : 076"  # scripted group (container) (typed FeaturePython)
  n = 4
  ref = C_element
FEATURE [App::DocumentObjectGroupPython] N_element051  label="N_element : 3"  # scripted group (container) (typed FeaturePython)
  n = 3
  ref = N_element
FEATURE [App::DocumentObjectGroupPython] O_element113  label="O_element : 066"  # scripted group (container) (typed FeaturePython)
  n = 1
  ref = O_element
FEATURE [App::DocumentObjectGroupPython] G4_CYTOSINE  # scripted group (container) (typed FeaturePython)
  Dunit = g/cm3
  Dvalue = 1.55
  Group = -> [H_element121,C_element131,N_element051,O_element113]
  conduct = 2
  density = 1
  expand = 3
  formula = G4_CYTOSINE
  name = G4_CYTOSINE
  specific = 4
FEATURE [App::DocumentObjectGroupPython] H_element122  label="H_element : 069"  # scripted group (container) (typed FeaturePython)
  n = 6
  ref = H_element
FEATURE [App::DocumentObjectGroupPython] C_element132  label="C_element : 077"  # scripted group (container) (typed FeaturePython)
  n = 5
  ref = C_element
FEATURE [App::DocumentObjectGroupPython] N_element052  label="N_element : 024"  # scripted group (container) (typed FeaturePython)
  n = 2
  ref = N_element
FEATURE [App::DocumentObjectGroupPython] O_element114  label="O_element : 067"  # scripted group (container) (typed FeaturePython)
  n = 2
  ref = O_element
FEATURE [App::DocumentObjectGroupPython] G4_THYMINE  # scripted group (container) (typed FeaturePython)
  Dunit = g/cm3
  Dvalue = 1.23
  Group = -> [H_element122,C_element132,N_element052,O_element114]
  conduct = 2
  density = 1
  expand = 3
  formula = G4_THYMINE
  name = G4_THYMINE
  specific = 4
FEATURE [App::DocumentObjectGroupPython] H_element123  label="H_element : 070"  # scripted group (container) (typed FeaturePython)
  n = 4
  ref = H_element
FEATURE [App::DocumentObjectGroupPython] C_element133  label="C_element : 078"  # scripted group (container) (typed FeaturePython)
  n = 4
  ref = C_element
FEATURE [App::DocumentObjectGroupPython] N_element053  label="N_element : 025"  # scripted group (container) (typed FeaturePython)
  n = 2
  ref = N_element
FEATURE [App::DocumentObjectGroupPython] O_element115  label="O_element : 068"  # scripted group (container) (typed FeaturePython)
  n = 2
  ref = O_element
FEATURE [App::DocumentObjectGroupPython] G4_URACIL  # scripted group (container) (typed FeaturePython)
  Dunit = g/cm3
  Dvalue = 1.32
  Group = -> [H_element123,C_element133,N_element053,O_element115]
  conduct = 2
  density = 1
  expand = 3
  formula = G4_URACIL
  name = G4_URACIL
  specific = 4
FEATURE [App::DocumentObjectGroupPython] H_element124  label="H_element : 071"  # scripted group (container) (typed FeaturePython)
  n = 4
  ref = H_element
FEATURE [App::DocumentObjectGroupPython] C_element134  label="C_element : 079"  # scripted group (container) (typed FeaturePython)
  n = 5
  ref = C_element
FEATURE [App::DocumentObjectGroupPython] N_element054  label="N_element : 026"  # scripted group (container) (typed FeaturePython)
  n = 5
  ref = N_element
FEATURE [App::DocumentObjectGroupPython] G4_DNA_ADENINE  # scripted group (container) (typed FeaturePython)
  Dunit = g/cm3
  Dvalue = 1
  Group = -> [H_element124,C_element134,N_element054]
  conduct = 2
  density = 1
  expand = 3
  formula = G4_DNA_ADENINE
  name = G4_DNA_ADENINE
  specific = 4
FEATURE [App::DocumentObjectGroupPython] H_element125  label="H_element : 072"  # scripted group (container) (typed FeaturePython)
  n = 4
  ref = H_element
FEATURE [App::DocumentObjectGroupPython] C_element135  label="C_element : 080"  # scripted group (container) (typed FeaturePython)
  n = 5
  ref = C_element
FEATURE [App::DocumentObjectGroupPython] N_element055  label="N_element : 027"  # scripted group (container) (typed FeaturePython)
  n = 5
  ref = N_element
FEATURE [App::DocumentObjectGroupPython] O_element116  label="O_element : 069"  # scripted group (container) (typed FeaturePython)
  n = 1
  ref = O_element
FEATURE [App::DocumentObjectGroupPython] G4_DNA_GUANINE  # scripted group (container) (typed FeaturePython)
  Dunit = g/cm3
  Dvalue = 1
  Group = -> [H_element125,C_element135,N_element055,O_element116]
  conduct = 2
  density = 1
  expand = 3
  formula = G4_DNA_GUANINE
  name = G4_DNA_GUANINE
  specific = 4
FEATURE [App::DocumentObjectGroupPython] H_element126  label="H_element : 073"  # scripted group (container) (typed FeaturePython)
  n = 4
  ref = H_element
FEATURE [App::DocumentObjectGroupPython] C_element136  label="C_element : 081"  # scripted group (container) (typed FeaturePython)
  n = 4
  ref = C_element
FEATURE [App::DocumentObjectGroupPython] N_element056  label="N_element : 028"  # scripted group (container) (typed FeaturePython)
  n = 3
  ref = N_element
FEATURE [App::DocumentObjectGroupPython] O_element117  label="O_element : 070"  # scripted group (container) (typed FeaturePython)
  n = 1
  ref = O_element
FEATURE [App::DocumentObjectGroupPython] G4_DNA_CYTOSINE  # scripted group (container) (typed FeaturePython)
  Dunit = g/cm3
  Dvalue = 1
  Group = -> [H_element126,C_element136,N_element056,O_element117]
  conduct = 2
  density = 1
  expand = 3
  formula = G4_DNA_CYTOSINE
  name = G4_DNA_CYTOSINE
  specific = 4
FEATURE [App::DocumentObjectGroupPython] H_element127  label="H_element : 074"  # scripted group (container) (typed FeaturePython)
  n = 5
  ref = H_element
FEATURE [App::DocumentObjectGroupPython] C_element137  label="C_element : 082"  # scripted group (container) (typed FeaturePython)
  n = 5
  ref = C_element
FEATURE [App::DocumentObjectGroupPython] N_element057  label="N_element : 029"  # scripted group (container) (typed FeaturePython)
  n = 2
  ref = N_element
FEATURE [App::DocumentObjectGroupPython] O_element118  label="O_element : 071"  # scripted group (container) (typed FeaturePython)
  n = 2
  ref = O_element
FEATURE [App::DocumentObjectGroupPython] G4_DNA_THYMINE  # scripted group (container) (typed FeaturePython)
  Dunit = g/cm3
  Dvalue = 1
  Group = -> [H_element127,C_element137,N_element057,O_element118]
  conduct = 2
  density = 1
  expand = 3
  formula = G4_DNA_THYMINE
  name = G4_DNA_THYMINE
  specific = 4
FEATURE [App::DocumentObjectGroupPython] H_element128  label="H_element : 075"  # scripted group (container) (typed FeaturePython)
  n = 3
  ref = H_element
FEATURE [App::DocumentObjectGroupPython] C_element138  label="C_element : 083"  # scripted group (container) (typed FeaturePython)
  n = 4
  ref = C_element
FEATURE [App::DocumentObjectGroupPython] N_element058  label="N_element : 030"  # scripted group (container) (typed FeaturePython)
  n = 2
  ref = N_element
FEATURE [App::DocumentObjectGroupPython] O_element119  label="O_element : 072"  # scripted group (container) (typed FeaturePython)
  n = 2
  ref = O_element
FEATURE [App::DocumentObjectGroupPython] G4_DNA_URACIL  # scripted group (container) (typed FeaturePython)
  Dunit = g/cm3
  Dvalue = 1
  Group = -> [H_element128,C_element138,N_element058,O_element119]
  conduct = 2
  density = 1
  expand = 3
  formula = G4_DNA_URACIL
  name = G4_DNA_URACIL
  specific = 4
FEATURE [App::DocumentObjectGroupPython] H_element129  label="H_element : 076"  # scripted group (container) (typed FeaturePython)
  n = 10
  ref = H_element
FEATURE [App::DocumentObjectGroupPython] C_element139  label="C_element : 084"  # scripted group (container) (typed FeaturePython)
  n = 10
  ref = C_element
FEATURE [App::DocumentObjectGroupPython] N_element059  label="N_element : 031"  # scripted group (container) (typed FeaturePython)
  n = 5
  ref = N_element
FEATURE [App::DocumentObjectGroupPython] O_element120  label="O_element : 073"  # scripted group (container) (typed FeaturePython)
  n = 4
  ref = O_element
FEATURE [App::DocumentObjectGroupPython] G4_DNA_ADENOSINE  # scripted group (container) (typed FeaturePython)
  Dunit = g/cm3
  Dvalue = 1
  Group = -> [H_element129,C_element139,N_element059,O_element120]
  conduct = 2
  density = 1
  expand = 3
  formula = G4_DNA_ADENOSINE
  name = G4_DNA_ADENOSINE
  specific = 4
FEATURE [App::DocumentObjectGroupPython] H_element130  label="H_element : 077"  # scripted group (container) (typed FeaturePython)
  n = 10
  ref = H_element
FEATURE [App::DocumentObjectGroupPython] C_element140  label="C_element : 085"  # scripted group (container) (typed FeaturePython)
  n = 10
  ref = C_element
FEATURE [App::DocumentObjectGroupPython] N_element060  label="N_element : 032"  # scripted group (container) (typed FeaturePython)
  n = 5
  ref = N_element
FEATURE [App::DocumentObjectGroupPython] O_element121  label="O_element : 074"  # scripted group (container) (typed FeaturePython)
  n = 5
  ref = O_element
FEATURE [App::DocumentObjectGroupPython] G4_DNA_GUANOSINE  # scripted group (container) (typed FeaturePython)
  Dunit = g/cm3
  Dvalue = 1
  Group = -> [H_element130,C_element140,N_element060,O_element121]
  conduct = 2
  density = 1
  expand = 3
  formula = G4_DNA_GUANOSINE
  name = G4_DNA_GUANOSINE
  specific = 4
FEATURE [App::DocumentObjectGroupPython] H_element131  label="H_element : 078"  # scripted group (container) (typed FeaturePython)
  n = 10
  ref = H_element
FEATURE [App::DocumentObjectGroupPython] C_element141  label="C_element : 086"  # scripted group (container) (typed FeaturePython)
  n = 9
  ref = C_element
FEATURE [App::DocumentObjectGroupPython] N_element061  label="N_element : 033"  # scripted group (container) (typed FeaturePython)
  n = 3
  ref = N_element
FEATURE [App::DocumentObjectGroupPython] O_element122  label="O_element : 075"  # scripted group (container) (typed FeaturePython)
  n = 5
  ref = O_element
FEATURE [App::DocumentObjectGroupPython] G4_DNA_CYTIDINE  # scripted group (container) (typed FeaturePython)
  Dunit = g/cm3
  Dvalue = 1
  Group = -> [H_element131,C_element141,N_element061,O_element122]
  conduct = 2
  density = 1
  expand = 3
  formula = G4_DNA_CYTIDINE
  name = G4_DNA_CYTIDINE
  specific = 4
FEATURE [App::DocumentObjectGroupPython] H_element132  label="H_element : 079"  # scripted group (container) (typed FeaturePython)
  n = 9
  ref = H_element
FEATURE [App::DocumentObjectGroupPython] C_element142  label="C_element : 087"  # scripted group (container) (typed FeaturePython)
  n = 9
  ref = C_element
FEATURE [App::DocumentObjectGroupPython] N_element062  label="N_element : 034"  # scripted group (container) (typed FeaturePython)
  n = 2
  ref = N_element
FEATURE [App::DocumentObjectGroupPython] O_element123  label="O_element : 076"  # scripted group (container) (typed FeaturePython)
  n = 6
  ref = O_element
FEATURE [App::DocumentObjectGroupPython] G4_DNA_URIDINE  # scripted group (container) (typed FeaturePython)
  Dunit = g/cm3
  Dvalue = 1
  Group = -> [H_element132,C_element142,N_element062,O_element123]
  conduct = 2
  density = 1
  expand = 3
  formula = G4_DNA_URIDINE
  name = G4_DNA_URIDINE
  specific = 4
FEATURE [App::DocumentObjectGroupPython] H_element133  label="H_element : 080"  # scripted group (container) (typed FeaturePython)
  n = 11
  ref = H_element
FEATURE [App::DocumentObjectGroupPython] C_element143  label="C_element : 088"  # scripted group (container) (typed FeaturePython)
  n = 10
  ref = C_element
FEATURE [App::DocumentObjectGroupPython] N_element063  label="N_element : 035"  # scripted group (container) (typed FeaturePython)
  n = 2
  ref = N_element
FEATURE [App::DocumentObjectGroupPython] O_element124  label="O_element : 077"  # scripted group (container) (typed FeaturePython)
  n = 6
  ref = O_element
FEATURE [App::DocumentObjectGroupPython] G4_DNA_METHYLURIDINE  # scripted group (container) (typed FeaturePython)
  Dunit = g/cm3
  Dvalue = 1
  Group = -> [H_element133,C_element143,N_element063,O_element124]
  conduct = 2
  density = 1
  expand = 3
  formula = G4_DNA_METHYLURIDINE
  name = G4_DNA_METHYLURIDINE
  specific = 4
FEATURE [App::DocumentObjectGroupPython] P_element014  label="P_element : 003"  # scripted group (container) (typed FeaturePython)
  n = 1
  ref = P_element
FEATURE [App::DocumentObjectGroupPython] O_element125  label="O_element : 078"  # scripted group (container) (typed FeaturePython)
  n = 3
  ref = O_element
FEATURE [App::DocumentObjectGroupPython] G4_DNA_MONOPHOSPHATE  # scripted group (container) (typed FeaturePython)
  Dunit = g/cm3
  Dvalue = 1
  Group = -> [P_element014,O_element125]
  conduct = 2
  density = 1
  expand = 3
  formula = G4_DNA_MONOPHOSPHATE
  name = G4_DNA_MONOPHOSPHATE
  specific = 4
FEATURE [App::DocumentObjectGroupPython] H_element134  label="H_element : 081"  # scripted group (container) (typed FeaturePython)
  n = 10
  ref = H_element
FEATURE [App::DocumentObjectGroupPython] C_element144  label="C_element : 089"  # scripted group (container) (typed FeaturePython)
  n = 10
  ref = C_element
FEATURE [App::DocumentObjectGroupPython] N_element064  label="N_element : 036"  # scripted group (container) (typed FeaturePython)
  n = 5
  ref = N_element
FEATURE [App::DocumentObjectGroupPython] O_element126  label="O_element : 079"  # scripted group (container) (typed FeaturePython)
  n = 7
  ref = O_element
FEATURE [App::DocumentObjectGroupPython] P_element015  label="P_element : 004"  # scripted group (container) (typed FeaturePython)
  n = 1
  ref = P_element
FEATURE [App::DocumentObjectGroupPython] G4_DNA_A  # scripted group (container) (typed FeaturePython)
  Dunit = g/cm3
  Dvalue = 1
  Group = -> [H_element134,C_element144,N_element064,O_element126,P_element015]
  conduct = 2
  density = 1
  expand = 3
  formula = G4_DNA_A
  name = G4_DNA_A
  specific = 4
FEATURE [App::DocumentObjectGroupPython] H_element135  label="H_element : 082"  # scripted group (container) (typed FeaturePython)
  n = 10
  ref = H_element
FEATURE [App::DocumentObjectGroupPython] C_element145  label="C_element : 090"  # scripted group (container) (typed FeaturePython)
  n = 10
  ref = C_element
FEATURE [App::DocumentObjectGroupPython] N_element065  label="N_element : 037"  # scripted group (container) (typed FeaturePython)
  n = 5
  ref = N_element
FEATURE [App::DocumentObjectGroupPython] O_element127  label="O_element : 8"  # scripted group (container) (typed FeaturePython)
  n = 8
  ref = O_element
FEATURE [App::DocumentObjectGroupPython] P_element016  label="P_element : 005"  # scripted group (container) (typed FeaturePython)
  n = 1
  ref = P_element
FEATURE [App::DocumentObjectGroupPython] G4_DNA_G  # scripted group (container) (typed FeaturePython)
  Dunit = g/cm3
  Dvalue = 1
  Group = -> [H_element135,C_element145,N_element065,O_element127,P_element016]
  conduct = 2
  density = 1
  expand = 3
  formula = G4_DNA_G
  name = G4_DNA_G
  specific = 4
FEATURE [App::DocumentObjectGroupPython] H_element136  label="H_element : 083"  # scripted group (container) (typed FeaturePython)
  n = 10
  ref = H_element
FEATURE [App::DocumentObjectGroupPython] C_element146  label="C_element : 091"  # scripted group (container) (typed FeaturePython)
  n = 9
  ref = C_element
FEATURE [App::DocumentObjectGroupPython] N_element066  label="N_element : 038"  # scripted group (container) (typed FeaturePython)
  n = 3
  ref = N_element
FEATURE [App::DocumentObjectGroupPython] O_element128  label="O_element : 080"  # scripted group (container) (typed FeaturePython)
  n = 8
  ref = O_element
FEATURE [App::DocumentObjectGroupPython] P_element017  label="P_element : 006"  # scripted group (container) (typed FeaturePython)
  n = 1
  ref = P_element
FEATURE [App::DocumentObjectGroupPython] G4_DNA_C  # scripted group (container) (typed FeaturePython)
  Dunit = g/cm3
  Dvalue = 1
  Group = -> [H_element136,C_element146,N_element066,O_element128,P_element017]
  conduct = 2
  density = 1
  expand = 3
  formula = G4_DNA_C
  name = G4_DNA_C
  specific = 4
FEATURE [App::DocumentObjectGroupPython] H_element137  label="H_element : 084"  # scripted group (container) (typed FeaturePython)
  n = 9
  ref = H_element
FEATURE [App::DocumentObjectGroupPython] C_element147  label="C_element : 092"  # scripted group (container) (typed FeaturePython)
  n = 9
  ref = C_element
FEATURE [App::DocumentObjectGroupPython] N_element067  label="N_element : 039"  # scripted group (container) (typed FeaturePython)
  n = 2
  ref = N_element
FEATURE [App::DocumentObjectGroupPython] O_element129  label="O_element : 9"  # scripted group (container) (typed FeaturePython)
  n = 9
  ref = O_element
FEATURE [App::DocumentObjectGroupPython] P_element018  label="P_element : 007"  # scripted group (container) (typed FeaturePython)
  n = 1
  ref = P_element
FEATURE [App::DocumentObjectGroupPython] G4_DNA_U  # scripted group (container) (typed FeaturePython)
  Dunit = g/cm3
  Dvalue = 1
  Group = -> [H_element137,C_element147,N_element067,O_element129,P_element018]
  conduct = 2
  density = 1
  expand = 3
  formula = G4_DNA_U
  name = G4_DNA_U
  specific = 4
FEATURE [App::DocumentObjectGroupPython] H_element138  label="H_element : 085"  # scripted group (container) (typed FeaturePython)
  n = 11
  ref = H_element
FEATURE [App::DocumentObjectGroupPython] C_element148  label="C_element : 093"  # scripted group (container) (typed FeaturePython)
  n = 10
  ref = C_element
FEATURE [App::DocumentObjectGroupPython] N_element068  label="N_element : 040"  # scripted group (container) (typed FeaturePython)
  n = 2
  ref = N_element
FEATURE [App::DocumentObjectGroupPython] O_element130  label="O_element : 081"  # scripted group (container) (typed FeaturePython)
  n = 9
  ref = O_element
FEATURE [App::DocumentObjectGroupPython] P_element019  label="P_element : 008"  # scripted group (container) (typed FeaturePython)
  n = 1
  ref = P_element
FEATURE [App::DocumentObjectGroupPython] G4_DNA_MU  # scripted group (container) (typed FeaturePython)
  Dunit = g/cm3
  Dvalue = 1
  Group = -> [H_element138,C_element148,N_element068,O_element130,P_element019]
  conduct = 2
  density = 1
  expand = 3
  formula = G4_DNA_MU
  name = G4_DNA_MU
  specific = 4
FEATURE [App::DocumentObjectGroupPython] BioChemical  # scripted group (container) (typed FeaturePython)
  Group = -> [G4_CYTOSINE,G4_THYMINE,G4_URACIL,G4_DNA_ADENINE,G4_DNA_GUANINE,G4_DNA_CYTOSINE,G4_DNA_THYMINE,G4_DNA_URACIL,G4_DNA_ADENOSINE,G4_DNA_GUANOSINE,G4_DNA_CYTIDINE,G4_DNA_URIDINE,G4_DNA_METHYLURIDINE,G4_DNA_MONOPHOSPHATE,G4_DNA_A,G4_DNA_G,G4_DNA_C,G4_DNA_U,G4_DNA_MU]
FEATURE [App::DocumentObjectGroupPython] G4Materials  # scripted group (container) (typed FeaturePython)
  Group = -> [NIST,Element,HEP,Space,BioChemical]
  version = 1
FEATURE [App::DocumentObjectGroupPython] Geant4  # scripted group (container) (typed FeaturePython)
  Group = -> [G4Isotopes,G4Elements,G4Materials]
FEATURE [App::DocumentObjectGroupPython] Materials  # scripted group (container) (typed FeaturePython)
  Group = -> [Geant4]
FEATURE [Part::FeaturePython] GDMLBox_WorldBox  # WARN: FeaturePython — macro-defined, semantics opaque (R4)
  lunit = 2
  material = 5
  x = 273
  y = 273
  z = 130
FEATURE [Part::FeaturePython] GDMLBox_Box  # WARN: FeaturePython — macro-defined, semantics opaque (R4)
  lunit = 2
  material = 0
  x = 10
  y = 10
  z = 10
FEATURE [Part::FeaturePython] GDMLTube  # WARN: FeaturePython — macro-defined, semantics opaque (R4)
  Placement = pos=(-3,-4,0) rot=(0,0,1;0rad)
  aunit = 1
  deltaphi = 90
  lunit = 2
  material = 0
  rmax = 7
  rmin = 5
  startphi = 0
  z = 7
FEATURE [App::Part] LV_Tube
  Group = -> [GDMLTube]
  Origin = -> Origin003
  SkinSurface = 0
FEATURE [App::Part] LV_Box
  Group = -> [GDMLBox_Box,LV_Tube]
  Origin = -> Origin002
  Placement = pos=(20,0,0) rot=(0,0,1;0rad)
FEATURE [Part::FeaturePython] Array  # Draft array (typed FeaturePython)
  AlwaysSyncPlacement = false
  Angle = 180
  ArrayType = 1
  Axis = (0,0,1)
  Base = -> LV_Box
  Center = (0,0,0)
  Count = 5
  ExpandArray = false
  Fuse = false
  IntervalAxis = (0,0,0)
  IntervalX = (100,0,0)
  IntervalY = (0,100,0)
  IntervalZ = (0,0,100)
  NumberCircles = 3
  NumberPolar = 5
  NumberX = 2
  NumberY = 2
  NumberZ = 1
  PlacementList = 5 placements: [(20,0,0),(14.1421,14.1421,0),(3.55271e-15,20,0),(-14.1421,14.1421,0),(-20,2.44929e-15,0)]
  RadialDistance = 50
  ScaleList = (5) [(1,1,1),(1,1,1),(1,1,1),(1,1,1),(1,1,1)]
  Symmetry = 1
  TangentialDistance = 25
FEATURE [App::Part] Part  label="experiment"
  Group = -> [LV_Box,Array]
  Origin = -> Origin001
FEATURE [App::Part] worldVOL
  Group = -> [GDMLBox_WorldBox,Part]
  Origin = -> Origin
